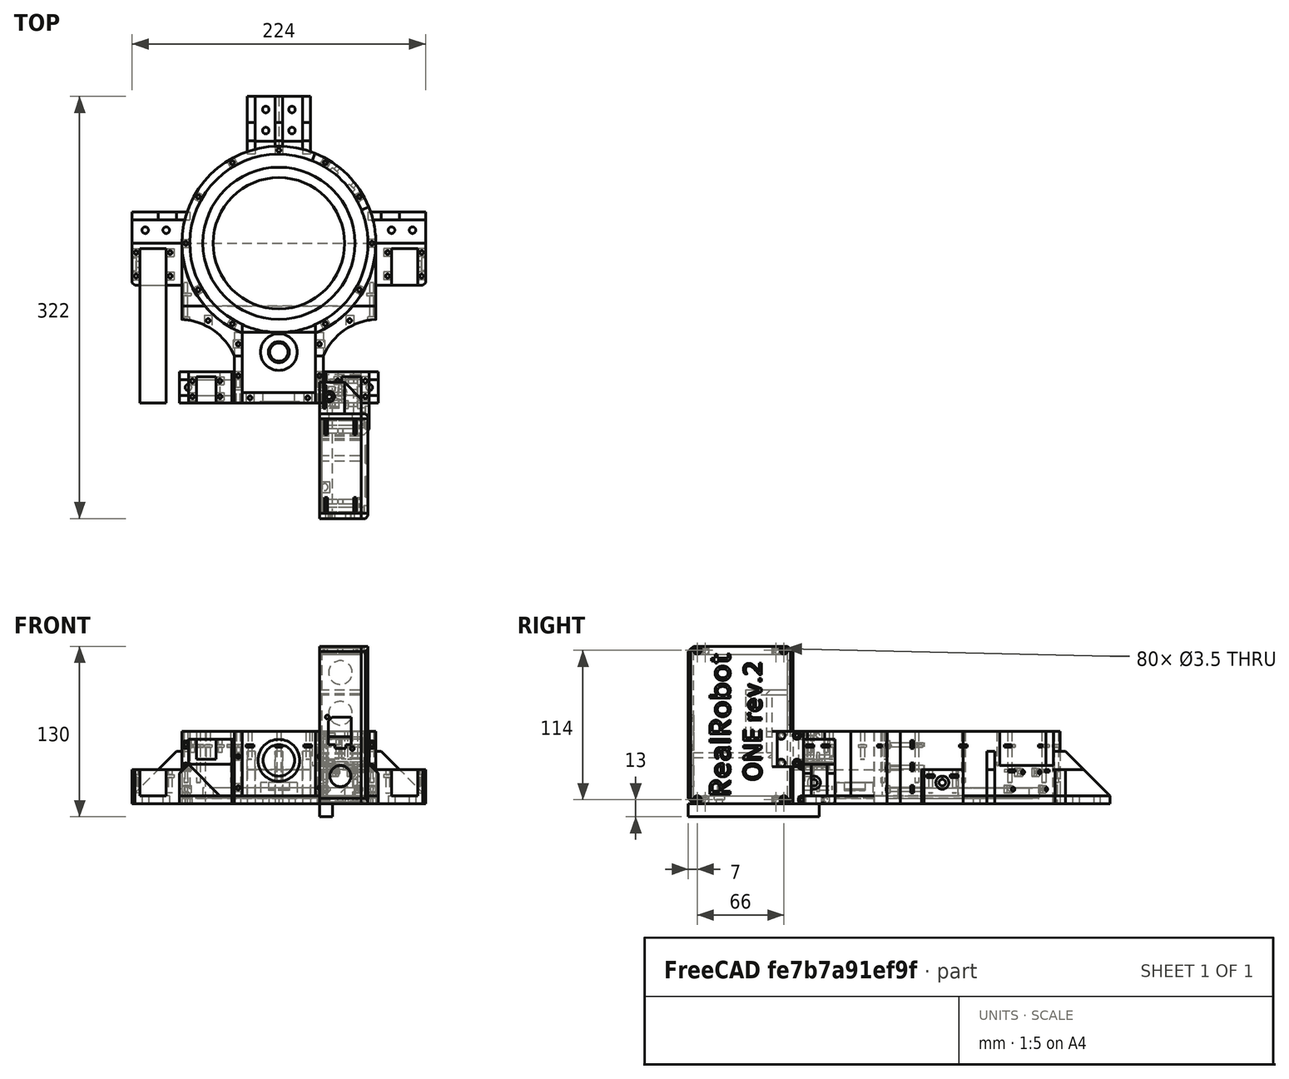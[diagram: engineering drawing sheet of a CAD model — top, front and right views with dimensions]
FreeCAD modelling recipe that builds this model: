
FCSTD DOCUMENT  (FreeCAD 0.19R24276 (Git))
Label: Ele-modules_029
License: All rights reserved
LicenseURL: http://en.wikipedia.org/wiki/All_rights_reserved
objects: Part::Cylinder×371, Part::Box×289, Part::Cut×232, Part::Compound×163, Part::Chamfer×49, Mesh::Feature×14, Part::FeaturePython×4, Part::Mirroring×3, Part::Part2DObjectPython×2, Part::Extrusion×2
note: 1115 computed .brp shape members not serialized (recipe doc carries the construction recipe); baked Part::Feature solids carry a one-line shape summary decoded from their .brp

FEATURE [Part::Cylinder] Cylinder1012  label="Válec1012"
  Angle = 360
  AttacherType = Attacher::AttachEngine3D
  Height = 10
  Placement = pos=(29,6,39) rot=(1,0,0;1.5708rad)
  Radius = 1.5
FEATURE [Part::Box] Box510  label="Krychle510"
  AttacherType = Attacher::AttachEngine3D
  Height = 6
  Length = 2
  Placement = pos=(34,64,0) rot=(0,0,1;0rad)
  Width = 6
FEATURE [Part::Cylinder] Cylinder1013  label="Válec1013"
  Angle = 360
  AttacherType = Attacher::AttachEngine3D
  Height = 60
  Placement = pos=(26,13,117) rot=(0,1,0;1.5708rad)
  Radius = 1.75
FEATURE [Part::Box] Box506  label="Krychle506"
  AttacherType = Attacher::AttachEngine3D
  Height = 6
  Length = 2
  Placement = pos=(34,64,114) rot=(0,0,1;0rad)
  Width = 6
FEATURE [Part::Box] Box509  label="Krychle509"
  AttacherType = Attacher::AttachEngine3D
  Height = 6
  Length = 2
  Placement = pos=(34,10,0) rot=(0,0,1;0rad)
  Width = 6
FEATURE [Part::Cylinder] Cylinder1011  label="Válec1011"
  Angle = 360
  AttacherType = Attacher::AttachEngine3D
  Height = 10
  Placement = pos=(16,82,66) rot=(1,0,0;1.5708rad)
  Radius = 9
FEATURE [Part::Box] Box505  label="Krychle505"
  AttacherType = Attacher::AttachEngine3D
  Height = 6
  Length = 2
  Placement = pos=(34,10,0) rot=(0,0,1;0rad)
  Width = 6
FEATURE [Part::Box] Box508  label="Krychle508"
  AttacherType = Attacher::AttachEngine3D
  Height = 6
  Length = 2
  Placement = pos=(34,10,114) rot=(0,0,1;0rad)
  Width = 6
FEATURE [Part::Cylinder] Cylinder1014  label="Válec1014"
  Angle = 360
  AttacherType = Attacher::AttachEngine3D
  Height = 10
  Placement = pos=(29,21,0) rot=(0,0,1;0rad)
  Radius = 1.5
FEATURE [Part::Cylinder] Cylinder1015  label="Válec1015"
  Angle = 360
  AttacherType = Attacher::AttachEngine3D
  Height = 60
  Placement = pos=(26,13,3) rot=(0,1,0;1.5708rad)
  Radius = 1.75
FEATURE [Part::Box] Box507  label="Krychle507"
  AttacherType = Attacher::AttachEngine3D
  Height = 108
  Length = 30
  Placement = pos=(2,4,3) rot=(0,0,1;0rad)
  Width = 72
FEATURE [Part::Box] Box515  label="Krychle515"
  AttacherType = Attacher::AttachEngine3D
  Height = 6
  Length = 2
  Placement = pos=(34,10,114) rot=(0,0,1;0rad)
  Width = 6
FEATURE [Part::Box] Box516  label="Krychle516"
  AttacherType = Attacher::AttachEngine3D
  Height = 2
  Length = 6
  Placement = pos=(0,40,3) rot=(0,0,1;0rad)
  Width = 6
FEATURE [Part::Box] Box518  label="Krychle518"
  AttacherType = Attacher::AttachEngine3D
  Height = 3
  Length = 8
  Placement = pos=(12,-2,39) rot=(0,0,1;0rad)
  Width = 10
FEATURE [Part::Cylinder] Cylinder1024  label="Válec1024"
  Angle = 360
  AttacherType = Attacher::AttachEngine3D
  Height = 3
  Placement = pos=(26,73,3) rot=(0,1,0;1.5708rad)
  Radius = 3
FEATURE [Part::Cylinder] Cylinder1022  label="Válec1022"
  Angle = 360
  AttacherType = Attacher::AttachEngine3D
  Height = 10
  Placement = pos=(16,6,18) rot=(1,0,0;1.5708rad)
  Radius = 8
FEATURE [Part::Cylinder] Cylinder1028  label="Válec1028"
  Angle = 360
  AttacherType = Attacher::AttachEngine3D
  Height = 3
  Placement = pos=(26,7,3) rot=(0,1,0;1.5708rad)
  Radius = 3
FEATURE [Part::Cylinder] Cylinder1019  label="Válec1019"
  Angle = 360
  AttacherType = Attacher::AttachEngine3D
  Height = 10
  Placement = pos=(3,43,0) rot=(0,0,1;0rad)
  Radius = 1.5
FEATURE [Part::Box] Box514  label="Krychle514"
  AttacherType = Attacher::AttachEngine3D
  Height = 21
  Length = 17.5
  Placement = pos=(10.75,-2,42) rot=(0,0,1;0rad)
  Width = 10
FEATURE [Part::Chamfer] Chamfer034
  Base = -> Box514
  Edges = 1 edges r=3: [Edge2]
  Placement = pos=(-4,0,0) rot=(0,0,1;0rad)
FEATURE [Part::Cylinder] Cylinder1018  label="Válec1018"
  Angle = 360
  AttacherType = Attacher::AttachEngine3D
  Height = 60
  Placement = pos=(26,67,3) rot=(0,1,0;1.5708rad)
  Radius = 1.75
FEATURE [Part::Cylinder] Cylinder1025  label="Válec1025"
  Angle = 360
  AttacherType = Attacher::AttachEngine3D
  Height = 60
  Placement = pos=(26,13,117) rot=(0,1,0;1.5708rad)
  Radius = 1.75
FEATURE [Part::Box] Box513  label="Krychle513"
  AttacherType = Attacher::AttachEngine3D
  Height = 6
  Length = 2
  Placement = pos=(34,64,114) rot=(0,0,1;0rad)
  Width = 6
FEATURE [Part::Compound] Compound538
  Links = -> [Box505,Box510,Box508,Box513]
  Placement = pos=(-8,0,-3) rot=(0,0,1;0rad)
FEATURE [Part::Box] Box511  label="Krychle511"
  AttacherType = Attacher::AttachEngine3D
  Height = 120
  Length = 32
  Placement = pos=(0,0,-3) rot=(0,0,1;0rad)
  Width = 80
FEATURE [Part::Cut] Cut472
  Base = -> Box511
  Tool = -> Box507
FEATURE [Part::Cylinder] Cylinder1017  label="Válec1017"
  Angle = 360
  AttacherType = Attacher::AttachEngine3D
  Height = 60
  Placement = pos=(26,67,117) rot=(0,1,0;1.5708rad)
  Radius = 1.75
FEATURE [Part::Compound] Compound544
  Links = -> [Cylinder1015,Cylinder1018,Cylinder1013,Cylinder1017]
  Placement = pos=(-8,0,-3) rot=(0,0,1;0rad)
FEATURE [Part::Box] Box512  label="Krychle512"
  AttacherType = Attacher::AttachEngine3D
  Height = 2
  Length = 6
  Placement = pos=(26,18,3) rot=(0,0,1;0rad)
  Width = 6
FEATURE [Part::Cylinder] Cylinder1016  label="Válec1016"
  Angle = 360
  AttacherType = Attacher::AttachEngine3D
  Height = 10
  Placement = pos=(10,6,63) rot=(1,0,0;1.5708rad)
  Radius = 1.5
FEATURE [Part::Compound] Compound543
  Links = -> [Cylinder1016,Cylinder1012]
  Placement = pos=(-4,0,0) rot=(0,0,1;0rad)
FEATURE [Part::Cylinder] Cylinder1020  label="Válec1020"
  Angle = 360
  AttacherType = Attacher::AttachEngine3D
  Height = 10
  Placement = pos=(3,21,0) rot=(0,0,1;0rad)
  Radius = 1.5
FEATURE [Part::Cylinder] Cylinder1021  label="Válec1021"
  Angle = 360
  AttacherType = Attacher::AttachEngine3D
  Height = 60
  Placement = pos=(26,13,3) rot=(0,1,0;1.5708rad)
  Radius = 1.75
FEATURE [Part::Box] Box517  label="Krychle517"
  AttacherType = Attacher::AttachEngine3D
  Height = 2
  Length = 6
  Placement = pos=(26,40,3) rot=(0,0,1;0rad)
  Width = 6
FEATURE [Part::Cylinder] Cylinder1023  label="Válec1023"
  Angle = 360
  AttacherType = Attacher::AttachEngine3D
  Height = 100
  Placement = pos=(26,73,117) rot=(0,1,0;1.5708rad)
  Radius = 1.75
FEATURE [Part::Cylinder] Cylinder1026  label="Válec1026"
  Angle = 360
  AttacherType = Attacher::AttachEngine3D
  Height = 3
  Placement = pos=(26,7,117) rot=(0,1,0;1.5708rad)
  Radius = 3
FEATURE [Part::Cylinder] Cylinder1027  label="Válec1027"
  Angle = 360
  AttacherType = Attacher::AttachEngine3D
  Height = 60
  Placement = pos=(26,67,3) rot=(0,1,0;1.5708rad)
  Radius = 1.75
FEATURE [Part::Cylinder] Cylinder1036  label="Válec1036"
  Angle = 360
  AttacherType = Attacher::AttachEngine3D
  Height = 3
  Placement = pos=(26,7,3) rot=(0,1,0;1.5708rad)
  Radius = 3
FEATURE [Part::Cylinder] Cylinder1030  label="Válec1030"
  Angle = 360
  AttacherType = Attacher::AttachEngine3D
  Height = 100
  Placement = pos=(26,7,117) rot=(0,1,0;1.5708rad)
  Radius = 1.75
FEATURE [Part::Cylinder] Cylinder1034  label="Válec1034"
  Angle = 360
  AttacherType = Attacher::AttachEngine3D
  Height = 10
  Placement = pos=(29,43,0) rot=(0,0,1;0rad)
  Radius = 1.5
FEATURE [Part::Cylinder] Cylinder1029  label="Válec1029"
  Angle = 360
  AttacherType = Attacher::AttachEngine3D
  Height = 100
  Placement = pos=(26,73,3) rot=(0,1,0;1.5708rad)
  Radius = 1.75
FEATURE [Part::Cylinder] Cylinder1033  label="Válec1033"
  Angle = 360
  AttacherType = Attacher::AttachEngine3D
  Height = 3
  Placement = pos=(26,73,117) rot=(0,1,0;1.5708rad)
  Radius = 3
FEATURE [Part::Cylinder] Cylinder1035  label="Válec1035"
  Angle = 360
  AttacherType = Attacher::AttachEngine3D
  Height = 3
  Placement = pos=(26,73,3) rot=(0,1,0;1.5708rad)
  Radius = 3
FEATURE [Part::Box] Box526  label="Krychle526"
  AttacherType = Attacher::AttachEngine3D
  Height = 6
  Length = 2
  Placement = pos=(26,68,46) rot=(0,0,1;0rad)
  Width = 6
FEATURE [Part::Cylinder] Cylinder1039  label="Válec1039"
  Angle = 360
  AttacherType = Attacher::AttachEngine3D
  Height = 20
  Placement = pos=(24.5,77,20) rot=(0,0,1;0rad)
  Radius = 2
FEATURE [Part::Cylinder] Cylinder1038  label="Válec1038"
  Angle = 360
  AttacherType = Attacher::AttachEngine3D
  Height = 3
  Placement = pos=(26,73,117) rot=(0,1,0;1.5708rad)
  Radius = 3
FEATURE [Part::Compound] Compound542
  Links = -> [Cylinder1036,Cylinder1035,Cylinder1026,Cylinder1038]
  Placement = pos=(3,0,-3) rot=(0,0,1;0rad)
FEATURE [Part::Cylinder] Cylinder1041  label="Válec1041"
  Angle = 360
  AttacherType = Attacher::AttachEngine3D
  Height = 20
  Placement = pos=(20,71,49) rot=(0,1,0;1.5708rad)
  Radius = 1.5
FEATURE [Part::Cylinder] Cylinder1032  label="Válec1032"
  Angle = 360
  AttacherType = Attacher::AttachEngine3D
  Height = 60
  Placement = pos=(26,67,117) rot=(0,1,0;1.5708rad)
  Radius = 1.75
FEATURE [Part::Compound] Compound537
  Links = -> [Cylinder1021,Cylinder1027,Cylinder1025,Cylinder1032]
  Placement = pos=(-72,0,-3) rot=(0,0,1;0rad)
FEATURE [Part::Box] Box523  label="Krychle523"
  AttacherType = Attacher::AttachEngine3D
  Height = 15
  Length = 15
  Placement = pos=(17,68,31) rot=(0,0,1;0rad)
  Width = 80
FEATURE [Part::Cylinder] Cylinder1042  label="Válec1042"
  Angle = 360
  AttacherType = Attacher::AttachEngine3D
  Height = 20
  Placement = pos=(20,71,28) rot=(0,1,0;1.5708rad)
  Radius = 1.5
FEATURE [Part::Box] Box520  label="Krychle520"
  AttacherType = Attacher::AttachEngine3D
  Height = 2
  Length = 6
  Placement = pos=(0,18,3) rot=(0,0,1;0rad)
  Width = 6
FEATURE [Part::Compound] Compound539
  Links = -> [Box520,Box516,Box517,Box512]
  Placement = pos=(0,0,-100) rot=(0,0,1;0rad)
FEATURE [Part::Box] Box519  label="Krychle519"
  AttacherType = Attacher::AttachEngine3D
  Height = 6
  Length = 2
  Placement = pos=(34,64,0) rot=(0,0,1;0rad)
  Width = 6
FEATURE [Part::Compound] Compound540
  Links = -> [Box509,Box519,Box515,Box506]
  Placement = pos=(-30,0,-3) rot=(0,0,1;0rad)
FEATURE [Part::Cylinder] Cylinder1031  label="Válec1031"
  Angle = 360
  AttacherType = Attacher::AttachEngine3D
  Height = 100
  Placement = pos=(26,7,3) rot=(0,1,0;1.5708rad)
  Radius = 1.75
FEATURE [Part::Compound] Compound536
  Links = -> [Cylinder1031,Cylinder1029,Cylinder1030,Cylinder1023]
  Placement = pos=(-72,0,-3) rot=(0,0,1;0rad)
FEATURE [Part::Box] Box521  label="Krychle521"
  AttacherType = Attacher::AttachEngine3D
  Height = 6
  Length = 2
  Placement = pos=(26,80,46) rot=(0,0,1;0rad)
  Width = 6
FEATURE [Part::Box] Box522  label="Krychle522"
  AttacherType = Attacher::AttachEngine3D
  Height = 6
  Length = 2
  Placement = pos=(26,80,25) rot=(0,0,1;0rad)
  Width = 6
FEATURE [Part::Box] Box525  label="Krychle525"
  AttacherType = Attacher::AttachEngine3D
  Height = 6
  Length = 2
  Placement = pos=(26,68,25) rot=(0,0,1;0rad)
  Width = 6
FEATURE [Part::Cylinder] Cylinder1037  label="Válec1037"
  Angle = 360
  AttacherType = Attacher::AttachEngine3D
  Height = 3
  Placement = pos=(26,7,117) rot=(0,1,0;1.5708rad)
  Radius = 3
FEATURE [Part::Compound] Compound541
  Links = -> [Cylinder1028,Cylinder1024,Cylinder1037,Cylinder1033]
  Placement = pos=(-26,0,-3) rot=(0,0,1;0rad)
FEATURE [Part::Box] Box524  label="Krychle524"
  AttacherType = Attacher::AttachEngine3D
  Height = 27
  Length = 19
  Placement = pos=(13,64,25) rot=(0,0,1;0rad)
  Width = 24
FEATURE [Part::Cylinder] Cylinder1040  label="Válec1040"
  Angle = 360
  AttacherType = Attacher::AttachEngine3D
  Height = 3
  Placement = pos=(24.5,77,25) rot=(0,0,1;0rad)
  Radius = 4
FEATURE [Part::Cylinder] Cylinder1045  label="Válec1045"
  Angle = 360
  AttacherType = Attacher::AttachEngine3D
  Height = 20
  Placement = pos=(24.5,77,38) rot=(0,0,1;0rad)
  Radius = 2
FEATURE [Part::Cylinder] Cylinder1044  label="Válec1044"
  Angle = 360
  AttacherType = Attacher::AttachEngine3D
  Height = 20
  Placement = pos=(20,83,49) rot=(0,1,0;1.5708rad)
  Radius = 1.5
FEATURE [Part::Cylinder] Cylinder1046  label="Válec1046"
  Angle = 360
  AttacherType = Attacher::AttachEngine3D
  Height = 3
  Placement = pos=(24.5,77,49) rot=(0,0,1;0rad)
  Radius = 4
FEATURE [Part::Box] Box527  label="Krychle527"
  AttacherType = Attacher::AttachEngine3D
  Height = 27
  Length = 13
  Placement = pos=(0,64,25) rot=(0,0,1;0rad)
  Width = 24
FEATURE [Part::Cylinder] Cylinder1043  label="Válec1043"
  Angle = 360
  AttacherType = Attacher::AttachEngine3D
  Height = 20
  Placement = pos=(20,83,28) rot=(0,1,0;1.5708rad)
  Radius = 1.5
FEATURE [Part::Compound] Compound548
  Links = -> [Cylinder1042,Cylinder1043,Cylinder1041,Cylinder1044]
FEATURE [Part::Compound] Compound547
  Links = -> [Box522,Box525,Box521,Box526]
  Placement = pos=(1,0,0) rot=(0,0,1;0rad)
FEATURE [Part::Chamfer] Chamfer035
  Base = -> Box527
  Edges = 1 edges r=12.9: [Edge3]
FEATURE [Part::Compound] Compound546
  Links = -> [Cylinder1020,Cylinder1019,Cylinder1014,Cylinder1034]
  Placement = pos=(0,0,-100) rot=(0,0,1;0rad)
FEATURE [Part::Cut] Cut486
  Base = -> Box524
  Tool = -> Box523
FEATURE [Part::Cut] Cut487
  Base = -> Cut486
  Tool = -> Compound547
FEATURE [Part::Cut] Cut488
  Base = -> Cut487
  Tool = -> Compound548
FEATURE [Part::Cut] Cut492
  Base = -> Cut488
  Tool = -> Cylinder1039
FEATURE [Part::Cut] Cut490
  Base = -> Cut492
  Tool = -> Cylinder1040
FEATURE [Part::Cut] Cut482
  Base = -> Cut472
  Tool = -> Compound538
FEATURE [Part::Cut] Cut474
  Base = -> Cut482
  Tool = -> Compound544
FEATURE [Part::Cut] Cut480
  Base = -> Cut474
  Tool = -> Cylinder1011
FEATURE [Part::Cut] Cut481
  Base = -> Cut480
  Tool = -> Chamfer034
FEATURE [Part::Cut] Cut477
  Base = -> Cut481
  Tool = -> Compound543
FEATURE [Part::Cut] Cut484
  Base = -> Cut477
  Tool = -> Box518
FEATURE [Part::Cut] Cut479
  Base = -> Cut484
  Tool = -> Cylinder1022
FEATURE [Part::Cut] Cut485
  Base = -> Cut479
  Tool = -> Compound539
FEATURE [Part::Cut] Cut476
  Base = -> Cut485
  Tool = -> Compound546
FEATURE [Part::Cut] Cut471
  Base = -> Cut476
  Tool = -> Compound540
FEATURE [Part::Cut] Cut483
  Base = -> Cut471
  Tool = -> Compound537
FEATURE [Part::Cut] Cut475
  Base = -> Cut483
  Tool = -> Compound536
FEATURE [Part::Cut] Cut478
  Base = -> Cut475
  Tool = -> Compound542
FEATURE [Part::Cut] Cut473
  Base = -> Cut478
  Tool = -> Compound541
FEATURE [Part::Cut] Cut489
  Base = -> Cut490
  Tool = -> Cylinder1046
FEATURE [Part::Cut] Cut491
  Base = -> Cut489
  Tool = -> Cylinder1045
FEATURE [Part::Compound] Compound549  label="Ele-box_small-extrusion"
  Links = -> [Chamfer035,Cut491]
  Placement = pos=(0,16,0) rot=(0,0,1;0rad)
FEATURE [Part::Box] Box711  label="Krychle711"
  AttacherType = Attacher::AttachEngine3D
  Height = 2
  Length = 6
  Placement = pos=(-27,74,39) rot=(0,0,1;1.5708rad)
  Width = 8
FEATURE [Part::Cylinder] Cylinder1781  label="Válec1781"
  Angle = 360
  AttacherType = Attacher::AttachEngine3D
  Height = 50
  Placement = pos=(-71,106,73) rot=(1,0,0;1.5708rad)
  Radius = 3
FEATURE [Part::Box] Box727  label="Krychle727"
  AttacherType = Attacher::AttachEngine3D
  Height = 55
  Length = 148
  Placement = pos=(-74,48,29) rot=(0,0,1;0rad)
  Width = 38
FEATURE [Part::Cylinder] Cylinder1778  label="Válec1778"
  Angle = 360
  AttacherType = Attacher::AttachEngine3D
  Height = 55
  Placement = pos=(76.3,104,29) rot=(0,0,1;0rad)
  Radius = 46
FEATURE [Part::Cylinder] Cylinder1779  label="Válec1779"
  Angle = 360
  AttacherType = Attacher::AttachEngine3D
  Height = 55
  Placement = pos=(0,0,29) rot=(0,0,1;0rad)
  Radius = 74
FEATURE [Part::Cylinder] Cylinder1780  label="Válec1780"
  Angle = 360
  AttacherType = Attacher::AttachEngine3D
  Height = 50
  Placement = pos=(-71,80,73) rot=(1,0,0;1.5708rad)
  Radius = 1.5
FEATURE [Part::Cylinder] Cylinder1777  label="Válec1777"
  Angle = 360
  AttacherType = Attacher::AttachEngine3D
  Height = 55
  Placement = pos=(-76.3,104,29) rot=(0,0,1;0rad)
  Radius = 46
FEATURE [Part::Box] Box728  label="Krychle728"
  AttacherType = Attacher::AttachEngine3D
  Height = 55
  Length = 56
  Placement = pos=(-28,0,29) rot=(0,0,1;0rad)
  Width = 200
FEATURE [Part::Cylinder] Cylinder1793  label="Válec1793"
  Angle = 360
  AttacherType = Attacher::AttachEngine3D
  Height = 6
  Placement = pos=(0,83,68) rot=(0,0,1;0rad)
  Radius = 8
FEATURE [Part::Cylinder] Cylinder1795  label="Válec1795"
  Angle = 360
  AttacherType = Attacher::AttachEngine3D
  Height = 50
  Placement = pos=(-31,77,0) rot=(0,0,1;0.785398rad)
  Radius = 1.5
FEATURE [Part::Cylinder] Cylinder1794  label="Válec1794"
  Angle = 360
  AttacherType = Attacher::AttachEngine3D
  Height = 50
  Placement = pos=(31,77,0) rot=(0,0,1;0.785398rad)
  Radius = 1.5
FEATURE [Part::Compound] Compound902
  Links = -> [Cylinder1794,Cylinder1795]
FEATURE [Part::Cylinder] Cylinder1784  label="Válec1784"
  Angle = 360
  AttacherType = Attacher::AttachEngine3D
  Height = 50
  Placement = pos=(-71,80,39) rot=(1,0,0;1.5708rad)
  Radius = 1.5
FEATURE [Part::Cylinder] Cylinder1786  label="Válec1786"
  Angle = 360
  AttacherType = Attacher::AttachEngine3D
  Height = 50
  Placement = pos=(71,80,39) rot=(1,0,0;1.5708rad)
  Radius = 1.5
FEATURE [Part::Cylinder] Cylinder1782  label="Válec1782"
  Angle = 360
  AttacherType = Attacher::AttachEngine3D
  Height = 50
  Placement = pos=(-71,106,39) rot=(1,0,0;1.5708rad)
  Radius = 3
FEATURE [Part::Cylinder] Cylinder1787  label="Válec1787"
  Angle = 360
  AttacherType = Attacher::AttachEngine3D
  Height = 50
  Placement = pos=(71,80,73) rot=(1,0,0;1.5708rad)
  Radius = 1.5
FEATURE [Part::Cylinder] Cylinder1788  label="Válec1788"
  Angle = 360
  AttacherType = Attacher::AttachEngine3D
  Height = 50
  Placement = pos=(-71,80,56) rot=(1,0,0;1.5708rad)
  Radius = 1.5
FEATURE [Part::Cylinder] Cylinder1789  label="Válec1789"
  Angle = 360
  AttacherType = Attacher::AttachEngine3D
  Height = 50
  Placement = pos=(71,80,57) rot=(1,0,0;1.5708rad)
  Radius = 1.5
FEATURE [Part::Compound] Compound899
  Links = -> [Cylinder1784,Cylinder1786,Cylinder1780,Cylinder1787,Cylinder1788,Cylinder1789]
FEATURE [Part::Cylinder] Cylinder1790  label="Válec1790"
  Angle = 360
  AttacherType = Attacher::AttachEngine3D
  Height = 50
  Placement = pos=(71,106,57) rot=(1,0,0;1.5708rad)
  Radius = 3
FEATURE [Part::Cylinder] Cylinder1791  label="Válec1791"
  Angle = 360
  AttacherType = Attacher::AttachEngine3D
  Height = 50
  Placement = pos=(-71,106,56) rot=(1,0,0;1.5708rad)
  Radius = 3
FEATURE [Part::Cylinder] Cylinder1783  label="Válec1783"
  Angle = 360
  AttacherType = Attacher::AttachEngine3D
  Height = 50
  Placement = pos=(71,106,73) rot=(1,0,0;1.5708rad)
  Radius = 3
FEATURE [Part::Box] Box729  label="Krychle729"
  AttacherType = Attacher::AttachEngine3D
  Height = 2
  Length = 6
  Placement = pos=(35,74,39) rot=(0,0,1;1.5708rad)
  Width = 8
FEATURE [Part::Compound] Compound901
  Links = -> [Box729,Box711]
FEATURE [Part::Cylinder] Cylinder1785  label="Válec1785"
  Angle = 360
  AttacherType = Attacher::AttachEngine3D
  Height = 50
  Placement = pos=(71,106,39) rot=(1,0,0;1.5708rad)
  Radius = 3
FEATURE [Part::Compound] Compound898
  Links = -> [Cylinder1782,Cylinder1785,Cylinder1781,Cylinder1783,Cylinder1790,Cylinder1791]
FEATURE [Part::Cylinder] Cylinder1792  label="Válec1792"
  Angle = 360
  AttacherType = Attacher::AttachEngine3D
  Height = 12
  Placement = pos=(0,83,68) rot=(0,0,1;0rad)
  Radius = 14
FEATURE [Part::Cut] Cut536
  Base = -> Box727
  Tool = -> Cylinder1777
FEATURE [Part::Cut] Cut531
  Base = -> Cut536
  Tool = -> Cylinder1778
FEATURE [Part::Cut] Cut534
  Base = -> Cut531
  Tool = -> Box728
FEATURE [Part::Cut] Cut535
  Base = -> Cut534
  Tool = -> Cylinder1779
FEATURE [Part::Cut] Cut532
  Base = -> Cut535
  Tool = -> Compound899
FEATURE [Part::Cut] Cut533
  Base = -> Cut532
  Tool = -> Compound898
FEATURE [Part::Cut] Cut538
  Base = -> Cut533
  Tool = -> Compound901
FEATURE [Part::Cut] Cut539
  Base = -> Cut538
  Tool = -> Compound902
FEATURE [Part::Cut] Cut537
  Base = -> Cylinder1792
  Tool = -> Cylinder1793
FEATURE [Part::FeaturePython] Tube039  # WARN: FeaturePython — macro-defined, semantics opaque (R4)
  AttacherType = Attacher::AttachEngine3D
  Height = 1
  InnerRadius = 7
  OuterRadius = 8
  Placement = pos=(0,83,73) rot=(0,0,1;0rad)
FEATURE [Part::Compound] Compound900
  Links = -> [Cut537,Tube039]
FEATURE [Part::Cylinder] Cylinder1798  label="Válec1798"
  Angle = 360
  AttacherType = Attacher::AttachEngine3D
  Height = 20
  Placement = pos=(-84,-12,66) rot=(0,0,1;0rad)
  Radius = 2.5
FEATURE [Part::Box] Box735  label="Krychle735"
  AttacherType = Attacher::AttachEngine3D
  Height = 15
  Length = 15
  Placement = pos=(-61,102,41) rot=(0,0,1;0rad)
  Width = 80
FEATURE [Part::Box] Box734  label="Krychle734"
  AttacherType = Attacher::AttachEngine3D
  Height = 2
  Length = 6
  Placement = pos=(-46,102,35) rot=(0,0,1;0rad)
  Width = 6
FEATURE [Part::Box] Box487  label="Krychle487"
  AttacherType = Attacher::AttachEngine3D
  Height = 2
  Length = 6
  Placement = pos=(-46,114,35) rot=(0,0,1;0rad)
  Width = 6
FEATURE [Part::Cylinder] Cylinder1801  label="Válec1801"
  Angle = 360
  AttacherType = Attacher::AttachEngine3D
  Height = 20
  Placement = pos=(-102,-16,66) rot=(0,0,1;0rad)
  Radius = 2.5
FEATURE [Part::Box] Box738  label="Krychle738"
  AttacherType = Attacher::AttachEngine3D
  Height = 24
  Length = 40
  Placement = pos=(-74,116,50) rot=(0,0,1;0rad)
  Width = 6
FEATURE [Part::Box] Box739  label="Krychle739"
  AttacherType = Attacher::AttachEngine3D
  Height = 6
  Length = 40
  Placement = pos=(-101,-24,76) rot=(0,0,1;0rad)
  Width = 24
FEATURE [Part::Cylinder] Cylinder1799  label="Válec1799"
  Angle = 360
  AttacherType = Attacher::AttachEngine3D
  Height = 16
  Placement = pos=(-43,117,25) rot=(0,0,1;0rad)
  Radius = 1.5
FEATURE [Part::Cylinder] Cylinder1800  label="Válec1800"
  Angle = 360
  AttacherType = Attacher::AttachEngine3D
  Height = 16
  Placement = pos=(-64,117,25) rot=(0,0,1;0rad)
  Radius = 1.5
FEATURE [Part::Box] Box737  label="Krychle737"
  AttacherType = Attacher::AttachEngine3D
  Height = 15
  Length = 15
  Placement = pos=(-61,102,41) rot=(0,0,1;0rad)
  Width = 80
FEATURE [Part::Box] Box740  label="Krychle740"
  AttacherType = Attacher::AttachEngine3D
  Height = 24
  Length = 40
  Placement = pos=(-74,98,50) rot=(0,0,1;0rad)
  Width = 6
FEATURE [Part::Box] Box730  label="Krychle730"
  AttacherType = Attacher::AttachEngine3D
  Height = 6
  Length = 68
  Placement = pos=(-34,68,78) rot=(0,0,1;0rad)
  Width = 54
FEATURE [Part::Box] Box733  label="Krychle733"
  AttacherType = Attacher::AttachEngine3D
  Height = 2
  Length = 6
  Placement = pos=(-67,102,35) rot=(0,0,1;0rad)
  Width = 6
FEATURE [Part::Box] Box248  label="Krychle248"
  AttacherType = Attacher::AttachEngine3D
  Height = 19
  Length = 33
  Placement = pos=(-67,98,41) rot=(0,0,1;0rad)
  Width = 24
FEATURE [Part::Cut] Cut543
  Base = -> Box248
  Placement = pos=(0,0,-10) rot=(0,0,1;0rad)
  Tool = -> Box737
FEATURE [Part::Box] Box736  label="Krychle736"
  AttacherType = Attacher::AttachEngine3D
  Height = 24
  Length = 33
  Placement = pos=(-67,98,50) rot=(0,0,1;0rad)
  Width = 24
FEATURE [Part::Box] Box741  label="Krychle741"
  AttacherType = Attacher::AttachEngine3D
  Height = 2
  Length = 6
  Placement = pos=(-67,114,35) rot=(0,0,1;0rad)
  Width = 6
FEATURE [Part::Cylinder] Cylinder1802  label="Válec1802"
  Angle = 360
  AttacherType = Attacher::AttachEngine3D
  Height = 16
  Placement = pos=(-43,105,25) rot=(0,0,1;0rad)
  Radius = 1.5
FEATURE [Part::Cylinder] Cylinder1803  label="Válec1803"
  Angle = 360
  AttacherType = Attacher::AttachEngine3D
  Height = 16
  Placement = pos=(-64,105,25) rot=(0,0,1;0rad)
  Radius = 1.5
FEATURE [Part::Box] Box742  label="Krychle742"
  AttacherType = Attacher::AttachEngine3D
  Height = 6
  Length = 40
  Placement = pos=(-101,-24,76) rot=(0,0,1;0rad)
  Width = 24
FEATURE [Part::Cylinder] Cylinder1805  label="Válec1805"
  Angle = 360
  AttacherType = Attacher::AttachEngine3D
  Height = 20
  Placement = pos=(-84,-12,66) rot=(0,0,1;0rad)
  Radius = 2.5
FEATURE [Part::Cylinder] Cylinder1804  label="Válec1804"
  Angle = 360
  AttacherType = Attacher::AttachEngine3D
  Height = 20
  Placement = pos=(-102,-16,66) rot=(0,0,1;0rad)
  Radius = 2.5
FEATURE [Part::Box] Box743  label="Krychle743"
  AttacherType = Attacher::AttachEngine3D
  Height = 2
  Length = 6
  Placement = pos=(-46,114,35) rot=(0,0,1;0rad)
  Width = 6
FEATURE [Part::Box] Box744  label="Krychle744"
  AttacherType = Attacher::AttachEngine3D
  Height = 24
  Length = 40
  Placement = pos=(-74,116,50) rot=(0,0,1;0rad)
  Width = 6
FEATURE [Part::Box] Box746  label="Krychle746"
  AttacherType = Attacher::AttachEngine3D
  Height = 24
  Length = 40
  Placement = pos=(-74,98,50) rot=(0,0,1;0rad)
  Width = 6
FEATURE [Part::Box] Box748  label="Krychle748"
  AttacherType = Attacher::AttachEngine3D
  Height = 24
  Length = 33
  Placement = pos=(-67,98,50) rot=(0,0,1;0rad)
  Width = 24
FEATURE [Part::Box] Box749  label="Krychle749"
  AttacherType = Attacher::AttachEngine3D
  Height = 2
  Length = 6
  Placement = pos=(-67,102,35) rot=(0,0,1;0rad)
  Width = 6
FEATURE [Part::Box] Box745  label="Krychle745"
  AttacherType = Attacher::AttachEngine3D
  Height = 2
  Length = 6
  Placement = pos=(-67,114,35) rot=(0,0,1;0rad)
  Width = 6
FEATURE [Part::Box] Box747  label="Krychle747"
  AttacherType = Attacher::AttachEngine3D
  Height = 19
  Length = 33
  Placement = pos=(-67,98,41) rot=(0,0,1;0rad)
  Width = 24
FEATURE [Part::Cut] Cut547
  Base = -> Box747
  Placement = pos=(0,0,-10) rot=(0,0,1;0rad)
  Tool = -> Box735
FEATURE [Part::Cylinder] Cylinder1806  label="Válec1806"
  Angle = 360
  AttacherType = Attacher::AttachEngine3D
  Height = 16
  Placement = pos=(-43,105,25) rot=(0,0,1;0rad)
  Radius = 1.5
FEATURE [Part::Chamfer] Chamfer005
  Base = -> Box746
  Edges = 1 edges r=7: [Edge4]
FEATURE [Part::Compound] Compound909
  Links = -> [Box733,Box741,Box734,Box487]
FEATURE [Part::Chamfer] Chamfer058
  Base = -> Box740
  Edges = 1 edges r=7: [Edge4]
FEATURE [Part::Chamfer] Chamfer
  Base = -> Box736
  Edges = 1 edges r=23.9: [Edge2]
FEATURE [Part::Compound] Compound906
  Links = -> [Cylinder1801,Cylinder1798]
  Placement = pos=(-10,0,0) rot=(0,0,1;0rad)
FEATURE [Part::Cut] Cut542
  Base = -> Box739
  Placement = pos=(27,122,-2) rot=(0,0,1;0rad)
  Tool = -> Compound906
FEATURE [Part::Compound] Compound524
  Links = -> [Cylinder1804,Cylinder1805]
  Placement = pos=(-10,0,0) rot=(0,0,1;0rad)
FEATURE [Part::Cut] Cut545
  Base = -> Box742
  Placement = pos=(27,122,-2) rot=(0,0,1;0rad)
  Tool = -> Compound524
FEATURE [Part::Compound] Compound908
  Links = -> [Cylinder1799,Cylinder1802,Cylinder1800,Cylinder1803]
FEATURE [Part::Cut] Cut544
  Base = -> Cut543
  Tool = -> Compound908
FEATURE [Part::Chamfer] Chamfer001
  Base = -> Box738
  Edges = 1 edges r=7: [Edge4]
FEATURE [Part::Chamfer] Chamfer059
  Base = -> Box748
  Edges = 1 edges r=23.9: [Edge2]
FEATURE [Part::Chamfer] Chamfer060
  Base = -> Box744
  Edges = 1 edges r=7: [Edge4]
FEATURE [Part::Cut] Cut549
  Base = -> Cut544
  Tool = -> Compound909
FEATURE [Part::Compound] Compound910  label="stabilo_left_back"
  Links = -> [Chamfer058,Chamfer001,Chamfer,Cut542,Cut549]
  Placement = pos=(-2,0,4) rot=(0,0,1;0rad)
FEATURE [Part::Box] Box750  label="Krychle750"
  AttacherType = Attacher::AttachEngine3D
  Height = 2
  Length = 6
  Placement = pos=(-46,102,35) rot=(0,0,1;0rad)
  Width = 6
FEATURE [Part::Compound] Compound527
  Links = -> [Box749,Box745,Box750,Box743]
FEATURE [Part::Cylinder] Cylinder1809  label="Válec1809"
  Angle = 360
  AttacherType = Attacher::AttachEngine3D
  Height = 16
  Placement = pos=(-64,117,25) rot=(0,0,1;0rad)
  Radius = 1.5
FEATURE [Part::Cylinder] Cylinder1807  label="Válec1807"
  Angle = 360
  AttacherType = Attacher::AttachEngine3D
  Height = 16
  Placement = pos=(-43,117,25) rot=(0,0,1;0rad)
  Radius = 1.5
FEATURE [Part::Cylinder] Cylinder1808  label="Válec1808"
  Angle = 360
  AttacherType = Attacher::AttachEngine3D
  Height = 16
  Placement = pos=(-64,105,25) rot=(0,0,1;0rad)
  Radius = 1.5
FEATURE [Part::Compound] Compound526
  Links = -> [Cylinder1807,Cylinder1806,Cylinder1809,Cylinder1808]
FEATURE [Part::Cut] Cut546
  Base = -> Cut547
  Tool = -> Compound526
FEATURE [Part::Cut] Cut548
  Base = -> Cut546
  Tool = -> Compound527
FEATURE [Part::Compound] Compound907  label="stabilo_left_back001"
  Links = -> [Chamfer005,Chamfer060,Chamfer059,Cut545,Cut548]
FEATURE [Part::Mirroring] mirror004  label="stabilo_right_back"
  Base = (0,0,0)
  Normal = (1,0,0)
  Placement = pos=(2,0,4) rot=(0,0,1;0rad)
  Source = -> Compound907
FEATURE [Part::Box] Box  label="Krychle"
  AttacherType = Attacher::AttachEngine3D
  Height = 49
  Length = 2
  Placement = pos=(34,98,35) rot=(0,0,1;0rad)
  Width = 24
FEATURE [Part::Box] Box751  label="Krychle751"
  AttacherType = Attacher::AttachEngine3D
  Height = 49
  Length = 2
  Placement = pos=(-36,98,35) rot=(0,0,1;0rad)
  Width = 24
FEATURE [Part::FeaturePython] Tube044  label="6003-2RS004"  # WARN: FeaturePython — macro-defined, semantics opaque (R4)
  AttacherType = Attacher::AttachEngine3D
  Height = 10
  InnerRadius = 8.5
  OuterRadius = 16
  Placement = pos=(0,131,51) rot=(1,0,0;1.5708rad)
FEATURE [Part::Cylinder] Cylinder1871  label="Válec1871"
  Angle = 360
  AttacherType = Attacher::AttachEngine3D
  Height = 50
  Placement = pos=(-31,101,0) rot=(0,0,1;0.785398rad)
  Radius = 1.5
FEATURE [Part::Box] Box778  label="Krychle778"
  AttacherType = Attacher::AttachEngine3D
  Height = 6
  Length = 49
  Placement = pos=(28,86,78) rot=(0,1,0;1.5708rad)
  Width = 36
FEATURE [Part::Box] Box779  label="Krychle779"
  AttacherType = Attacher::AttachEngine3D
  Height = 2
  Length = 6
  Placement = pos=(35,98,39) rot=(0,0,1;1.5708rad)
  Width = 8
FEATURE [Part::Compound] Compound940
  Links = -> [Box779]
FEATURE [Part::Box] Box781  label="Krychle781"
  AttacherType = Attacher::AttachEngine3D
  Height = 2
  Length = 6
  Placement = pos=(-27,98,39) rot=(0,0,1;1.5708rad)
  Width = 8
FEATURE [Part::Compound] Compound938
  Links = -> [Box781]
FEATURE [Part::Box] Box784  label="Krychle784"
  AttacherType = Attacher::AttachEngine3D
  Height = 6
  Length = 49
  Placement = pos=(-34,86,78) rot=(0,1,0;1.5708rad)
  Width = 36
FEATURE [Part::Cut] Cut586
  Base = -> Box784
  Tool = -> Compound938
FEATURE [Part::Cylinder] Cylinder1880  label="Válec1880"
  Angle = 360
  AttacherType = Attacher::AttachEngine3D
  Height = 50
  Placement = pos=(-31,150,72) rot=(1,0,0;1.5708rad)
  Radius = 1.5
FEATURE [Part::Cylinder] Cylinder1882  label="Válec1882"
  Angle = 360
  AttacherType = Attacher::AttachEngine3D
  Height = 50
  Placement = pos=(31,150,72) rot=(1,0,0;1.5708rad)
  Radius = 1.5
FEATURE [Part::Cylinder] Cylinder1879  label="Válec1879"
  Angle = 360
  AttacherType = Attacher::AttachEngine3D
  Height = 50
  Placement = pos=(-31,150,48) rot=(1,0,0;1.5708rad)
  Radius = 1.5
FEATURE [Part::Box] Box787  label="Krychle787"
  AttacherType = Attacher::AttachEngine3D
  Height = 49
  Length = 56
  Placement = pos=(-28,114,29) rot=(0,0,1;0rad)
  Width = 8
FEATURE [Part::Cylinder] Cylinder1877  label="Válec1877"
  Angle = 360
  AttacherType = Attacher::AttachEngine3D
  Height = 50
  Placement = pos=(31,101,0) rot=(0,0,1;0.785398rad)
  Radius = 1.5
FEATURE [Part::Box] Box788  label="Krychle788"
  AttacherType = Attacher::AttachEngine3D
  Height = 6
  Length = 2
  Placement = pos=(-28,110,69) rot=(0,0,1;1.5708rad)
  Width = 6
FEATURE [Part::Box] Box789  label="Krychle789"
  AttacherType = Attacher::AttachEngine3D
  Height = 6
  Length = 2
  Placement = pos=(-28,110,45) rot=(0,0,1;1.5708rad)
  Width = 6
FEATURE [Part::Box] Box790  label="Krychle790"
  AttacherType = Attacher::AttachEngine3D
  Height = 6
  Length = 2
  Placement = pos=(34,110,69) rot=(0,0,1;1.5708rad)
  Width = 6
FEATURE [Part::Cylinder] Cylinder1878  label="Válec1878"
  Angle = 360
  AttacherType = Attacher::AttachEngine3D
  Height = 20
  Placement = pos=(0,124,51) rot=(1,0,0;1.5708rad)
  Radius = 12
FEATURE [Part::Cylinder] Cylinder1881  label="Válec1881"
  Angle = 360
  AttacherType = Attacher::AttachEngine3D
  Height = 50
  Placement = pos=(31,150,48) rot=(1,0,0;1.5708rad)
  Radius = 1.5
FEATURE [Part::Cylinder] Cylinder1888  label="Válec1888"
  Angle = 360
  AttacherType = Attacher::AttachEngine3D
  Height = 50
  Placement = pos=(31,150,48) rot=(1,0,0;1.5708rad)
  Radius = 1.5
FEATURE [Part::Box] Box798  label="Krychle798"
  AttacherType = Attacher::AttachEngine3D
  Height = 2
  Length = 6
  Placement = pos=(-57,56,29) rot=(0,0,1;0rad)
  Width = 12
FEATURE [Part::Box] Box797  label="Krychle797"
  AttacherType = Attacher::AttachEngine3D
  Height = 6
  Length = 2
  Placement = pos=(34,110,45) rot=(0,0,1;1.5708rad)
  Width = 6
FEATURE [Part::Box] Box792  label="Krychle792"
  AttacherType = Attacher::AttachEngine3D
  Height = 2
  Length = 8
  Placement = pos=(-19,114,39) rot=(0,0,1;1.5708rad)
  Width = 6
FEATURE [Part::Box] Box793  label="Krychle793"
  AttacherType = Attacher::AttachEngine3D
  Height = 2
  Length = 8
  Placement = pos=(25,114,39) rot=(0,0,1;1.5708rad)
  Width = 6
FEATURE [Part::Cylinder] Cylinder1884  label="Válec1884"
  Angle = 360
  AttacherType = Attacher::AttachEngine3D
  Height = 50
  Placement = pos=(-22,118,0) rot=(0,0,1;0.785398rad)
  Radius = 1.5
FEATURE [Part::Box] Box795  label="Krychle795"
  AttacherType = Attacher::AttachEngine3D
  Height = 6
  Length = 2
  Placement = pos=(34,110,69) rot=(0,0,1;1.5708rad)
  Width = 6
FEATURE [Part::Cylinder] Cylinder1883  label="Válec1883"
  Angle = 360
  AttacherType = Attacher::AttachEngine3D
  Height = 50
  Placement = pos=(22,118,0) rot=(0,0,1;0.785398rad)
  Radius = 1.5
FEATURE [Part::Box] Box796  label="Krychle796"
  AttacherType = Attacher::AttachEngine3D
  Height = 6
  Length = 2
  Placement = pos=(-28,110,45) rot=(0,0,1;1.5708rad)
  Width = 6
FEATURE [Part::Cylinder] Cylinder1885  label="Válec1885"
  Angle = 360
  AttacherType = Attacher::AttachEngine3D
  Height = 50
  Placement = pos=(-31,150,48) rot=(1,0,0;1.5708rad)
  Radius = 1.5
FEATURE [Part::Cylinder] Cylinder1886  label="Válec1886"
  Angle = 360
  AttacherType = Attacher::AttachEngine3D
  Height = 50
  Placement = pos=(-31,150,72) rot=(1,0,0;1.5708rad)
  Radius = 1.5
FEATURE [Part::Cylinder] Cylinder1889  label="Válec1889"
  Angle = 360
  AttacherType = Attacher::AttachEngine3D
  Height = 50
  Placement = pos=(54,59,0) rot=(0,0,1;0.785398rad)
  Radius = 1.5
FEATURE [Part::Box] Box791  label="Krychle791"
  AttacherType = Attacher::AttachEngine3D
  Height = 6
  Length = 2
  Placement = pos=(34,110,45) rot=(0,0,1;1.5708rad)
  Width = 6
FEATURE [Part::Box] Box794  label="Krychle794"
  AttacherType = Attacher::AttachEngine3D
  Height = 6
  Length = 2
  Placement = pos=(-28,110,69) rot=(0,0,1;1.5708rad)
  Width = 6
FEATURE [Part::Cylinder] Cylinder1887  label="Válec1887"
  Angle = 360
  AttacherType = Attacher::AttachEngine3D
  Height = 50
  Placement = pos=(31,150,72) rot=(1,0,0;1.5708rad)
  Radius = 1.5
FEATURE [Part::Cylinder] Cylinder1890  label="Válec1890"
  Angle = 360
  AttacherType = Attacher::AttachEngine3D
  Height = 50
  Placement = pos=(-54,59,0) rot=(0,0,1;0.785398rad)
  Radius = 1.5
FEATURE [Part::Box] Box799  label="Krychle799"
  AttacherType = Attacher::AttachEngine3D
  Height = 2
  Length = 6
  Placement = pos=(51,56,29) rot=(0,0,1;0rad)
  Width = 12
FEATURE [Part::Cut] Cut591
  Base = -> Box787
  Tool = -> Cylinder1878
FEATURE [Part::Compound] Compound952
  Links = -> [Box798,Box799]
  Placement = pos=(0,-1,10) rot=(0,0,1;0rad)
FEATURE [Part::Cut] Cut599
  Base = -> Cut539
  Tool = -> Compound952
FEATURE [Part::Compound] Compound944
  Links = -> [Box789,Box788,Box791,Box790]
FEATURE [Part::Compound] Compound947
  Links = -> [Cylinder1884,Cylinder1883]
FEATURE [Part::Compound] Compound948
  Links = -> [Box796,Box794,Box797,Box795]
FEATURE [Part::Compound] Compound943
  Links = -> [Cylinder1877]
FEATURE [Part::Cut] Cut587
  Base = -> Box778
  Tool = -> Compound943
FEATURE [Part::Cut] Cut585
  Base = -> Cut587
  Tool = -> Compound940
FEATURE [Part::Cut] Cut596
  Base = -> Cut585
  Tool = -> Compound944
FEATURE [Part::Compound] Compound949
  Links = -> [Cylinder1885,Cylinder1886,Cylinder1888,Cylinder1887]
FEATURE [Part::Compound] Compound951
  Links = -> [Cylinder1889,Cylinder1890]
FEATURE [Part::Cut] Cut600
  Base = -> Cut599
  Tool = -> Compound951
FEATURE [Part::Compound] Compound945
  Links = -> [Cylinder1879,Cylinder1880,Cylinder1881,Cylinder1882]
FEATURE [Part::Cut] Cut597
  Base = -> Cut596
  Tool = -> Compound945
FEATURE [Part::Compound] Compound941
  Links = -> [Cylinder1871]
FEATURE [Part::Cut] Cut589
  Base = -> Cut586
  Tool = -> Compound941
FEATURE [Part::Cut] Cut594
  Base = -> Cut589
  Tool = -> Compound948
FEATURE [Part::Cut] Cut595
  Base = -> Cut594
  Tool = -> Compound949
FEATURE [Part::Compound] Compound946
  Links = -> [Box793,Box792]
FEATURE [Part::Cut] Cut592
  Base = -> Cut591
  Tool = -> Compound946
FEATURE [Part::Cut] Cut593
  Base = -> Cut592
  Tool = -> Compound947
FEATURE [Part::Cut] Cut598
  Base = -> Cut593
  Tool = -> Tube044
FEATURE [Part::Compound] Compound1000  label="Base_rear-gearbox"
  Links = -> [Cut600,Cut598,Cut597,Cut595,Compound910,mirror004,Box,Box751,Box730,Compound900]
  Placement = pos=(-31,210,81) rot=(1,0,0;3.14159rad)
FEATURE [Part::Box] Box800  label="Krychle800"
  AttacherType = Attacher::AttachEngine3D
  Height = 10
  Length = 10
  Placement = pos=(0,0,-13) rot=(0,0,1;0rad)
  Width = 100
FEATURE [Part::Cylinder] Cylinder1891  label="Válec1891"
  Angle = 360
  AttacherType = Attacher::AttachEngine3D
  Height = 10
  Placement = pos=(16,82,97) rot=(1,0,0;1.5708rad)
  Radius = 9
FEATURE [Part::Cut] Cut
  Base = -> Cut473
  Tool = -> Cylinder1891
FEATURE [Part::Box] Box801  label="Krychle801"
  AttacherType = Attacher::AttachEngine3D
  Height = 32
  Length = 32
  Placement = pos=(0,44,48) rot=(0,0,1;0rad)
  Width = 4
FEATURE [Part::Box] Box802  label="Krychle802"
  AttacherType = Attacher::AttachEngine3D
  Height = 4
  Length = 32
  Placement = pos=(0,4,32) rot=(0,0,1;0rad)
  Width = 60
FEATURE [Part::Box] Box803  label="Krychle803"
  AttacherType = Attacher::AttachEngine3D
  Height = 4
  Length = 32
  Placement = pos=(0,44,80) rot=(0,0,1;0rad)
  Width = 32
FEATURE [Part::Box] Box804  label="Krychle804"
  AttacherType = Attacher::AttachEngine3D
  Height = 4
  Length = 32
  Placement = pos=(0,48,48) rot=(0,0,1;0rad)
  Width = 16
FEATURE [Part::Box] Box805  label="Krychle805"
  AttacherType = Attacher::AttachEngine3D
  Height = 4
  Length = 32
  Placement = pos=(0,4,32) rot=(0,0,1;0rad)
  Width = 60
FEATURE [Part::Box] Box806  label="Krychle806"
  AttacherType = Attacher::AttachEngine3D
  Height = 12
  Length = 32
  Placement = pos=(0,60,36) rot=(0,0,1;0rad)
  Width = 4
FEATURE [Part::Box] Box807  label="Krychle807"
  AttacherType = Attacher::AttachEngine3D
  Height = 44
  Length = 32
  Placement = pos=(0,60,36) rot=(0,0,1;0rad)
  Width = 4
FEATURE [Part::Box] Box808  label="Krychle808"
  AttacherType = Attacher::AttachEngine3D
  Height = 4
  Length = 32
  Placement = pos=(0,60,80) rot=(0,0,1;0rad)
  Width = 16
FEATURE [Part::Compound] Compound  label="Ele-box_separator"
  Links = -> [Box802,Box807,Box808]
FEATURE [Part::Chamfer] Chamfer061
  Base = -> Cut
  Edges = 4 edges r=4: [Edge19,Edge22,Edge44,Edge48]
FEATURE [Part::Chamfer] Chamfer062
  Base = -> Compound
  Edges = 2 edges r=3: [Edge11,Edge34]
FEATURE [Part::Compound] Compound1001  label="Ele-box_standard"
  Links = -> [Chamfer061,Chamfer062]
FEATURE [Part::Compound] Compound1002  label="Ele-box_small-hold"
  Links = -> [Compound549,Compound1001]
FEATURE [Part::Cylinder] Cylinder1892  label="Válec1892"
  Angle = 360
  AttacherType = Attacher::AttachEngine3D
  Height = 10
  Placement = pos=(29,6,39) rot=(1,0,0;1.5708rad)
  Radius = 1.5
FEATURE [Part::Box] Box809  label="Krychle809"
  AttacherType = Attacher::AttachEngine3D
  Height = 6
  Length = 2
  Placement = pos=(34,64,0) rot=(0,0,1;0rad)
  Width = 6
FEATURE [Part::Cylinder] Cylinder1893  label="Válec1893"
  Angle = 360
  AttacherType = Attacher::AttachEngine3D
  Height = 60
  Placement = pos=(26,13,117) rot=(0,1,0;1.5708rad)
  Radius = 1.75
FEATURE [Part::Box] Box810  label="Krychle810"
  AttacherType = Attacher::AttachEngine3D
  Height = 6
  Length = 2
  Placement = pos=(34,64,114) rot=(0,0,1;0rad)
  Width = 6
FEATURE [Part::Box] Box811  label="Krychle811"
  AttacherType = Attacher::AttachEngine3D
  Height = 6
  Length = 2
  Placement = pos=(34,10,0) rot=(0,0,1;0rad)
  Width = 6
FEATURE [Part::Cylinder] Cylinder1894  label="Válec1894"
  Angle = 360
  AttacherType = Attacher::AttachEngine3D
  Height = 10
  Placement = pos=(16,82,66) rot=(1,0,0;1.5708rad)
  Radius = 9
FEATURE [Part::Box] Box812  label="Krychle812"
  AttacherType = Attacher::AttachEngine3D
  Height = 6
  Length = 2
  Placement = pos=(34,10,0) rot=(0,0,1;0rad)
  Width = 6
FEATURE [Part::Box] Box813  label="Krychle813"
  AttacherType = Attacher::AttachEngine3D
  Height = 6
  Length = 2
  Placement = pos=(34,10,114) rot=(0,0,1;0rad)
  Width = 6
FEATURE [Part::Cylinder] Cylinder1895  label="Válec1895"
  Angle = 360
  AttacherType = Attacher::AttachEngine3D
  Height = 10
  Placement = pos=(29,21,0) rot=(0,0,1;0rad)
  Radius = 1.5
FEATURE [Part::Cylinder] Cylinder1896  label="Válec1896"
  Angle = 360
  AttacherType = Attacher::AttachEngine3D
  Height = 60
  Placement = pos=(26,13,3) rot=(0,1,0;1.5708rad)
  Radius = 1.75
FEATURE [Part::Box] Box814  label="Krychle814"
  AttacherType = Attacher::AttachEngine3D
  Height = 108
  Length = 30
  Placement = pos=(2,4,3) rot=(0,0,1;0rad)
  Width = 72
FEATURE [Part::Box] Box815  label="Krychle815"
  AttacherType = Attacher::AttachEngine3D
  Height = 6
  Length = 2
  Placement = pos=(34,10,114) rot=(0,0,1;0rad)
  Width = 6
FEATURE [Part::Box] Box816  label="Krychle816"
  AttacherType = Attacher::AttachEngine3D
  Height = 2
  Length = 6
  Placement = pos=(0,40,3) rot=(0,0,1;0rad)
  Width = 6
FEATURE [Part::Box] Box817  label="Krychle817"
  AttacherType = Attacher::AttachEngine3D
  Height = 3
  Length = 8
  Placement = pos=(12,-2,39) rot=(0,0,1;0rad)
  Width = 10
FEATURE [Part::Cylinder] Cylinder1897  label="Válec1897"
  Angle = 360
  AttacherType = Attacher::AttachEngine3D
  Height = 3
  Placement = pos=(26,73,3) rot=(0,1,0;1.5708rad)
  Radius = 3
FEATURE [Part::Cylinder] Cylinder1898  label="Válec1898"
  Angle = 360
  AttacherType = Attacher::AttachEngine3D
  Height = 10
  Placement = pos=(16,6,18) rot=(1,0,0;1.5708rad)
  Radius = 8
FEATURE [Part::Cylinder] Cylinder1899  label="Válec1899"
  Angle = 360
  AttacherType = Attacher::AttachEngine3D
  Height = 3
  Placement = pos=(26,7,3) rot=(0,1,0;1.5708rad)
  Radius = 3
FEATURE [Part::Cylinder] Cylinder1900  label="Válec1900"
  Angle = 360
  AttacherType = Attacher::AttachEngine3D
  Height = 10
  Placement = pos=(3,43,0) rot=(0,0,1;0rad)
  Radius = 1.5
FEATURE [Part::Box] Box818  label="Krychle818"
  AttacherType = Attacher::AttachEngine3D
  Height = 21
  Length = 17.5
  Placement = pos=(10.75,-2,42) rot=(0,0,1;0rad)
  Width = 10
FEATURE [Part::Chamfer] Chamfer063
  Base = -> Box818
  Edges = 1 edges r=3: [Edge2]
  Placement = pos=(-4,0,0) rot=(0,0,1;0rad)
FEATURE [Part::Cylinder] Cylinder1901  label="Válec1901"
  Angle = 360
  AttacherType = Attacher::AttachEngine3D
  Height = 60
  Placement = pos=(26,67,3) rot=(0,1,0;1.5708rad)
  Radius = 1.75
FEATURE [Part::Cylinder] Cylinder1902  label="Válec1902"
  Angle = 360
  AttacherType = Attacher::AttachEngine3D
  Height = 60
  Placement = pos=(26,13,117) rot=(0,1,0;1.5708rad)
  Radius = 1.75
FEATURE [Part::Box] Box819  label="Krychle819"
  AttacherType = Attacher::AttachEngine3D
  Height = 6
  Length = 2
  Placement = pos=(34,64,114) rot=(0,0,1;0rad)
  Width = 6
FEATURE [Part::Compound] Compound1008
  Links = -> [Box812,Box809,Box813,Box819]
  Placement = pos=(-8,0,-3) rot=(0,0,1;0rad)
FEATURE [Part::Box] Box820  label="Krychle820"
  AttacherType = Attacher::AttachEngine3D
  Height = 120
  Length = 32
  Placement = pos=(0,0,-3) rot=(0,0,1;0rad)
  Width = 80
FEATURE [Part::Cut] Cut601
  Base = -> Box820
  Tool = -> Box814
FEATURE [Part::Cut] Cut618
  Base = -> Cut601
  Tool = -> Compound1008
FEATURE [Part::Cylinder] Cylinder1903  label="Válec1903"
  Angle = 360
  AttacherType = Attacher::AttachEngine3D
  Height = 60
  Placement = pos=(26,67,117) rot=(0,1,0;1.5708rad)
  Radius = 1.75
FEATURE [Part::Compound] Compound1005
  Links = -> [Cylinder1896,Cylinder1901,Cylinder1893,Cylinder1903]
  Placement = pos=(-8,0,-3) rot=(0,0,1;0rad)
FEATURE [Part::Cut] Cut604
  Base = -> Cut618
  Tool = -> Compound1005
FEATURE [Part::Cut] Cut605
  Base = -> Cut604
  Tool = -> Cylinder1894
FEATURE [Part::Box] Box821  label="Krychle821"
  AttacherType = Attacher::AttachEngine3D
  Height = 2
  Length = 6
  Placement = pos=(26,18,3) rot=(0,0,1;0rad)
  Width = 6
FEATURE [Part::Cylinder] Cylinder1904  label="Válec1904"
  Angle = 360
  AttacherType = Attacher::AttachEngine3D
  Height = 10
  Placement = pos=(10,6,63) rot=(1,0,0;1.5708rad)
  Radius = 1.5
FEATURE [Part::Compound] Compound1003
  Links = -> [Cylinder1904,Cylinder1892]
  Placement = pos=(-4,0,0) rot=(0,0,1;0rad)
FEATURE [Part::Cylinder] Cylinder1905  label="Válec1905"
  Angle = 360
  AttacherType = Attacher::AttachEngine3D
  Height = 10
  Placement = pos=(3,21,0) rot=(0,0,1;0rad)
  Radius = 1.5
FEATURE [Part::Cylinder] Cylinder1906  label="Válec1906"
  Angle = 360
  AttacherType = Attacher::AttachEngine3D
  Height = 60
  Placement = pos=(26,13,3) rot=(0,1,0;1.5708rad)
  Radius = 1.75
FEATURE [Part::Box] Box822  label="Krychle822"
  AttacherType = Attacher::AttachEngine3D
  Height = 2
  Length = 6
  Placement = pos=(26,40,3) rot=(0,0,1;0rad)
  Width = 6
FEATURE [Part::Cylinder] Cylinder1907  label="Válec1907"
  Angle = 360
  AttacherType = Attacher::AttachEngine3D
  Height = 100
  Placement = pos=(26,73,117) rot=(0,1,0;1.5708rad)
  Radius = 1.75
FEATURE [Part::Cylinder] Cylinder1908  label="Válec1908"
  Angle = 360
  AttacherType = Attacher::AttachEngine3D
  Height = 3
  Placement = pos=(26,7,117) rot=(0,1,0;1.5708rad)
  Radius = 3
FEATURE [Part::Cylinder] Cylinder1909  label="Válec1909"
  Angle = 360
  AttacherType = Attacher::AttachEngine3D
  Height = 60
  Placement = pos=(26,67,3) rot=(0,1,0;1.5708rad)
  Radius = 1.75
FEATURE [Part::Cylinder] Cylinder1910  label="Válec1910"
  Angle = 360
  AttacherType = Attacher::AttachEngine3D
  Height = 3
  Placement = pos=(26,7,3) rot=(0,1,0;1.5708rad)
  Radius = 3
FEATURE [Part::Cylinder] Cylinder1911  label="Válec1911"
  Angle = 360
  AttacherType = Attacher::AttachEngine3D
  Height = 100
  Placement = pos=(26,7,117) rot=(0,1,0;1.5708rad)
  Radius = 1.75
FEATURE [Part::Cylinder] Cylinder1912  label="Válec1912"
  Angle = 360
  AttacherType = Attacher::AttachEngine3D
  Height = 10
  Placement = pos=(29,43,0) rot=(0,0,1;0rad)
  Radius = 1.5
FEATURE [Part::Cylinder] Cylinder1913  label="Válec1913"
  Angle = 360
  AttacherType = Attacher::AttachEngine3D
  Height = 100
  Placement = pos=(26,73,3) rot=(0,1,0;1.5708rad)
  Radius = 1.75
FEATURE [Part::Cylinder] Cylinder1914  label="Válec1914"
  Angle = 360
  AttacherType = Attacher::AttachEngine3D
  Height = 3
  Placement = pos=(26,73,117) rot=(0,1,0;1.5708rad)
  Radius = 3
FEATURE [Part::Cylinder] Cylinder1915  label="Válec1915"
  Angle = 360
  AttacherType = Attacher::AttachEngine3D
  Height = 3
  Placement = pos=(26,73,3) rot=(0,1,0;1.5708rad)
  Radius = 3
FEATURE [Part::Box] Box823  label="Krychle823"
  AttacherType = Attacher::AttachEngine3D
  Height = 6
  Length = 2
  Placement = pos=(26,68,46) rot=(0,0,1;0rad)
  Width = 6
FEATURE [Part::Cylinder] Cylinder1916  label="Válec1916"
  Angle = 360
  AttacherType = Attacher::AttachEngine3D
  Height = 20
  Placement = pos=(24.5,77,20) rot=(0,0,1;0rad)
  Radius = 2
FEATURE [Part::Cylinder] Cylinder1917  label="Válec1917"
  Angle = 360
  AttacherType = Attacher::AttachEngine3D
  Height = 3
  Placement = pos=(26,73,117) rot=(0,1,0;1.5708rad)
  Radius = 3
FEATURE [Part::Compound] Compound1009
  Links = -> [Cylinder1910,Cylinder1915,Cylinder1908,Cylinder1917]
  Placement = pos=(3,0,-3) rot=(0,0,1;0rad)
FEATURE [Part::Cylinder] Cylinder1918  label="Válec1918"
  Angle = 360
  AttacherType = Attacher::AttachEngine3D
  Height = 20
  Placement = pos=(20,71,49) rot=(0,1,0;1.5708rad)
  Radius = 1.5
FEATURE [Part::Cylinder] Cylinder1919  label="Válec1919"
  Angle = 360
  AttacherType = Attacher::AttachEngine3D
  Height = 60
  Placement = pos=(26,67,117) rot=(0,1,0;1.5708rad)
  Radius = 1.75
FEATURE [Part::Compound] Compound1007
  Links = -> [Cylinder1906,Cylinder1909,Cylinder1902,Cylinder1919]
  Placement = pos=(-72,0,-3) rot=(0,0,1;0rad)
FEATURE [Part::Box] Box824  label="Krychle824"
  AttacherType = Attacher::AttachEngine3D
  Height = 15
  Length = 15
  Placement = pos=(17,68,31) rot=(0,0,1;0rad)
  Width = 80
FEATURE [Part::Cylinder] Cylinder1920  label="Válec1920"
  Angle = 360
  AttacherType = Attacher::AttachEngine3D
  Height = 20
  Placement = pos=(20,71,28) rot=(0,1,0;1.5708rad)
  Radius = 1.5
FEATURE [Part::Box] Box825  label="Krychle825"
  AttacherType = Attacher::AttachEngine3D
  Height = 2
  Length = 6
  Placement = pos=(0,18,3) rot=(0,0,1;0rad)
  Width = 6
FEATURE [Part::Compound] Compound1004
  Links = -> [Box825,Box816,Box822,Box821]
  Placement = pos=(0,0,-100) rot=(0,0,1;0rad)
FEATURE [Part::Box] Box826  label="Krychle826"
  AttacherType = Attacher::AttachEngine3D
  Height = 6
  Length = 2
  Placement = pos=(34,64,0) rot=(0,0,1;0rad)
  Width = 6
FEATURE [Part::Compound] Compound1006
  Links = -> [Box811,Box826,Box815,Box810]
  Placement = pos=(-30,0,-3) rot=(0,0,1;0rad)
FEATURE [Part::Cylinder] Cylinder1921  label="Válec1921"
  Angle = 360
  AttacherType = Attacher::AttachEngine3D
  Height = 100
  Placement = pos=(26,7,3) rot=(0,1,0;1.5708rad)
  Radius = 1.75
FEATURE [Part::Compound] Compound1010
  Links = -> [Cylinder1921,Cylinder1913,Cylinder1911,Cylinder1907]
  Placement = pos=(-72,0,-3) rot=(0,0,1;0rad)
FEATURE [Part::Box] Box827  label="Krychle827"
  AttacherType = Attacher::AttachEngine3D
  Height = 6
  Length = 2
  Placement = pos=(26,80,46) rot=(0,0,1;0rad)
  Width = 6
FEATURE [Part::Box] Box828  label="Krychle828"
  AttacherType = Attacher::AttachEngine3D
  Height = 6
  Length = 2
  Placement = pos=(26,80,25) rot=(0,0,1;0rad)
  Width = 6
FEATURE [Part::Box] Box829  label="Krychle829"
  AttacherType = Attacher::AttachEngine3D
  Height = 6
  Length = 2
  Placement = pos=(26,68,25) rot=(0,0,1;0rad)
  Width = 6
FEATURE [Part::Cylinder] Cylinder1922  label="Válec1922"
  Angle = 360
  AttacherType = Attacher::AttachEngine3D
  Height = 3
  Placement = pos=(26,7,117) rot=(0,1,0;1.5708rad)
  Radius = 3
FEATURE [Part::Compound] Compound1011
  Links = -> [Cylinder1899,Cylinder1897,Cylinder1922,Cylinder1914]
  Placement = pos=(-26,0,-3) rot=(0,0,1;0rad)
FEATURE [Part::Box] Box830  label="Krychle830"
  AttacherType = Attacher::AttachEngine3D
  Height = 27
  Length = 19
  Placement = pos=(13,64,25) rot=(0,0,1;0rad)
  Width = 24
FEATURE [Part::Cut] Cut616
  Base = -> Box830
  Tool = -> Box824
FEATURE [Part::Cylinder] Cylinder1923  label="Válec1923"
  Angle = 360
  AttacherType = Attacher::AttachEngine3D
  Height = 3
  Placement = pos=(24.5,77,25) rot=(0,0,1;0rad)
  Radius = 4
FEATURE [Part::Cylinder] Cylinder1924  label="Válec1924"
  Angle = 360
  AttacherType = Attacher::AttachEngine3D
  Height = 20
  Placement = pos=(24.5,77,38) rot=(0,0,1;0rad)
  Radius = 2
FEATURE [Part::Cylinder] Cylinder1925  label="Válec1925"
  Angle = 360
  AttacherType = Attacher::AttachEngine3D
  Height = 20
  Placement = pos=(20,83,49) rot=(0,1,0;1.5708rad)
  Radius = 1.5
FEATURE [Part::Cylinder] Cylinder1926  label="Válec1926"
  Angle = 360
  AttacherType = Attacher::AttachEngine3D
  Height = 3
  Placement = pos=(24.5,77,49) rot=(0,0,1;0rad)
  Radius = 4
FEATURE [Part::Box] Box831  label="Krychle831"
  AttacherType = Attacher::AttachEngine3D
  Height = 27
  Length = 13
  Placement = pos=(0,64,25) rot=(0,0,1;0rad)
  Width = 24
FEATURE [Part::Chamfer] Chamfer064
  Base = -> Box831
  Edges = 1 edges r=12.9: [Edge3]
FEATURE [Part::Cylinder] Cylinder1927  label="Válec1927"
  Angle = 360
  AttacherType = Attacher::AttachEngine3D
  Height = 20
  Placement = pos=(20,83,28) rot=(0,1,0;1.5708rad)
  Radius = 1.5
FEATURE [Part::Compound] Compound1013
  Links = -> [Cylinder1920,Cylinder1927,Cylinder1918,Cylinder1925]
FEATURE [Part::Compound] Compound1014
  Links = -> [Box828,Box829,Box827,Box823]
  Placement = pos=(1,0,0) rot=(0,0,1;0rad)
FEATURE [Part::Cut] Cut610
  Base = -> Cut616
  Tool = -> Compound1014
FEATURE [Part::Cut] Cut608
  Base = -> Cut610
  Tool = -> Compound1013
FEATURE [Part::Cut] Cut609
  Base = -> Cut608
  Tool = -> Cylinder1916
FEATURE [Part::Cut] Cut614
  Base = -> Cut609
  Tool = -> Cylinder1923
FEATURE [Part::Compound] Compound1015
  Links = -> [Cylinder1905,Cylinder1900,Cylinder1895,Cylinder1912]
  Placement = pos=(0,0,-100) rot=(0,0,1;0rad)
FEATURE [Part::Cut] Cut620
  Base = -> Cut605
  Tool = -> Chamfer063
FEATURE [Part::Cut] Cut617
  Base = -> Cut620
  Tool = -> Compound1003
FEATURE [Part::Cut] Cut613
  Base = -> Cut617
  Tool = -> Box817
FEATURE [Part::Cut] Cut607
  Base = -> Cut613
  Tool = -> Cylinder1898
FEATURE [Part::Cut] Cut612
  Base = -> Cut607
  Tool = -> Compound1004
FEATURE [Part::Cut] Cut611
  Base = -> Cut612
  Tool = -> Compound1015
FEATURE [Part::Cut] Cut602
  Base = -> Cut611
  Tool = -> Compound1006
FEATURE [Part::Cut] Cut619
  Base = -> Cut602
  Tool = -> Compound1007
FEATURE [Part::Cut] Cut621
  Base = -> Cut619
  Tool = -> Compound1010
FEATURE [Part::Cut] Cut606
  Base = -> Cut621
  Tool = -> Compound1009
FEATURE [Part::Cut] Cut603
  Base = -> Cut606
  Tool = -> Compound1011
FEATURE [Part::Cut] Cut622
  Base = -> Cut614
  Tool = -> Cylinder1926
FEATURE [Part::Cut] Cut615
  Base = -> Cut622
  Tool = -> Cylinder1924
FEATURE [Part::Compound] Compound1012  label="Ele-box_small-extrusion001"
  Links = -> [Chamfer064,Cut615]
  Placement = pos=(32,16,77) rot=(0,1,0;3.14159rad)
FEATURE [Part::Cylinder] Cylinder1928  label="Válec1928"
  Angle = 360
  AttacherType = Attacher::AttachEngine3D
  Height = 10
  Placement = pos=(16,82,97) rot=(1,0,0;1.5708rad)
  Radius = 9
FEATURE [Part::Box] Box832  label="Krychle832"
  AttacherType = Attacher::AttachEngine3D
  Height = 4
  Length = 32
  Placement = pos=(0,4,32) rot=(0,0,1;0rad)
  Width = 60
FEATURE [Part::Cut] Cut623
  Base = -> Cut603
  Tool = -> Cylinder1928
FEATURE [Part::Box] Box833  label="Krychle833"
  AttacherType = Attacher::AttachEngine3D
  Height = 44
  Length = 32
  Placement = pos=(0,60,36) rot=(0,0,1;0rad)
  Width = 4
FEATURE [Part::Box] Box834  label="Krychle834"
  AttacherType = Attacher::AttachEngine3D
  Height = 4
  Length = 32
  Placement = pos=(0,60,80) rot=(0,0,1;0rad)
  Width = 16
FEATURE [Part::Compound] Compound1016  label="Ele-box_separator001"
  Links = -> [Box832,Box833,Box834]
FEATURE [Part::Chamfer] Chamfer065
  Base = -> Cut623
  Edges = 4 edges r=4: [Edge19,Edge22,Edge44,Edge48]
FEATURE [Part::Chamfer] Chamfer066
  Base = -> Compound1016
  Edges = 2 edges r=3: [Edge11,Edge34]
FEATURE [Part::Compound] Compound1017  label="Ele-box_standard001"
  Links = -> [Chamfer065,Chamfer066]
FEATURE [Part::Compound] Compound1018  label="Ele-box_small-hold-opposite"
  Links = -> [Compound1012,Compound1017]
FEATURE [Part::Cylinder] Cylinder975  label="Válec975"
  Angle = 360
  AttacherType = Attacher::AttachEngine3D
  Height = 20
  Placement = pos=(20,71,28) rot=(0,1,0;1.5708rad)
  Radius = 1.5
FEATURE [Part::Cylinder] Cylinder976  label="Válec976"
  Angle = 360
  AttacherType = Attacher::AttachEngine3D
  Height = 20
  Placement = pos=(20,83,28) rot=(0,1,0;1.5708rad)
  Radius = 1.5
FEATURE [Part::Cylinder] Cylinder977  label="Válec977"
  Angle = 360
  AttacherType = Attacher::AttachEngine3D
  Height = 20
  Placement = pos=(20,71,49) rot=(0,1,0;1.5708rad)
  Radius = 1.5
FEATURE [Part::Cylinder] Cylinder978  label="Válec978"
  Angle = 360
  AttacherType = Attacher::AttachEngine3D
  Height = 20
  Placement = pos=(20,83,49) rot=(0,1,0;1.5708rad)
  Radius = 1.5
FEATURE [Part::Compound] Compound1019
  Links = -> [Cylinder975,Cylinder976,Cylinder977,Cylinder978]
FEATURE [Part::Box] Box494  label="Krychle494"
  AttacherType = Attacher::AttachEngine3D
  Height = 27
  Length = 6
  Placement = pos=(32,64,25) rot=(0,0,1;0rad)
  Width = 24
FEATURE [Part::Cylinder] Cylinder987  label="Válec987"
  Angle = 360
  AttacherType = Attacher::AttachEngine3D
  Height = 3
  Placement = pos=(20,71,28) rot=(0,1,0;1.5708rad)
  Radius = 3
FEATURE [Part::Cylinder] Cylinder988  label="Válec988"
  Angle = 360
  AttacherType = Attacher::AttachEngine3D
  Height = 3
  Placement = pos=(20,83,28) rot=(0,1,0;1.5708rad)
  Radius = 3
FEATURE [Part::Cylinder] Cylinder989  label="Válec989"
  Angle = 360
  AttacherType = Attacher::AttachEngine3D
  Height = 3
  Placement = pos=(20,71,49) rot=(0,1,0;1.5708rad)
  Radius = 3
FEATURE [Part::Cylinder] Cylinder990  label="Válec990"
  Angle = 360
  AttacherType = Attacher::AttachEngine3D
  Height = 3
  Placement = pos=(20,83,49) rot=(0,1,0;1.5708rad)
  Radius = 3
FEATURE [Part::Compound] Compound528
  Links = -> [Cylinder987,Cylinder988,Cylinder989,Cylinder990]
  Placement = pos=(15,0,0) rot=(0,0,1;0rad)
FEATURE [Part::Cut] Cut457
  Base = -> Box494
  Tool = -> Compound1019
FEATURE [Part::Cut] Cut458  label="malo_kryt_elehold1"
  Base = -> Cut457
  Tool = -> Compound528
FEATURE [Part::Chamfer] Chamfer031  label="Ele-box_small-cover"
  Base = -> Cut458
  Edges = 1 edges r=4: [Edge10]
FEATURE [Part::Box] Box408  label="Krychle408"
  AttacherType = Attacher::AttachEngine3D
  Height = 32
  Length = 26
  Placement = pos=(0,64,-3) rot=(0,0,1;0rad)
  Width = 32
FEATURE [Part::Box] Box409  label="Krychle409"
  AttacherType = Attacher::AttachEngine3D
  Height = 20
  Length = 20
  Placement = pos=(6,64,3) rot=(0,0,1;0rad)
  Width = 64
FEATURE [Part::Cut] Cut381
  Base = -> Box408
  Tool = -> Box409
FEATURE [Part::Cylinder] Cylinder857  label="Válec857"
  Angle = 360
  AttacherType = Attacher::AttachEngine3D
  Height = 20
  Placement = pos=(16,80,14) rot=(0,0,1;0rad)
  Radius = 2.5
FEATURE [Part::Cut] Cut382
  Base = -> Cut381
  Tool = -> Cylinder857
FEATURE [Part::Cylinder] Cylinder858  label="Válec858"
  Angle = 360
  AttacherType = Attacher::AttachEngine3D
  Height = 20
  Placement = pos=(-6,80,13) rot=(0,1,0;1.5708rad)
  Radius = 2.5
FEATURE [Part::Cut] Cut383
  Base = -> Cut382
  Tool = -> Cylinder858
FEATURE [Part::Box] Box410  label="Krychle410"
  AttacherType = Attacher::AttachEngine3D
  Height = 6
  Length = 2
  Placement = pos=(20,68,-3) rot=(0,0,1;0rad)
  Width = 6
FEATURE [Part::Box] Box411  label="Krychle411"
  AttacherType = Attacher::AttachEngine3D
  Height = 6
  Length = 2
  Placement = pos=(20,86,-3) rot=(0,0,1;0rad)
  Width = 6
FEATURE [Part::Box] Box412  label="Krychle412"
  AttacherType = Attacher::AttachEngine3D
  Height = 6
  Length = 2
  Placement = pos=(20,68,23) rot=(0,0,1;0rad)
  Width = 6
FEATURE [Part::Box] Box413  label="Krychle413"
  AttacherType = Attacher::AttachEngine3D
  Height = 6
  Length = 2
  Placement = pos=(20,86,23) rot=(0,0,1;0rad)
  Width = 6
FEATURE [Part::Compound] Compound487
  Links = -> [Box410,Box411,Box412,Box413]
FEATURE [Part::Cylinder] Cylinder859  label="Válec859"
  Angle = 360
  AttacherType = Attacher::AttachEngine3D
  Height = 20
  Placement = pos=(8,71,0) rot=(0,1,0;1.5708rad)
  Radius = 1.5
FEATURE [Part::Cylinder] Cylinder860  label="Válec860"
  Angle = 360
  AttacherType = Attacher::AttachEngine3D
  Height = 20
  Placement = pos=(8,89,0) rot=(0,1,0;1.5708rad)
  Radius = 1.5
FEATURE [Part::Cylinder] Cylinder861  label="Válec861"
  Angle = 360
  AttacherType = Attacher::AttachEngine3D
  Height = 20
  Placement = pos=(8,71,26) rot=(0,1,0;1.5708rad)
  Radius = 1.5
FEATURE [Part::Cylinder] Cylinder862  label="Válec862"
  Angle = 360
  AttacherType = Attacher::AttachEngine3D
  Height = 20
  Placement = pos=(8,89,26) rot=(0,1,0;1.5708rad)
  Radius = 1.5
FEATURE [Part::Compound] Compound486
  Links = -> [Cylinder859,Cylinder860,Cylinder861,Cylinder862]
FEATURE [Part::Cut] Cut384
  Base = -> Cut383
  Tool = -> Compound486
FEATURE [Part::Cut] Cut385
  Base = -> Cut384
  Tool = -> Compound487
FEATURE [Part::Cylinder] Cylinder873  label="Válec873"
  Angle = 360
  AttacherType = Attacher::AttachEngine3D
  Height = 3
  Placement = pos=(0,80,13) rot=(0,1,0;1.5708rad)
  Radius = 5
FEATURE [Part::Cut] Cut390
  Base = -> Cut385
  Tool = -> Cylinder873
FEATURE [Part::Cylinder] Cylinder874  label="Válec874"
  Angle = 360
  AttacherType = Attacher::AttachEngine3D
  Height = 3
  Placement = pos=(16,80,26) rot=(0,0,1;0rad)
  Radius = 5
FEATURE [Part::Cut] Cut391
  Base = -> Cut390
  Tool = -> Cylinder874
FEATURE [Part::Chamfer] Chamfer023  label="Ele-box_big_extrusion"
  Base = -> Cut391
  Edges = 2 edges r=2: [Edge13,Edge24]
  Placement = pos=(0,16,0) rot=(0,0,1;0rad)
FEATURE [Part::Cylinder] Cylinder1929  label="Válec1929"
  Angle = 360
  AttacherType = Attacher::AttachEngine3D
  Height = 10
  Placement = pos=(29,6,39) rot=(1,0,0;1.5708rad)
  Radius = 1.5
FEATURE [Part::Box] Box835  label="Krychle835"
  AttacherType = Attacher::AttachEngine3D
  Height = 6
  Length = 2
  Placement = pos=(34,70,0) rot=(0,0,1;0rad)
  Width = 6
FEATURE [Part::Cylinder] Cylinder1930  label="Válec1930"
  Angle = 360
  AttacherType = Attacher::AttachEngine3D
  Height = 60
  Placement = pos=(26,13,117) rot=(0,1,0;1.5708rad)
  Radius = 1.75
FEATURE [Part::Box] Box836  label="Krychle836"
  AttacherType = Attacher::AttachEngine3D
  Height = 6
  Length = 2
  Placement = pos=(34,70,114) rot=(0,0,1;0rad)
  Width = 6
FEATURE [Part::Box] Box837  label="Krychle837"
  AttacherType = Attacher::AttachEngine3D
  Height = 6
  Length = 2
  Placement = pos=(34,4,0) rot=(0,0,1;0rad)
  Width = 6
FEATURE [Part::Cylinder] Cylinder1931  label="Válec1931"
  Angle = 360
  AttacherType = Attacher::AttachEngine3D
  Height = 10
  Placement = pos=(16,82,66) rot=(1,0,0;1.5708rad)
  Radius = 9
FEATURE [Part::Box] Box838  label="Krychle838"
  AttacherType = Attacher::AttachEngine3D
  Height = 6
  Length = 2
  Placement = pos=(34,4,0) rot=(0,0,1;0rad)
  Width = 6
FEATURE [Part::Box] Box839  label="Krychle839"
  AttacherType = Attacher::AttachEngine3D
  Height = 6
  Length = 2
  Placement = pos=(34,4,114) rot=(0,0,1;0rad)
  Width = 6
FEATURE [Part::Cylinder] Cylinder1932  label="Válec1932"
  Angle = 360
  AttacherType = Attacher::AttachEngine3D
  Height = 10
  Placement = pos=(29,21,0) rot=(0,0,1;0rad)
  Radius = 1.5
FEATURE [Part::Cylinder] Cylinder1933  label="Válec1933"
  Angle = 360
  AttacherType = Attacher::AttachEngine3D
  Height = 60
  Placement = pos=(26,13,3) rot=(0,1,0;1.5708rad)
  Radius = 1.75
FEATURE [Part::Box] Box840  label="Krychle840"
  AttacherType = Attacher::AttachEngine3D
  Height = 108
  Length = 30
  Placement = pos=(2,4,3) rot=(0,0,1;0rad)
  Width = 72
FEATURE [Part::Box] Box841  label="Krychle841"
  AttacherType = Attacher::AttachEngine3D
  Height = 6
  Length = 2
  Placement = pos=(34,4,114) rot=(0,0,1;0rad)
  Width = 6
FEATURE [Part::Box] Box842  label="Krychle842"
  AttacherType = Attacher::AttachEngine3D
  Height = 2
  Length = 6
  Placement = pos=(0,40,3) rot=(0,0,1;0rad)
  Width = 6
FEATURE [Part::Box] Box843  label="Krychle843"
  AttacherType = Attacher::AttachEngine3D
  Height = 3
  Length = 8
  Placement = pos=(12,-2,39) rot=(0,0,1;0rad)
  Width = 10
FEATURE [Part::Cylinder] Cylinder1934  label="Válec1934"
  Angle = 360
  AttacherType = Attacher::AttachEngine3D
  Height = 3
  Placement = pos=(26,67,3) rot=(0,1,0;1.5708rad)
  Radius = 3
FEATURE [Part::Cylinder] Cylinder1935  label="Válec1935"
  Angle = 360
  AttacherType = Attacher::AttachEngine3D
  Height = 10
  Placement = pos=(16,6,18) rot=(1,0,0;1.5708rad)
  Radius = 8
FEATURE [Part::Cylinder] Cylinder1936  label="Válec1936"
  Angle = 360
  AttacherType = Attacher::AttachEngine3D
  Height = 3
  Placement = pos=(26,13,3) rot=(0,1,0;1.5708rad)
  Radius = 3
FEATURE [Part::Cylinder] Cylinder1937  label="Válec1937"
  Angle = 360
  AttacherType = Attacher::AttachEngine3D
  Height = 10
  Placement = pos=(3,43,0) rot=(0,0,1;0rad)
  Radius = 1.5
FEATURE [Part::Box] Box844  label="Krychle844"
  AttacherType = Attacher::AttachEngine3D
  Height = 21
  Length = 17.5
  Placement = pos=(10.75,-2,42) rot=(0,0,1;0rad)
  Width = 10
FEATURE [Part::Chamfer] Chamfer067
  Base = -> Box844
  Edges = 1 edges r=3: [Edge2]
  Placement = pos=(-4,0,0) rot=(0,0,1;0rad)
FEATURE [Part::Cylinder] Cylinder1938  label="Válec1938"
  Angle = 360
  AttacherType = Attacher::AttachEngine3D
  Height = 60
  Placement = pos=(26,67,3) rot=(0,1,0;1.5708rad)
  Radius = 1.75
FEATURE [Part::Cylinder] Cylinder1939  label="Válec1939"
  Angle = 360
  AttacherType = Attacher::AttachEngine3D
  Height = 60
  Placement = pos=(26,7,117) rot=(0,1,0;1.5708rad)
  Radius = 1.75
FEATURE [Part::Box] Box845  label="Krychle845"
  AttacherType = Attacher::AttachEngine3D
  Height = 6
  Length = 2
  Placement = pos=(34,70,114) rot=(0,0,1;0rad)
  Width = 6
FEATURE [Part::Compound] Compound1025
  Links = -> [Box838,Box835,Box839,Box845]
  Placement = pos=(-8,0,-3) rot=(0,0,1;0rad)
FEATURE [Part::Box] Box846  label="Krychle846"
  AttacherType = Attacher::AttachEngine3D
  Height = 120
  Length = 32
  Placement = pos=(0,0,-3) rot=(0,0,1;0rad)
  Width = 80
FEATURE [Part::Cut] Cut624
  Base = -> Box846
  Tool = -> Box840
FEATURE [Part::Cut] Cut630
  Base = -> Cut624
  Tool = -> Compound1025
FEATURE [Part::Cylinder] Cylinder1940  label="Válec1940"
  Angle = 360
  AttacherType = Attacher::AttachEngine3D
  Height = 60
  Placement = pos=(26,67,117) rot=(0,1,0;1.5708rad)
  Radius = 1.75
FEATURE [Part::Compound] Compound1022
  Links = -> [Cylinder1933,Cylinder1938,Cylinder1930,Cylinder1940]
  Placement = pos=(-8,0,-3) rot=(0,0,1;0rad)
FEATURE [Part::Cut] Cut632
  Base = -> Cut630
  Tool = -> Compound1022
FEATURE [Part::Cut] Cut633
  Base = -> Cut632
  Tool = -> Cylinder1931
FEATURE [Part::Box] Box847  label="Krychle847"
  AttacherType = Attacher::AttachEngine3D
  Height = 2
  Length = 6
  Placement = pos=(26,18,3) rot=(0,0,1;0rad)
  Width = 6
FEATURE [Part::Cylinder] Cylinder1941  label="Válec1941"
  Angle = 360
  AttacherType = Attacher::AttachEngine3D
  Height = 10
  Placement = pos=(10,6,63) rot=(1,0,0;1.5708rad)
  Radius = 1.5
FEATURE [Part::Compound] Compound1020
  Links = -> [Cylinder1941,Cylinder1929]
  Placement = pos=(-4,0,0) rot=(0,0,1;0rad)
FEATURE [Part::Cylinder] Cylinder1942  label="Válec1942"
  Angle = 360
  AttacherType = Attacher::AttachEngine3D
  Height = 10
  Placement = pos=(3,21,0) rot=(0,0,1;0rad)
  Radius = 1.5
FEATURE [Part::Cylinder] Cylinder1943  label="Válec1943"
  Angle = 360
  AttacherType = Attacher::AttachEngine3D
  Height = 60
  Placement = pos=(26,7,3) rot=(0,1,0;1.5708rad)
  Radius = 1.75
FEATURE [Part::Box] Box848  label="Krychle848"
  AttacherType = Attacher::AttachEngine3D
  Height = 2
  Length = 6
  Placement = pos=(26,40,3) rot=(0,0,1;0rad)
  Width = 6
FEATURE [Part::Cylinder] Cylinder1944  label="Válec1944"
  Angle = 360
  AttacherType = Attacher::AttachEngine3D
  Height = 100
  Placement = pos=(26,67,117) rot=(0,1,0;1.5708rad)
  Radius = 1.75
FEATURE [Part::Cylinder] Cylinder1945  label="Válec1945"
  Angle = 360
  AttacherType = Attacher::AttachEngine3D
  Height = 3
  Placement = pos=(26,13,117) rot=(0,1,0;1.5708rad)
  Radius = 3
FEATURE [Part::Cylinder] Cylinder1946  label="Válec1946"
  Angle = 360
  AttacherType = Attacher::AttachEngine3D
  Height = 60
  Placement = pos=(26,73,3) rot=(0,1,0;1.5708rad)
  Radius = 1.75
FEATURE [Part::Cylinder] Cylinder1947  label="Válec1947"
  Angle = 360
  AttacherType = Attacher::AttachEngine3D
  Height = 3
  Placement = pos=(26,13,3) rot=(0,1,0;1.5708rad)
  Radius = 3
FEATURE [Part::Cylinder] Cylinder1948  label="Válec1948"
  Angle = 360
  AttacherType = Attacher::AttachEngine3D
  Height = 100
  Placement = pos=(26,13,117) rot=(0,1,0;1.5708rad)
  Radius = 1.75
FEATURE [Part::Cylinder] Cylinder1949  label="Válec1949"
  Angle = 360
  AttacherType = Attacher::AttachEngine3D
  Height = 10
  Placement = pos=(29,43,0) rot=(0,0,1;0rad)
  Radius = 1.5
FEATURE [Part::Compound] Compound1029
  Links = -> [Cylinder1942,Cylinder1937,Cylinder1932,Cylinder1949]
  Placement = pos=(0,0,-100) rot=(0,0,1;0rad)
FEATURE [Part::Cylinder] Cylinder1950  label="Válec1950"
  Angle = 360
  AttacherType = Attacher::AttachEngine3D
  Height = 100
  Placement = pos=(26,67,3) rot=(0,1,0;1.5708rad)
  Radius = 1.75
FEATURE [Part::Cylinder] Cylinder1951  label="Válec1951"
  Angle = 360
  AttacherType = Attacher::AttachEngine3D
  Height = 3
  Placement = pos=(26,67,117) rot=(0,1,0;1.5708rad)
  Radius = 3
FEATURE [Part::Cylinder] Cylinder1952  label="Válec1952"
  Angle = 360
  AttacherType = Attacher::AttachEngine3D
  Height = 3
  Placement = pos=(26,67,3) rot=(0,1,0;1.5708rad)
  Radius = 3
FEATURE [Part::Cylinder] Cylinder1953  label="Válec1953"
  Angle = 360
  AttacherType = Attacher::AttachEngine3D
  Height = 3
  Placement = pos=(26,67,117) rot=(0,1,0;1.5708rad)
  Radius = 3
FEATURE [Part::Compound] Compound1026
  Links = -> [Cylinder1947,Cylinder1952,Cylinder1945,Cylinder1953]
  Placement = pos=(3,0,-3) rot=(0,0,1;0rad)
FEATURE [Part::Cylinder] Cylinder1954  label="Válec1954"
  Angle = 360
  AttacherType = Attacher::AttachEngine3D
  Height = 60
  Placement = pos=(26,73,117) rot=(0,1,0;1.5708rad)
  Radius = 1.75
FEATURE [Part::Compound] Compound1024
  Links = -> [Cylinder1943,Cylinder1946,Cylinder1939,Cylinder1954]
  Placement = pos=(-44,0,-3) rot=(0,0,1;0rad)
FEATURE [Part::Box] Box849  label="Krychle849"
  AttacherType = Attacher::AttachEngine3D
  Height = 2
  Length = 6
  Placement = pos=(0,18,3) rot=(0,0,1;0rad)
  Width = 6
FEATURE [Part::Compound] Compound1021
  Links = -> [Box849,Box842,Box848,Box847]
  Placement = pos=(0,0,-100) rot=(0,0,1;0rad)
FEATURE [Part::Box] Box850  label="Krychle850"
  AttacherType = Attacher::AttachEngine3D
  Height = 6
  Length = 2
  Placement = pos=(34,70,0) rot=(0,0,1;0rad)
  Width = 6
FEATURE [Part::Compound] Compound1023
  Links = -> [Box837,Box850,Box841,Box836]
  Placement = pos=(-30,0,-3) rot=(0,0,1;0rad)
FEATURE [Part::Cut] Cut637
  Base = -> Cut633
  Tool = -> Chamfer067
FEATURE [Part::Cut] Cut629
  Base = -> Cut637
  Tool = -> Compound1020
FEATURE [Part::Cut] Cut628
  Base = -> Cut629
  Tool = -> Box843
FEATURE [Part::Cut] Cut635
  Base = -> Cut628
  Tool = -> Cylinder1935
FEATURE [Part::Cut] Cut627
  Base = -> Cut635
  Tool = -> Compound1021
FEATURE [Part::Cut] Cut626
  Base = -> Cut627
  Tool = -> Compound1029
FEATURE [Part::Cut] Cut625
  Base = -> Cut626
  Tool = -> Compound1023
FEATURE [Part::Cut] Cut636
  Base = -> Cut625
  Tool = -> Compound1024
FEATURE [Part::Cylinder] Cylinder1955  label="Válec1955"
  Angle = 360
  AttacherType = Attacher::AttachEngine3D
  Height = 100
  Placement = pos=(26,13,3) rot=(0,1,0;1.5708rad)
  Radius = 1.75
FEATURE [Part::Compound] Compound1027
  Links = -> [Cylinder1955,Cylinder1950,Cylinder1948,Cylinder1944]
  Placement = pos=(-72,0,-3) rot=(0,0,1;0rad)
FEATURE [Part::Cut] Cut638
  Base = -> Cut636
  Tool = -> Compound1027
FEATURE [Part::Cut] Cut634
  Base = -> Cut638
  Tool = -> Compound1026
FEATURE [Part::Cylinder] Cylinder1956  label="Válec1956"
  Angle = 360
  AttacherType = Attacher::AttachEngine3D
  Height = 3
  Placement = pos=(26,13,117) rot=(0,1,0;1.5708rad)
  Radius = 3
FEATURE [Part::Compound] Compound1028
  Links = -> [Cylinder1936,Cylinder1934,Cylinder1956,Cylinder1951]
  Placement = pos=(-26,0,-3) rot=(0,0,1;0rad)
FEATURE [Part::Cut] Cut631
  Base = -> Cut634
  Tool = -> Compound1028
FEATURE [Part::Cylinder] Cylinder1957  label="Válec1957"
  Angle = 360
  AttacherType = Attacher::AttachEngine3D
  Height = 10
  Placement = pos=(16,82,97) rot=(1,0,0;1.5708rad)
  Radius = 9
FEATURE [Part::Cut] Cut639
  Base = -> Cut631
  Tool = -> Cylinder1957
FEATURE [Part::Box] Box851  label="Krychle851"
  AttacherType = Attacher::AttachEngine3D
  Height = 4
  Length = 32
  Placement = pos=(0,4,32) rot=(0,0,1;0rad)
  Width = 60
FEATURE [Part::Box] Box852  label="Krychle852"
  AttacherType = Attacher::AttachEngine3D
  Height = 44
  Length = 32
  Placement = pos=(0,60,36) rot=(0,0,1;0rad)
  Width = 4
FEATURE [Part::Box] Box853  label="Krychle853"
  AttacherType = Attacher::AttachEngine3D
  Height = 4
  Length = 32
  Placement = pos=(0,60,80) rot=(0,0,1;0rad)
  Width = 16
FEATURE [Part::Compound] Compound1030  label="Ele-box_separator002"
  Links = -> [Box851,Box852,Box853]
FEATURE [Part::Chamfer] Chamfer068
  Base = -> Compound1030
  Edges = 2 edges r=3: [Edge11,Edge34]
FEATURE [Part::Chamfer] Chamfer069  label="Ele-box_anti-standard"
  Base = -> Cut639
  Edges = 3 edges r=3.99: [Edge19,Edge22,Edge48]
FEATURE [Part::Compound] Compound1031  label="Ele-box_big-hold"
  Links = -> [Chamfer068,Chamfer023,Chamfer069]
FEATURE [Part::Cylinder] Cylinder863  label="Válec863"
  Angle = 360
  AttacherType = Attacher::AttachEngine3D
  Height = 20
  Placement = pos=(8,89,0) rot=(0,1,0;1.5708rad)
  Radius = 1.5
FEATURE [Part::Cylinder] Cylinder864  label="Válec864"
  Angle = 360
  AttacherType = Attacher::AttachEngine3D
  Height = 20
  Placement = pos=(8,89,26) rot=(0,1,0;1.5708rad)
  Radius = 1.5
FEATURE [Part::Cylinder] Cylinder865  label="Válec865"
  Angle = 360
  AttacherType = Attacher::AttachEngine3D
  Height = 20
  Placement = pos=(8,71,0) rot=(0,1,0;1.5708rad)
  Radius = 1.5
FEATURE [Part::Cylinder] Cylinder866  label="Válec866"
  Angle = 360
  AttacherType = Attacher::AttachEngine3D
  Height = 20
  Placement = pos=(8,71,26) rot=(0,1,0;1.5708rad)
  Radius = 1.5
FEATURE [Part::Box] Box414  label="Krychle414"
  AttacherType = Attacher::AttachEngine3D
  Height = 32
  Length = 6
  Placement = pos=(26,64,-3) rot=(0,0,1;0rad)
  Width = 32
FEATURE [Part::Cylinder] Cylinder867  label="Válec867"
  Angle = 360
  AttacherType = Attacher::AttachEngine3D
  Height = 3
  Placement = pos=(8,89,0) rot=(0,1,0;1.5708rad)
  Radius = 3
FEATURE [Part::Cylinder] Cylinder868  label="Válec868"
  Angle = 360
  AttacherType = Attacher::AttachEngine3D
  Height = 3
  Placement = pos=(8,71,26) rot=(0,1,0;1.5708rad)
  Radius = 3
FEATURE [Part::Cylinder] Cylinder869  label="Válec869"
  Angle = 360
  AttacherType = Attacher::AttachEngine3D
  Height = 3
  Placement = pos=(8,89,26) rot=(0,1,0;1.5708rad)
  Radius = 3
FEATURE [Part::Cylinder] Cylinder870  label="Válec870"
  Angle = 360
  AttacherType = Attacher::AttachEngine3D
  Height = 3
  Placement = pos=(8,71,0) rot=(0,1,0;1.5708rad)
  Radius = 3
FEATURE [Part::Cylinder] Cylinder871  label="Válec871"
  Angle = 360
  AttacherType = Attacher::AttachEngine3D
  Height = 20
  Placement = pos=(19,80,13) rot=(0,1,0;1.5708rad)
  Radius = 2.5
FEATURE [Part::Cylinder] Cylinder872  label="Válec872"
  Angle = 360
  AttacherType = Attacher::AttachEngine3D
  Height = 3
  Placement = pos=(29,80,13) rot=(0,1,0;1.5708rad)
  Radius = 5
FEATURE [Part::Compound] Compound488
  Links = -> [Cylinder865,Cylinder863,Cylinder866,Cylinder864]
  Placement = pos=(10,0,0) rot=(0,0,1;0rad)
FEATURE [Part::Cut] Cut386
  Base = -> Box414
  Tool = -> Compound488
FEATURE [Part::Compound] Compound489
  Links = -> [Cylinder870,Cylinder867,Cylinder868,Cylinder869]
  Placement = pos=(21,0,0) rot=(0,0,1;0rad)
FEATURE [Part::Cut] Cut387  label="ele_reinfor_cover1"
  Base = -> Cut386
  Tool = -> Compound489
FEATURE [Part::Cut] Cut388
  Base = -> Cut387
  Tool = -> Cylinder871
FEATURE [Part::Cut] Cut389
  Base = -> Cut388
  Tool = -> Cylinder872
FEATURE [Part::Chamfer] Chamfer024  label="Ele-box_big-cover"
  Base = -> Cut389
  Edges = 2 edges r=2: [Edge13,Edge19]
  Placement = pos=(0,16,0) rot=(0,0,1;0rad)
FEATURE [Part::Box] Box854  label="Krychle854"
  AttacherType = Attacher::AttachEngine3D
  Height = 6
  Length = 2
  Placement = pos=(34,4,0) rot=(0,0,1;0rad)
  Width = 6
FEATURE [Part::Box] Box855  label="Krychle855"
  AttacherType = Attacher::AttachEngine3D
  Height = 6
  Length = 2
  Placement = pos=(34,70,114) rot=(0,0,1;0rad)
  Width = 6
FEATURE [Part::Cylinder] Cylinder1958  label="Válec1958"
  Angle = 360
  AttacherType = Attacher::AttachEngine3D
  Height = 60
  Placement = pos=(26,13,117) rot=(0,1,0;1.5708rad)
  Radius = 1.75
FEATURE [Part::Box] Box856  label="Krychle856"
  AttacherType = Attacher::AttachEngine3D
  Height = 6
  Length = 2
  Placement = pos=(34,70,0) rot=(0,0,1;0rad)
  Width = 6
FEATURE [Part::Cylinder] Cylinder1959  label="Válec1959"
  Angle = 360
  AttacherType = Attacher::AttachEngine3D
  Height = 10
  Placement = pos=(29,6,39) rot=(1,0,0;1.5708rad)
  Radius = 1.5
FEATURE [Part::Cylinder] Cylinder1960  label="Válec1960"
  Angle = 360
  AttacherType = Attacher::AttachEngine3D
  Height = 10
  Placement = pos=(16,82,66) rot=(1,0,0;1.5708rad)
  Radius = 9
FEATURE [Part::Box] Box857  label="Krychle857"
  AttacherType = Attacher::AttachEngine3D
  Height = 6
  Length = 2
  Placement = pos=(34,4,0) rot=(0,0,1;0rad)
  Width = 6
FEATURE [Part::Box] Box858  label="Krychle858"
  AttacherType = Attacher::AttachEngine3D
  Height = 6
  Length = 2
  Placement = pos=(34,4,114) rot=(0,0,1;0rad)
  Width = 6
FEATURE [Part::Cylinder] Cylinder1961  label="Válec1961"
  Angle = 360
  AttacherType = Attacher::AttachEngine3D
  Height = 10
  Placement = pos=(29,21,0) rot=(0,0,1;0rad)
  Radius = 1.5
FEATURE [Part::Cylinder] Cylinder1962  label="Válec1962"
  Angle = 360
  AttacherType = Attacher::AttachEngine3D
  Height = 60
  Placement = pos=(26,13,3) rot=(0,1,0;1.5708rad)
  Radius = 1.75
FEATURE [Part::Box] Box859  label="Krychle859"
  AttacherType = Attacher::AttachEngine3D
  Height = 108
  Length = 30
  Placement = pos=(2,4,3) rot=(0,0,1;0rad)
  Width = 72
FEATURE [Part::Box] Box860  label="Krychle860"
  AttacherType = Attacher::AttachEngine3D
  Height = 6
  Length = 2
  Placement = pos=(34,4,114) rot=(0,0,1;0rad)
  Width = 6
FEATURE [Part::Box] Box861  label="Krychle861"
  AttacherType = Attacher::AttachEngine3D
  Height = 2
  Length = 6
  Placement = pos=(0,40,3) rot=(0,0,1;0rad)
  Width = 6
FEATURE [Part::Box] Box862  label="Krychle862"
  AttacherType = Attacher::AttachEngine3D
  Height = 3
  Length = 8
  Placement = pos=(12,-2,39) rot=(0,0,1;0rad)
  Width = 10
FEATURE [Part::Cylinder] Cylinder1963  label="Válec1963"
  Angle = 360
  AttacherType = Attacher::AttachEngine3D
  Height = 3
  Placement = pos=(26,67,3) rot=(0,1,0;1.5708rad)
  Radius = 3
FEATURE [Part::Cylinder] Cylinder1964  label="Válec1964"
  Angle = 360
  AttacherType = Attacher::AttachEngine3D
  Height = 10
  Placement = pos=(16,6,18) rot=(1,0,0;1.5708rad)
  Radius = 8
FEATURE [Part::Cylinder] Cylinder1965  label="Válec1965"
  Angle = 360
  AttacherType = Attacher::AttachEngine3D
  Height = 3
  Placement = pos=(26,13,3) rot=(0,1,0;1.5708rad)
  Radius = 3
FEATURE [Part::Cylinder] Cylinder1966  label="Válec1966"
  Angle = 360
  AttacherType = Attacher::AttachEngine3D
  Height = 10
  Placement = pos=(3,43,0) rot=(0,0,1;0rad)
  Radius = 1.5
FEATURE [Part::Box] Box863  label="Krychle863"
  AttacherType = Attacher::AttachEngine3D
  Height = 21
  Length = 17.5
  Placement = pos=(10.75,-2,42) rot=(0,0,1;0rad)
  Width = 10
FEATURE [Part::Cylinder] Cylinder1967  label="Válec1967"
  Angle = 360
  AttacherType = Attacher::AttachEngine3D
  Height = 60
  Placement = pos=(26,67,3) rot=(0,1,0;1.5708rad)
  Radius = 1.75
FEATURE [Part::Cylinder] Cylinder1968  label="Válec1968"
  Angle = 360
  AttacherType = Attacher::AttachEngine3D
  Height = 60
  Placement = pos=(26,7,117) rot=(0,1,0;1.5708rad)
  Radius = 1.75
FEATURE [Part::Box] Box864  label="Krychle864"
  AttacherType = Attacher::AttachEngine3D
  Height = 6
  Length = 2
  Placement = pos=(34,70,114) rot=(0,0,1;0rad)
  Width = 6
FEATURE [Part::Box] Box865  label="Krychle865"
  AttacherType = Attacher::AttachEngine3D
  Height = 120
  Length = 32
  Placement = pos=(0,0,-3) rot=(0,0,1;0rad)
  Width = 80
FEATURE [Part::Cylinder] Cylinder1969  label="Válec1969"
  Angle = 360
  AttacherType = Attacher::AttachEngine3D
  Height = 60
  Placement = pos=(26,67,117) rot=(0,1,0;1.5708rad)
  Radius = 1.75
FEATURE [Part::Box] Box866  label="Krychle866"
  AttacherType = Attacher::AttachEngine3D
  Height = 2
  Length = 6
  Placement = pos=(26,18,3) rot=(0,0,1;0rad)
  Width = 6
FEATURE [Part::Cylinder] Cylinder1970  label="Válec1970"
  Angle = 360
  AttacherType = Attacher::AttachEngine3D
  Height = 10
  Placement = pos=(10,6,63) rot=(1,0,0;1.5708rad)
  Radius = 1.5
FEATURE [Part::Cylinder] Cylinder1971  label="Válec1971"
  Angle = 360
  AttacherType = Attacher::AttachEngine3D
  Height = 10
  Placement = pos=(3,21,0) rot=(0,0,1;0rad)
  Radius = 1.5
FEATURE [Part::Cylinder] Cylinder1972  label="Válec1972"
  Angle = 360
  AttacherType = Attacher::AttachEngine3D
  Height = 60
  Placement = pos=(26,7,3) rot=(0,1,0;1.5708rad)
  Radius = 1.75
FEATURE [Part::Box] Box867  label="Krychle867"
  AttacherType = Attacher::AttachEngine3D
  Height = 2
  Length = 6
  Placement = pos=(26,40,3) rot=(0,0,1;0rad)
  Width = 6
FEATURE [Part::Cylinder] Cylinder1973  label="Válec1973"
  Angle = 360
  AttacherType = Attacher::AttachEngine3D
  Height = 100
  Placement = pos=(26,67,117) rot=(0,1,0;1.5708rad)
  Radius = 1.75
FEATURE [Part::Cylinder] Cylinder1974  label="Válec1974"
  Angle = 360
  AttacherType = Attacher::AttachEngine3D
  Height = 3
  Placement = pos=(26,13,117) rot=(0,1,0;1.5708rad)
  Radius = 3
FEATURE [Part::Cylinder] Cylinder1975  label="Válec1975"
  Angle = 360
  AttacherType = Attacher::AttachEngine3D
  Height = 60
  Placement = pos=(26,73,3) rot=(0,1,0;1.5708rad)
  Radius = 1.75
FEATURE [Part::Cylinder] Cylinder1976  label="Válec1976"
  Angle = 360
  AttacherType = Attacher::AttachEngine3D
  Height = 3
  Placement = pos=(26,13,3) rot=(0,1,0;1.5708rad)
  Radius = 3
FEATURE [Part::Cylinder] Cylinder1977  label="Válec1977"
  Angle = 360
  AttacherType = Attacher::AttachEngine3D
  Height = 100
  Placement = pos=(26,13,117) rot=(0,1,0;1.5708rad)
  Radius = 1.75
FEATURE [Part::Cylinder] Cylinder1978  label="Válec1978"
  Angle = 360
  AttacherType = Attacher::AttachEngine3D
  Height = 10
  Placement = pos=(29,43,0) rot=(0,0,1;0rad)
  Radius = 1.5
FEATURE [Part::Cylinder] Cylinder1979  label="Válec1979"
  Angle = 360
  AttacherType = Attacher::AttachEngine3D
  Height = 100
  Placement = pos=(26,67,3) rot=(0,1,0;1.5708rad)
  Radius = 1.75
FEATURE [Part::Cylinder] Cylinder1980  label="Válec1980"
  Angle = 360
  AttacherType = Attacher::AttachEngine3D
  Height = 3
  Placement = pos=(26,67,117) rot=(0,1,0;1.5708rad)
  Radius = 3
FEATURE [Part::Cylinder] Cylinder1981  label="Válec1981"
  Angle = 360
  AttacherType = Attacher::AttachEngine3D
  Height = 3
  Placement = pos=(26,67,3) rot=(0,1,0;1.5708rad)
  Radius = 3
FEATURE [Part::Cylinder] Cylinder1982  label="Válec1982"
  Angle = 360
  AttacherType = Attacher::AttachEngine3D
  Height = 3
  Placement = pos=(26,67,117) rot=(0,1,0;1.5708rad)
  Radius = 3
FEATURE [Part::Cylinder] Cylinder1983  label="Válec1983"
  Angle = 360
  AttacherType = Attacher::AttachEngine3D
  Height = 60
  Placement = pos=(26,73,117) rot=(0,1,0;1.5708rad)
  Radius = 1.75
FEATURE [Part::Box] Box868  label="Krychle868"
  AttacherType = Attacher::AttachEngine3D
  Height = 2
  Length = 6
  Placement = pos=(0,18,3) rot=(0,0,1;0rad)
  Width = 6
FEATURE [Part::Box] Box869  label="Krychle869"
  AttacherType = Attacher::AttachEngine3D
  Height = 6
  Length = 2
  Placement = pos=(34,70,0) rot=(0,0,1;0rad)
  Width = 6
FEATURE [Part::Cylinder] Cylinder1984  label="Válec1984"
  Angle = 360
  AttacherType = Attacher::AttachEngine3D
  Height = 100
  Placement = pos=(26,13,3) rot=(0,1,0;1.5708rad)
  Radius = 1.75
FEATURE [Part::Cylinder] Cylinder1985  label="Válec1985"
  Angle = 360
  AttacherType = Attacher::AttachEngine3D
  Height = 3
  Placement = pos=(26,13,117) rot=(0,1,0;1.5708rad)
  Radius = 3
FEATURE [Part::Cylinder] Cylinder1986  label="Válec1986"
  Angle = 360
  AttacherType = Attacher::AttachEngine3D
  Height = 10
  Placement = pos=(16,82,97) rot=(1,0,0;1.5708rad)
  Radius = 9
FEATURE [Part::Compound] Compound1032
  Links = -> [Cylinder1970,Cylinder1959]
  Placement = pos=(-4,0,0) rot=(0,0,1;0rad)
FEATURE [Part::Compound] Compound1033
  Links = -> [Box868,Box861,Box867,Box866]
  Placement = pos=(0,0,-100) rot=(0,0,1;0rad)
FEATURE [Part::Compound] Compound1034
  Links = -> [Cylinder1962,Cylinder1967,Cylinder1958,Cylinder1969]
  Placement = pos=(-8,0,-3) rot=(0,0,1;0rad)
FEATURE [Part::Compound] Compound1035
  Links = -> [Box854,Box869,Box860,Box855]
  Placement = pos=(-30,0,-3) rot=(0,0,1;0rad)
FEATURE [Part::Compound] Compound1036
  Links = -> [Cylinder1972,Cylinder1975,Cylinder1968,Cylinder1983]
  Placement = pos=(-44,0,-3) rot=(0,0,1;0rad)
FEATURE [Part::Compound] Compound1037
  Links = -> [Box857,Box856,Box858,Box864]
  Placement = pos=(-8,0,-3) rot=(0,0,1;0rad)
FEATURE [Part::Compound] Compound1038
  Links = -> [Cylinder1976,Cylinder1981,Cylinder1974,Cylinder1982]
  Placement = pos=(3,0,-3) rot=(0,0,1;0rad)
FEATURE [Part::Compound] Compound1039
  Links = -> [Cylinder1984,Cylinder1979,Cylinder1977,Cylinder1973]
  Placement = pos=(-72,0,-3) rot=(0,0,1;0rad)
FEATURE [Part::Compound] Compound1040
  Links = -> [Cylinder1965,Cylinder1963,Cylinder1985,Cylinder1980]
  Placement = pos=(-26,0,-3) rot=(0,0,1;0rad)
FEATURE [Part::Chamfer] Chamfer070
  Base = -> Box863
  Edges = 1 edges r=3: [Edge2]
  Placement = pos=(-4,0,0) rot=(0,0,1;0rad)
FEATURE [Part::Compound] Compound1041
  Links = -> [Cylinder1971,Cylinder1966,Cylinder1961,Cylinder1978]
  Placement = pos=(0,0,-100) rot=(0,0,1;0rad)
FEATURE [Part::Cut] Cut649
  Base = -> Box865
  Tool = -> Box859
FEATURE [Part::Cut] Cut652
  Base = -> Cut649
  Tool = -> Compound1037
FEATURE [Part::Cut] Cut646
  Base = -> Cut652
  Tool = -> Compound1034
FEATURE [Part::Cut] Cut647
  Base = -> Cut646
  Tool = -> Cylinder1960
FEATURE [Part::Cut] Cut642
  Base = -> Cut647
  Tool = -> Chamfer070
FEATURE [Part::Cut] Cut651
  Base = -> Cut642
  Tool = -> Compound1032
FEATURE [Part::Cut] Cut655
  Base = -> Cut651
  Tool = -> Box862
FEATURE [Part::Cut] Cut640
  Base = -> Cut655
  Tool = -> Cylinder1964
FEATURE [Part::Cut] Cut654
  Base = -> Cut640
  Tool = -> Compound1033
FEATURE [Part::Cut] Cut653
  Base = -> Cut654
  Tool = -> Compound1041
FEATURE [Part::Cut] Cut650
  Base = -> Cut653
  Tool = -> Compound1035
FEATURE [Part::Cut] Cut641
  Base = -> Cut650
  Tool = -> Compound1036
FEATURE [Part::Cut] Cut643
  Base = -> Cut641
  Tool = -> Compound1039
FEATURE [Part::Cut] Cut648
  Base = -> Cut643
  Tool = -> Compound1038
FEATURE [Part::Cut] Cut645
  Base = -> Cut648
  Tool = -> Compound1040
FEATURE [Part::Cut] Cut644
  Base = -> Cut645
  Tool = -> Cylinder1986
FEATURE [Part::Chamfer] Chamfer071  label="Ele-box_anti-standard001"
  Base = -> Cut644
  Edges = 3 edges r=3.99: [Edge19,Edge22,Edge48]
FEATURE [Part::Chamfer] Chamfer072  label="Ele-box_standalone-anti-standard"
  Base = -> Chamfer071
  Edges = 1 edges r=3.99: [Edge72]
FEATURE [Part::Cylinder] Cylinder1987  label="Válec1987"
  Angle = 360
  AttacherType = Attacher::AttachEngine3D
  Height = 10
  Placement = pos=(29,6,39) rot=(1,0,0;1.5708rad)
  Radius = 1.5
FEATURE [Part::Box] Box870  label="Krychle870"
  AttacherType = Attacher::AttachEngine3D
  Height = 6
  Length = 2
  Placement = pos=(34,64,0) rot=(0,0,1;0rad)
  Width = 6
FEATURE [Part::Cylinder] Cylinder1988  label="Válec1988"
  Angle = 360
  AttacherType = Attacher::AttachEngine3D
  Height = 60
  Placement = pos=(26,13,117) rot=(0,1,0;1.5708rad)
  Radius = 1.75
FEATURE [Part::Box] Box871  label="Krychle871"
  AttacherType = Attacher::AttachEngine3D
  Height = 6
  Length = 2
  Placement = pos=(34,64,114) rot=(0,0,1;0rad)
  Width = 6
FEATURE [Part::Box] Box872  label="Krychle872"
  AttacherType = Attacher::AttachEngine3D
  Height = 6
  Length = 2
  Placement = pos=(34,10,0) rot=(0,0,1;0rad)
  Width = 6
FEATURE [Part::Cylinder] Cylinder1989  label="Válec1989"
  Angle = 360
  AttacherType = Attacher::AttachEngine3D
  Height = 10
  Placement = pos=(16,82,66) rot=(1,0,0;1.5708rad)
  Radius = 9
FEATURE [Part::Box] Box873  label="Krychle873"
  AttacherType = Attacher::AttachEngine3D
  Height = 6
  Length = 2
  Placement = pos=(34,10,0) rot=(0,0,1;0rad)
  Width = 6
FEATURE [Part::Box] Box874  label="Krychle874"
  AttacherType = Attacher::AttachEngine3D
  Height = 6
  Length = 2
  Placement = pos=(34,10,114) rot=(0,0,1;0rad)
  Width = 6
FEATURE [Part::Cylinder] Cylinder1990  label="Válec1990"
  Angle = 360
  AttacherType = Attacher::AttachEngine3D
  Height = 10
  Placement = pos=(29,21,0) rot=(0,0,1;0rad)
  Radius = 1.5
FEATURE [Part::Cylinder] Cylinder1991  label="Válec1991"
  Angle = 360
  AttacherType = Attacher::AttachEngine3D
  Height = 60
  Placement = pos=(26,13,3) rot=(0,1,0;1.5708rad)
  Radius = 1.75
FEATURE [Part::Box] Box875  label="Krychle875"
  AttacherType = Attacher::AttachEngine3D
  Height = 108
  Length = 30
  Placement = pos=(2,4,3) rot=(0,0,1;0rad)
  Width = 72
FEATURE [Part::Box] Box876  label="Krychle876"
  AttacherType = Attacher::AttachEngine3D
  Height = 6
  Length = 2
  Placement = pos=(34,10,114) rot=(0,0,1;0rad)
  Width = 6
FEATURE [Part::Box] Box877  label="Krychle877"
  AttacherType = Attacher::AttachEngine3D
  Height = 2
  Length = 6
  Placement = pos=(0,40,3) rot=(0,0,1;0rad)
  Width = 6
FEATURE [Part::Box] Box878  label="Krychle878"
  AttacherType = Attacher::AttachEngine3D
  Height = 3
  Length = 8
  Placement = pos=(12,-2,39) rot=(0,0,1;0rad)
  Width = 10
FEATURE [Part::Cylinder] Cylinder1992  label="Válec1992"
  Angle = 360
  AttacherType = Attacher::AttachEngine3D
  Height = 3
  Placement = pos=(26,73,3) rot=(0,1,0;1.5708rad)
  Radius = 3
FEATURE [Part::Cylinder] Cylinder1993  label="Válec1993"
  Angle = 360
  AttacherType = Attacher::AttachEngine3D
  Height = 10
  Placement = pos=(16,6,18) rot=(1,0,0;1.5708rad)
  Radius = 8
FEATURE [Part::Cylinder] Cylinder1994  label="Válec1994"
  Angle = 360
  AttacherType = Attacher::AttachEngine3D
  Height = 3
  Placement = pos=(26,7,3) rot=(0,1,0;1.5708rad)
  Radius = 3
FEATURE [Part::Cylinder] Cylinder1995  label="Válec1995"
  Angle = 360
  AttacherType = Attacher::AttachEngine3D
  Height = 10
  Placement = pos=(3,43,0) rot=(0,0,1;0rad)
  Radius = 1.5
FEATURE [Part::Box] Box879  label="Krychle879"
  AttacherType = Attacher::AttachEngine3D
  Height = 21
  Length = 17.5
  Placement = pos=(10.75,-2,42) rot=(0,0,1;0rad)
  Width = 10
FEATURE [Part::Chamfer] Chamfer073
  Base = -> Box879
  Edges = 1 edges r=3: [Edge2]
  Placement = pos=(-4,0,0) rot=(0,0,1;0rad)
FEATURE [Part::Cylinder] Cylinder1996  label="Válec1996"
  Angle = 360
  AttacherType = Attacher::AttachEngine3D
  Height = 60
  Placement = pos=(26,67,3) rot=(0,1,0;1.5708rad)
  Radius = 1.75
FEATURE [Part::Cylinder] Cylinder1997  label="Válec1997"
  Angle = 360
  AttacherType = Attacher::AttachEngine3D
  Height = 60
  Placement = pos=(26,13,117) rot=(0,1,0;1.5708rad)
  Radius = 1.75
FEATURE [Part::Box] Box880  label="Krychle880"
  AttacherType = Attacher::AttachEngine3D
  Height = 6
  Length = 2
  Placement = pos=(34,64,114) rot=(0,0,1;0rad)
  Width = 6
FEATURE [Part::Compound] Compound1047
  Links = -> [Box873,Box870,Box874,Box880]
  Placement = pos=(-8,0,-3) rot=(0,0,1;0rad)
FEATURE [Part::Box] Box881  label="Krychle881"
  AttacherType = Attacher::AttachEngine3D
  Height = 120
  Length = 32
  Placement = pos=(0,0,-3) rot=(0,0,1;0rad)
  Width = 80
FEATURE [Part::Cut] Cut656
  Base = -> Box881
  Tool = -> Box875
FEATURE [Part::Cut] Cut667
  Base = -> Cut656
  Tool = -> Compound1047
FEATURE [Part::Cylinder] Cylinder1998  label="Válec1998"
  Angle = 360
  AttacherType = Attacher::AttachEngine3D
  Height = 60
  Placement = pos=(26,67,117) rot=(0,1,0;1.5708rad)
  Radius = 1.75
FEATURE [Part::Compound] Compound1044
  Links = -> [Cylinder1991,Cylinder1996,Cylinder1988,Cylinder1998]
  Placement = pos=(-8,0,-3) rot=(0,0,1;0rad)
FEATURE [Part::Cut] Cut659
  Base = -> Cut667
  Tool = -> Compound1044
FEATURE [Part::Cut] Cut660
  Base = -> Cut659
  Tool = -> Cylinder1989
FEATURE [Part::Box] Box882  label="Krychle882"
  AttacherType = Attacher::AttachEngine3D
  Height = 2
  Length = 6
  Placement = pos=(26,18,3) rot=(0,0,1;0rad)
  Width = 6
FEATURE [Part::Cylinder] Cylinder1999  label="Válec1999"
  Angle = 360
  AttacherType = Attacher::AttachEngine3D
  Height = 10
  Placement = pos=(10,6,63) rot=(1,0,0;1.5708rad)
  Radius = 1.5
FEATURE [Part::Compound] Compound1042
  Links = -> [Cylinder1999,Cylinder1987]
  Placement = pos=(-4,0,0) rot=(0,0,1;0rad)
FEATURE [Part::Cylinder] Cylinder2000  label="Válec2000"
  Angle = 360
  AttacherType = Attacher::AttachEngine3D
  Height = 10
  Placement = pos=(3,21,0) rot=(0,0,1;0rad)
  Radius = 1.5
FEATURE [Part::Cylinder] Cylinder2001  label="Válec2001"
  Angle = 360
  AttacherType = Attacher::AttachEngine3D
  Height = 60
  Placement = pos=(26,13,3) rot=(0,1,0;1.5708rad)
  Radius = 1.75
FEATURE [Part::Box] Box883  label="Krychle883"
  AttacherType = Attacher::AttachEngine3D
  Height = 2
  Length = 6
  Placement = pos=(26,40,3) rot=(0,0,1;0rad)
  Width = 6
FEATURE [Part::Cylinder] Cylinder2002  label="Válec2002"
  Angle = 360
  AttacherType = Attacher::AttachEngine3D
  Height = 100
  Placement = pos=(26,73,117) rot=(0,1,0;1.5708rad)
  Radius = 1.75
FEATURE [Part::Cylinder] Cylinder2003  label="Válec2003"
  Angle = 360
  AttacherType = Attacher::AttachEngine3D
  Height = 3
  Placement = pos=(26,7,117) rot=(0,1,0;1.5708rad)
  Radius = 3
FEATURE [Part::Cylinder] Cylinder2004  label="Válec2004"
  Angle = 360
  AttacherType = Attacher::AttachEngine3D
  Height = 60
  Placement = pos=(26,67,3) rot=(0,1,0;1.5708rad)
  Radius = 1.75
FEATURE [Part::Cylinder] Cylinder2005  label="Válec2005"
  Angle = 360
  AttacherType = Attacher::AttachEngine3D
  Height = 3
  Placement = pos=(26,7,3) rot=(0,1,0;1.5708rad)
  Radius = 3
FEATURE [Part::Cylinder] Cylinder2006  label="Válec2006"
  Angle = 360
  AttacherType = Attacher::AttachEngine3D
  Height = 100
  Placement = pos=(26,7,117) rot=(0,1,0;1.5708rad)
  Radius = 1.75
FEATURE [Part::Cylinder] Cylinder2007  label="Válec2007"
  Angle = 360
  AttacherType = Attacher::AttachEngine3D
  Height = 10
  Placement = pos=(29,43,0) rot=(0,0,1;0rad)
  Radius = 1.5
FEATURE [Part::Cylinder] Cylinder2008  label="Válec2008"
  Angle = 360
  AttacherType = Attacher::AttachEngine3D
  Height = 100
  Placement = pos=(26,73,3) rot=(0,1,0;1.5708rad)
  Radius = 1.75
FEATURE [Part::Cylinder] Cylinder2009  label="Válec2009"
  Angle = 360
  AttacherType = Attacher::AttachEngine3D
  Height = 3
  Placement = pos=(26,73,117) rot=(0,1,0;1.5708rad)
  Radius = 3
FEATURE [Part::Cylinder] Cylinder2010  label="Válec2010"
  Angle = 360
  AttacherType = Attacher::AttachEngine3D
  Height = 3
  Placement = pos=(26,73,3) rot=(0,1,0;1.5708rad)
  Radius = 3
FEATURE [Part::Cylinder] Cylinder2011  label="Válec2011"
  Angle = 360
  AttacherType = Attacher::AttachEngine3D
  Height = 3
  Placement = pos=(26,73,117) rot=(0,1,0;1.5708rad)
  Radius = 3
FEATURE [Part::Compound] Compound1048
  Links = -> [Cylinder2005,Cylinder2010,Cylinder2003,Cylinder2011]
  Placement = pos=(3,0,-3) rot=(0,0,1;0rad)
FEATURE [Part::Cylinder] Cylinder2012  label="Válec2012"
  Angle = 360
  AttacherType = Attacher::AttachEngine3D
  Height = 60
  Placement = pos=(26,67,117) rot=(0,1,0;1.5708rad)
  Radius = 1.75
FEATURE [Part::Compound] Compound1046
  Links = -> [Cylinder2001,Cylinder2004,Cylinder1997,Cylinder2012]
  Placement = pos=(-72,0,-3) rot=(0,0,1;0rad)
FEATURE [Part::Box] Box884  label="Krychle884"
  AttacherType = Attacher::AttachEngine3D
  Height = 2
  Length = 6
  Placement = pos=(0,18,3) rot=(0,0,1;0rad)
  Width = 6
FEATURE [Part::Compound] Compound1043
  Links = -> [Box884,Box877,Box883,Box882]
  Placement = pos=(0,0,-100) rot=(0,0,1;0rad)
FEATURE [Part::Box] Box885  label="Krychle885"
  AttacherType = Attacher::AttachEngine3D
  Height = 6
  Length = 2
  Placement = pos=(34,64,0) rot=(0,0,1;0rad)
  Width = 6
FEATURE [Part::Compound] Compound1045
  Links = -> [Box872,Box885,Box876,Box871]
  Placement = pos=(-30,0,-3) rot=(0,0,1;0rad)
FEATURE [Part::Cylinder] Cylinder2013  label="Válec2013"
  Angle = 360
  AttacherType = Attacher::AttachEngine3D
  Height = 100
  Placement = pos=(26,7,3) rot=(0,1,0;1.5708rad)
  Radius = 1.75
FEATURE [Part::Compound] Compound1049
  Links = -> [Cylinder2013,Cylinder2008,Cylinder2006,Cylinder2002]
  Placement = pos=(-72,0,-3) rot=(0,0,1;0rad)
FEATURE [Part::Cylinder] Cylinder2014  label="Válec2014"
  Angle = 360
  AttacherType = Attacher::AttachEngine3D
  Height = 3
  Placement = pos=(26,7,117) rot=(0,1,0;1.5708rad)
  Radius = 3
FEATURE [Part::Compound] Compound1050
  Links = -> [Cylinder1994,Cylinder1992,Cylinder2014,Cylinder2009]
  Placement = pos=(-26,0,-3) rot=(0,0,1;0rad)
FEATURE [Part::Compound] Compound1051
  Links = -> [Cylinder2000,Cylinder1995,Cylinder1990,Cylinder2007]
  Placement = pos=(0,0,-100) rot=(0,0,1;0rad)
FEATURE [Part::Cut] Cut669
  Base = -> Cut660
  Tool = -> Chamfer073
FEATURE [Part::Cut] Cut666
  Base = -> Cut669
  Tool = -> Compound1042
FEATURE [Part::Cut] Cut665
  Base = -> Cut666
  Tool = -> Box878
FEATURE [Part::Cut] Cut662
  Base = -> Cut665
  Tool = -> Cylinder1993
FEATURE [Part::Cut] Cut664
  Base = -> Cut662
  Tool = -> Compound1043
FEATURE [Part::Cut] Cut663
  Base = -> Cut664
  Tool = -> Compound1051
FEATURE [Part::Cut] Cut657
  Base = -> Cut663
  Tool = -> Compound1045
FEATURE [Part::Cut] Cut668
  Base = -> Cut657
  Tool = -> Compound1046
FEATURE [Part::Cut] Cut670
  Base = -> Cut668
  Tool = -> Compound1049
FEATURE [Part::Cut] Cut661
  Base = -> Cut670
  Tool = -> Compound1048
FEATURE [Part::Cut] Cut658
  Base = -> Cut661
  Tool = -> Compound1050
FEATURE [Part::Cylinder] Cylinder2015  label="Válec2015"
  Angle = 360
  AttacherType = Attacher::AttachEngine3D
  Height = 10
  Placement = pos=(16,82,97) rot=(1,0,0;1.5708rad)
  Radius = 9
FEATURE [Part::Box] Box886  label="Krychle886"
  AttacherType = Attacher::AttachEngine3D
  Height = 4
  Length = 32
  Placement = pos=(0,4,32) rot=(0,0,1;0rad)
  Width = 60
FEATURE [Part::Cut] Cut671
  Base = -> Cut658
  Tool = -> Cylinder2015
FEATURE [Part::Box] Box887  label="Krychle887"
  AttacherType = Attacher::AttachEngine3D
  Height = 44
  Length = 32
  Placement = pos=(0,60,36) rot=(0,0,1;0rad)
  Width = 4
FEATURE [Part::Box] Box888  label="Krychle888"
  AttacherType = Attacher::AttachEngine3D
  Height = 4
  Length = 32
  Placement = pos=(0,60,80) rot=(0,0,1;0rad)
  Width = 16
FEATURE [Part::Compound] Compound1052  label="Ele-box_separator003"
  Links = -> [Box886,Box887,Box888]
FEATURE [Part::Chamfer] Chamfer074
  Base = -> Cut671
  Edges = 4 edges r=4: [Edge19,Edge22,Edge44,Edge48]
FEATURE [Part::Chamfer] Chamfer075
  Base = -> Compound1052
  Edges = 2 edges r=3: [Edge11,Edge34]
FEATURE [Part::Compound] Compound1053  label="Ele-box_standalone-standard"
  Links = -> [Chamfer074,Chamfer075]
FEATURE [Part::Box] Box485  label="Krychle485"
  AttacherType = Attacher::AttachEngine3D
  Height = 49
  Length = 56
  Placement = pos=(-28,35,29) rot=(0,0,1;0rad)
  Width = 200
FEATURE [Part::Box] Box486  label="Krychle486"
  AttacherType = Attacher::AttachEngine3D
  Height = 55
  Length = 148
  Placement = pos=(-74,68,29) rot=(0,0,1;0rad)
  Width = 26
FEATURE [Part::Cylinder] Cylinder971  label="Válec971"
  Angle = 360
  AttacherType = Attacher::AttachEngine3D
  Height = 6
  Placement = pos=(0,0,65) rot=(0,0,1;0rad)
  Radius = 74
FEATURE [Part::Box] Box483  label="Krychle483"
  AttacherType = Attacher::AttachEngine3D
  Height = 34
  Length = 148
  Placement = pos=(-74,68,38) rot=(0,0,1;0rad)
  Width = 20
FEATURE [Part::Cut] Cut453
  Base = -> Cylinder971
  Placement = pos=(0,0,13) rot=(0,0,1;0rad)
  Tool = -> Box483
FEATURE [Part::Box] Box648  label="Krychle648"
  AttacherType = Attacher::AttachEngine3D
  Height = 60
  Length = 200
  Placement = pos=(0,0,-5) rot=(0,0,-1;0.383972rad)
  Width = 200
FEATURE [Part::Box] Box647  label="Krychle647"
  AttacherType = Attacher::AttachEngine3D
  Height = 60
  Length = 200
  Placement = pos=(70.7107,70.7107,-5) rot=(0,0,1;3.92699rad)
  Width = 120
FEATURE [Part::Cut] Cut464
  Base = -> Box647
  Tool = -> Box648
FEATURE [Part::Box] Box649  label="Krychle649"
  AttacherType = Attacher::AttachEngine3D
  Height = 60
  Length = 200
  Placement = pos=(0,0,-5) rot=(0,0,1;3.52556rad)
  Width = 200
FEATURE [Part::Cut] Cut465
  Base = -> Cut464
  Tool = -> Box649
FEATURE [Part::FeaturePython] Tube035  # WARN: FeaturePython — macro-defined, semantics opaque (R4)
  AttacherType = Attacher::AttachEngine3D
  Height = 55
  InnerRadius = 68
  OuterRadius = 74
  Placement = pos=(0,0,29) rot=(0,0,1;0rad)
FEATURE [Part::Cut] Cut455
  Base = -> Tube035
  Tool = -> Box485
FEATURE [Part::Cut] Cut454
  Base = -> Cut455
  Tool = -> Box486
FEATURE [Part::Cut] Cut672
  Base = -> Cut454
  Tool = -> Cut465
FEATURE [Part::FeaturePython] Tube036  # WARN: FeaturePython — macro-defined, semantics opaque (R4)
  AttacherType = Attacher::AttachEngine3D
  Height = 8
  InnerRadius = 50.1
  OuterRadius = 58
  Placement = pos=(0,0,72) rot=(0,0,1;0rad)
FEATURE [Part::Box] Box488  label="Krychle488"
  AttacherType = Attacher::AttachEngine3D
  Height = 2
  Length = 6
  Placement = pos=(-3,-75,39) rot=(0,0,1;0rad)
  Width = 8
FEATURE [Part::Box] Box489  label="Krychle489"
  AttacherType = Attacher::AttachEngine3D
  Height = 2
  Length = 6
  Placement = pos=(34.9,-66.45,58) rot=(0,0,1;0.523599rad)
  Width = 8
FEATURE [Part::Box] Box497  label="Krychle497"
  AttacherType = Attacher::AttachEngine3D
  Height = 2
  Length = 6
  Placement = pos=(-75,3,39) rot=(0,0,-1;1.5708rad)
  Width = 8
FEATURE [Part::Box] Box493  label="Krychle493"
  AttacherType = Attacher::AttachEngine3D
  Height = 2
  Length = 6
  Placement = pos=(40.0981,63.4519,39) rot=(0,0,1;2.61799rad)
  Width = 8
FEATURE [Part::Box] Box491  label="Krychle491"
  AttacherType = Attacher::AttachEngine3D
  Height = 2
  Length = 6
  Placement = pos=(75,-3,39) rot=(0,0,1;1.5708rad)
  Width = 8
FEATURE [Part::Box] Box495  label="Krychle495"
  AttacherType = Attacher::AttachEngine3D
  Height = 2
  Length = 6
  Placement = pos=(-34.9019,66.4519,39) rot=(0,0,1;3.66519rad)
  Width = 8
FEATURE [Part::Box] Box490  label="Krychle490"
  AttacherType = Attacher::AttachEngine3D
  Height = 2
  Length = 6
  Placement = pos=(63.45,-40.1,58) rot=(0,0,1;1.0472rad)
  Width = 8
FEATURE [Part::Box] Box889  label="Krychle889"
  AttacherType = Attacher::AttachEngine3D
  Height = 2
  Length = 6
  Placement = pos=(3,75,39) rot=(0,0,1;3.14159rad)
  Width = 8
FEATURE [Part::Box] Box498  label="Krychle498"
  AttacherType = Attacher::AttachEngine3D
  Height = 2
  Length = 6
  Placement = pos=(-66.4519,-34.9019,39) rot=(0,0,-1;1.0472rad)
  Width = 8
FEATURE [Part::Box] Box492  label="Krychle492"
  AttacherType = Attacher::AttachEngine3D
  Height = 2
  Length = 6
  Placement = pos=(66.4519,34.9019,39) rot=(0,0,1;2.0944rad)
  Width = 8
FEATURE [Part::Box] Box499  label="Krychle499"
  AttacherType = Attacher::AttachEngine3D
  Height = 2
  Length = 6
  Placement = pos=(-40.0981,-63.4519,39) rot=(0,0,-1;0.523599rad)
  Width = 8
FEATURE [Part::Box] Box496  label="Krychle496"
  AttacherType = Attacher::AttachEngine3D
  Height = 2
  Length = 6
  Placement = pos=(-63.4519,40.0981,39) rot=(0,0,1;4.18879rad)
  Width = 8
FEATURE [Part::Compound] Compound1054
  Links = -> [Box488,Box489,Box490,Box491,Box492,Box493,Box889,Box495,Box496,Box497,Box498,Box499]
FEATURE [Part::Cut] Cut467
  Base = -> Cut672
  Tool = -> Compound1054
FEATURE [Part::Cylinder] Cylinder1629  label="Válec1629"
  Angle = 360
  AttacherType = Attacher::AttachEngine3D
  Height = 72
  Placement = pos=(71,-1.8e-14,0) rot=(0,0,1;1.5708rad)
  Radius = 1.5
FEATURE [Part::Cylinder] Cylinder1630  label="Válec1630"
  Angle = 360
  AttacherType = Attacher::AttachEngine3D
  Height = 72
  Placement = pos=(35.5,61.4878,0) rot=(0,0,1;2.61799rad)
  Radius = 1.5
FEATURE [Part::Cylinder] Cylinder1631  label="Válec1631"
  Angle = 360
  AttacherType = Attacher::AttachEngine3D
  Height = 72
  Placement = pos=(61.4878,-35.5,0) rot=(0,0,1;1.0472rad)
  Radius = 1.5
FEATURE [Part::Cylinder] Cylinder1632  label="Válec1632"
  Angle = 360
  AttacherType = Attacher::AttachEngine3D
  Height = 72
  Placement = pos=(35.5,-61.4878,0) rot=(0,0,1;0.523599rad)
  Radius = 1.5
FEATURE [Part::Cylinder] Cylinder1633  label="Válec1633"
  Angle = 360
  AttacherType = Attacher::AttachEngine3D
  Height = 72
  Placement = pos=(-35.5,-61.4878,0) rot=(0,0,-1;0.523599rad)
  Radius = 1.5
FEATURE [Part::Cylinder] Cylinder1634  label="Válec1634"
  Angle = 360
  AttacherType = Attacher::AttachEngine3D
  Height = 72
  Placement = pos=(-71,2.7e-14,0) rot=(0,0,-1;1.5708rad)
  Radius = 1.5
FEATURE [Part::Cylinder] Cylinder1635  label="Válec1635"
  Angle = 360
  AttacherType = Attacher::AttachEngine3D
  Height = 72
  Placement = pos=(-61.4878,-35.5,0) rot=(0,0,-1;1.0472rad)
  Radius = 1.5
FEATURE [Part::Cylinder] Cylinder1636  label="Válec1636"
  Angle = 360
  AttacherType = Attacher::AttachEngine3D
  Height = 72
  Placement = pos=(61.4878,35.5,0) rot=(0,0,1;2.0944rad)
  Radius = 1.5
FEATURE [Part::Cylinder] Cylinder1637  label="Válec1637"
  Angle = 360
  AttacherType = Attacher::AttachEngine3D
  Height = 72
  Placement = pos=(0,-71,0) rot=(0,0,1;0rad)
  Radius = 1.5
FEATURE [Part::Cylinder] Cylinder1638  label="Válec1638"
  Angle = 360
  AttacherType = Attacher::AttachEngine3D
  Height = 72
  Placement = pos=(-35.5,61.4878,0) rot=(0,0,1;3.66519rad)
  Radius = 1.5
FEATURE [Part::Cylinder] Cylinder1639  label="Válec1639"
  Angle = 360
  AttacherType = Attacher::AttachEngine3D
  Height = 72
  Placement = pos=(-61.4878,35.5,0) rot=(0,0,1;4.18879rad)
  Radius = 1.5
FEATURE [Part::Cylinder] Cylinder1640  label="Válec1640"
  Angle = 360
  AttacherType = Attacher::AttachEngine3D
  Height = 72
  Placement = pos=(3.1e-14,71,0) rot=(0,0,1;3.14159rad)
  Radius = 1.5
FEATURE [Part::Compound] Compound529
  Links = -> [Cylinder1637,Cylinder1632,Cylinder1631,Cylinder1629,Cylinder1636,Cylinder1630,Cylinder1640,Cylinder1638,Cylinder1639,Cylinder1634,Cylinder1635,Cylinder1633]
  Placement = pos=(0,0,-4) rot=(0,0,1;0rad)
FEATURE [Part::Cut] Cut468
  Base = -> Cut467
  Tool = -> Compound529
FEATURE [Part::Cylinder] Cylinder1722  label="Válec1722"
  Angle = 360
  AttacherType = Attacher::AttachEngine3D
  Height = 50
  Placement = pos=(-18,100,72) rot=(1,0,0;1.5708rad)
  Radius = 1.5
FEATURE [Part::Cylinder] Cylinder1723  label="Válec1723"
  Angle = 360
  AttacherType = Attacher::AttachEngine3D
  Height = 50
  Placement = pos=(18,100,72) rot=(1,0,0;1.5708rad)
  Radius = 1.5
FEATURE [Part::Box] Box686  label="Krychle686"
  AttacherType = Attacher::AttachEngine3D
  Height = 6
  Length = 6
  Placement = pos=(15,64,-50) rot=(0,0,1;0rad)
  Width = 4
FEATURE [Part::Box] Box687  label="Krychle687"
  AttacherType = Attacher::AttachEngine3D
  Height = 6
  Length = 6
  Placement = pos=(-21,64,-50) rot=(0,0,1;0rad)
  Width = 4
FEATURE [Part::Compound] Compound863
  Links = -> [Cylinder1722]
  Placement = pos=(0,0,0) rot=(0,0,1;3.92699rad)
FEATURE [Part::Compound] Compound864
  Links = -> [Cylinder1723]
  Placement = pos=(0,0,0) rot=(0,0,1;3.92699rad)
FEATURE [Part::Compound] Compound865
  Links = -> [Compound863,Compound864]
  Placement = pos=(0,0,1) rot=(0,0,1;0rad)
FEATURE [Part::Compound] Compound866
  Links = -> [Box687,Box686]
  Placement = pos=(0,0,120) rot=(0,0,1;3.92699rad)
FEATURE [Part::Cut] Cut500
  Base = -> Cut468
  Tool = -> Compound865
FEATURE [Part::Cut] Cut501
  Base = -> Cut500
  Tool = -> Compound866
FEATURE [Part::Cylinder] Cylinder1737  label="Válec1737"
  Angle = 360
  AttacherType = Attacher::AttachEngine3D
  Height = 50
  Placement = pos=(-9,100,59) rot=(1,0,0;1.5708rad)
  Radius = 1.5
FEATURE [Part::Cylinder] Cylinder1738  label="Válec1738"
  Angle = 360
  AttacherType = Attacher::AttachEngine3D
  Height = 50
  Placement = pos=(9,100,59) rot=(1,0,0;1.5708rad)
  Radius = 1.5
FEATURE [Part::Box] Box691  label="Krychle691"
  AttacherType = Attacher::AttachEngine3D
  Height = 6
  Length = 6
  Placement = pos=(6,66,-63) rot=(0,0,1;0rad)
  Width = 4
FEATURE [Part::Box] Box692  label="Krychle692"
  AttacherType = Attacher::AttachEngine3D
  Height = 6
  Length = 6
  Placement = pos=(-12,66,-63) rot=(0,0,1;0rad)
  Width = 4
FEATURE [Part::Compound] Compound878
  Links = -> [Cylinder1738]
  Placement = pos=(0,0,0) rot=(0,0,1;3.92699rad)
FEATURE [Part::Compound] Compound879
  Links = -> [Cylinder1737]
  Placement = pos=(0,0,0) rot=(0,0,1;3.92699rad)
FEATURE [Part::Compound] Compound877
  Links = -> [Compound879,Compound878]
  Placement = pos=(0,0,1) rot=(0,0,1;0rad)
FEATURE [Part::Compound] Compound880
  Links = -> [Box692,Box691]
  Placement = pos=(0,0,120) rot=(0,0,1;3.92699rad)
FEATURE [Part::Cut] Cut508
  Base = -> Cut501
  Tool = -> Compound877
FEATURE [Part::Cut] Cut509
  Base = -> Cut508
  Tool = -> Compound880
FEATURE [Part::Box] Box482  label="Krychle482"
  AttacherType = Attacher::AttachEngine3D
  Height = 55
  Length = 148
  Placement = pos=(-74,0,29) rot=(0,0,1;0rad)
  Width = 74
FEATURE [Part::Cylinder] Cylinder972  label="Válec972"
  Angle = 360
  AttacherType = Attacher::AttachEngine3D
  Height = 51
  Placement = pos=(0,0,29) rot=(0,0,1;0rad)
  Radius = 74
FEATURE [Part::Cut] Cut451
  Base = -> Box482
  Tool = -> Cylinder972
FEATURE [Part::Box] Box484  label="Krychle484"
  AttacherType = Attacher::AttachEngine3D
  Height = 55
  Length = 148
  Placement = pos=(-74,48,29) rot=(0,0,1;0rad)
  Width = 26
FEATURE [Part::Cut] Cut452
  Base = -> Cut451
  Tool = -> Box484
FEATURE [Part::Cylinder] Cylinder1753  label="Válec1753"
  Angle = 360
  AttacherType = Attacher::AttachEngine3D
  Height = 50
  Placement = pos=(-71,80,73) rot=(1,0,0;1.5708rad)
  Radius = 1.5
FEATURE [Part::Cylinder] Cylinder1754  label="Válec1754"
  Angle = 360
  AttacherType = Attacher::AttachEngine3D
  Height = 50
  Placement = pos=(71,80,39) rot=(1,0,0;1.5708rad)
  Radius = 1.5
FEATURE [Part::Cylinder] Cylinder1755  label="Válec1755"
  Angle = 360
  AttacherType = Attacher::AttachEngine3D
  Height = 50
  Placement = pos=(-71,80,39) rot=(1,0,0;1.5708rad)
  Radius = 1.5
FEATURE [Part::Cylinder] Cylinder1756  label="Válec1756"
  Angle = 360
  AttacherType = Attacher::AttachEngine3D
  Height = 50
  Placement = pos=(71,80,73) rot=(1,0,0;1.5708rad)
  Radius = 1.5
FEATURE [Part::Cylinder] Cylinder1757  label="Válec1757"
  Angle = 360
  AttacherType = Attacher::AttachEngine3D
  Height = 50
  Placement = pos=(-71,80,56) rot=(1,0,0;1.5708rad)
  Radius = 1.5
FEATURE [Part::Cylinder] Cylinder1758  label="Válec1758"
  Angle = 360
  AttacherType = Attacher::AttachEngine3D
  Height = 50
  Placement = pos=(71,80,56) rot=(1,0,0;1.5708rad)
  Radius = 1.5
FEATURE [Part::Compound] Compound887
  Links = -> [Cylinder1753,Cylinder1754,Cylinder1755,Cylinder1756,Cylinder1757,Cylinder1758]
FEATURE [Part::Cut] Cut518
  Base = -> Cut452
  Tool = -> Compound887
FEATURE [Part::Box] Box890  label="Krychle890"
  AttacherType = Attacher::AttachEngine3D
  Height = 6
  Length = 8
  Placement = pos=(-75,38,36) rot=(0,0,1;0rad)
  Width = 2
FEATURE [Part::Box] Box891  label="Krychle891"
  AttacherType = Attacher::AttachEngine3D
  Height = 6
  Length = 8
  Placement = pos=(67,38,36) rot=(0,0,1;0rad)
  Width = 2
FEATURE [Part::Box] Box892  label="Krychle892"
  AttacherType = Attacher::AttachEngine3D
  Height = 6
  Length = 8
  Placement = pos=(67,38,70) rot=(0,0,1;0rad)
  Width = 2
FEATURE [Part::Box] Box893  label="Krychle893"
  AttacherType = Attacher::AttachEngine3D
  Height = 6
  Length = 8
  Placement = pos=(-75,38,70) rot=(0,0,1;0rad)
  Width = 2
FEATURE [Part::Box] Box894  label="Krychle894"
  AttacherType = Attacher::AttachEngine3D
  Height = 6
  Length = 8
  Placement = pos=(-75,38,53) rot=(0,0,1;0rad)
  Width = 2
FEATURE [Part::Box] Box895  label="Krychle895"
  AttacherType = Attacher::AttachEngine3D
  Height = 6
  Length = 8
  Placement = pos=(67,38,53) rot=(0,0,1;0rad)
  Width = 2
FEATURE [Part::Compound] Compound530
  Links = -> [Box890,Box891,Box892,Box893,Box894,Box895]
FEATURE [Part::Box] Box699  label="Krychle699"
  AttacherType = Attacher::AttachEngine3D
  Height = 2
  Length = 6
  Placement = pos=(-3,-75,39) rot=(0,0,1;0rad)
  Width = 8
FEATURE [Part::Box] Box700  label="Krychle700"
  AttacherType = Attacher::AttachEngine3D
  Height = 2
  Length = 6
  Placement = pos=(34.9019,-66.4519,39) rot=(0,0,1;0.523599rad)
  Width = 8
FEATURE [Part::Box] Box701  label="Krychle701"
  AttacherType = Attacher::AttachEngine3D
  Height = 2
  Length = 6
  Placement = pos=(63.4519,-40.0981,39) rot=(0,0,1;1.0472rad)
  Width = 8
FEATURE [Part::Cut] Cut519
  Base = -> Cut518
  Tool = -> Compound530
FEATURE [Part::Box] Box702  label="Krychle702"
  AttacherType = Attacher::AttachEngine3D
  Height = 2
  Length = 6
  Placement = pos=(75,-3,39) rot=(0,0,1;1.5708rad)
  Width = 8
FEATURE [Part::Box] Box703  label="Krychle703"
  AttacherType = Attacher::AttachEngine3D
  Height = 2
  Length = 6
  Placement = pos=(66.4519,34.9019,39) rot=(0,0,1;2.0944rad)
  Width = 8
FEATURE [Part::Box] Box704  label="Krychle704"
  AttacherType = Attacher::AttachEngine3D
  Height = 2
  Length = 6
  Placement = pos=(40.0981,63.4519,39) rot=(0,0,1;2.61799rad)
  Width = 8
FEATURE [Part::Box] Box705  label="Krychle705"
  AttacherType = Attacher::AttachEngine3D
  Height = 2
  Length = 6
  Placement = pos=(3,75,39) rot=(0,0,1;3.14159rad)
  Width = 8
FEATURE [Part::Box] Box706  label="Krychle706"
  AttacherType = Attacher::AttachEngine3D
  Height = 2
  Length = 6
  Placement = pos=(-34.9019,66.4519,39) rot=(0,0,1;3.66519rad)
  Width = 8
FEATURE [Part::Box] Box707  label="Krychle707"
  AttacherType = Attacher::AttachEngine3D
  Height = 2
  Length = 6
  Placement = pos=(-63.4519,40.0981,39) rot=(0,0,1;4.18879rad)
  Width = 8
FEATURE [Part::Box] Box708  label="Krychle708"
  AttacherType = Attacher::AttachEngine3D
  Height = 2
  Length = 6
  Placement = pos=(-75,3,39) rot=(0,0,-1;1.5708rad)
  Width = 8
FEATURE [Part::Box] Box709  label="Krychle709"
  AttacherType = Attacher::AttachEngine3D
  Height = 2
  Length = 6
  Placement = pos=(-66.4519,-34.9019,39) rot=(0,0,-1;1.0472rad)
  Width = 8
FEATURE [Part::Box] Box710  label="Krychle710"
  AttacherType = Attacher::AttachEngine3D
  Height = 2
  Length = 6
  Placement = pos=(-40.0981,-63.4519,39) rot=(0,0,-1;0.523599rad)
  Width = 8
FEATURE [Part::Box] Box425  label="Krychle425"
  AttacherType = Attacher::AttachEngine3D
  Height = 2
  Length = 6
  Placement = pos=(-112,4,60) rot=(0,0,1;0rad)
  Width = 6
FEATURE [Part::Box] Box426  label="Krychle426"
  AttacherType = Attacher::AttachEngine3D
  Height = 20
  Length = 20
  Placement = pos=(-106,4,56) rot=(0,0,1;0rad)
  Width = 80
FEATURE [Part::Box] Box427  label="Krychle427"
  AttacherType = Attacher::AttachEngine3D
  Height = 2
  Length = 6
  Placement = pos=(-112,22,60) rot=(0,0,1;0rad)
  Width = 6
FEATURE [Part::Box] Box428  label="Krychle428"
  AttacherType = Attacher::AttachEngine3D
  Height = 2
  Length = 6
  Placement = pos=(-86,22,60) rot=(0,0,1;0rad)
  Width = 6
FEATURE [Part::Cylinder] Cylinder899  label="Válec899"
  Angle = 360
  AttacherType = Attacher::AttachEngine3D
  Height = 20
  Placement = pos=(-83,25,54) rot=(0,0,1;0rad)
  Radius = 1.5
FEATURE [Part::Box] Box429  label="Krychle429"
  AttacherType = Attacher::AttachEngine3D
  Height = 2
  Length = 6
  Placement = pos=(-86,4,60) rot=(0,0,1;0rad)
  Width = 6
FEATURE [Part::Cylinder] Cylinder900  label="Válec900"
  Angle = 360
  AttacherType = Attacher::AttachEngine3D
  Height = 20
  Placement = pos=(-83,7,54) rot=(0,0,1;0rad)
  Radius = 1.5
FEATURE [Part::Compound] Compound888
  Links = -> [Box699,Box700,Box701,Box702,Box703,Box704,Box705,Box706,Box707,Box708,Box709,Box710]
FEATURE [Part::Cut] Cut520
  Base = -> Cut519
  Tool = -> Compound888
FEATURE [Part::Compound] Compound495
  Links = -> [Box425,Box427,Box429,Box428]
FEATURE [Part::Cylinder] Cylinder901  label="Válec901"
  Angle = 360
  AttacherType = Attacher::AttachEngine3D
  Height = 20
  Placement = pos=(-109,7,54) rot=(0,0,1;0rad)
  Radius = 1.5
FEATURE [Part::Cylinder] Cylinder902  label="Válec902"
  Angle = 360
  AttacherType = Attacher::AttachEngine3D
  Height = 20
  Placement = pos=(-109,25,54) rot=(0,0,1;0rad)
  Radius = 1.5
FEATURE [Part::Compound] Compound496
  Links = -> [Cylinder900,Cylinder899,Cylinder901,Cylinder902]
FEATURE [Part::Box] Box430  label="Krychle430"
  AttacherType = Attacher::AttachEngine3D
  Height = 26
  Length = 38
  Placement = pos=(-112,0,56) rot=(0,0,1;0rad)
  Width = 32
FEATURE [Part::Cylinder] Cylinder903  label="Válec903"
  Angle = 360
  AttacherType = Attacher::AttachEngine3D
  Height = 3
  Placement = pos=(-112,16,66) rot=(0,1,0;1.5708rad)
  Radius = 5
FEATURE [Part::Cylinder] Cylinder904  label="Válec904"
  Angle = 360
  AttacherType = Attacher::AttachEngine3D
  Height = 20
  Placement = pos=(-117,16,66) rot=(0,1,0;1.5708rad)
  Radius = 2.5
FEATURE [Part::Box] Box431  label="Krychle431"
  AttacherType = Attacher::AttachEngine3D
  Height = 6
  Length = 51
  Placement = pos=(-112,-24,76) rot=(0,0,1;0rad)
  Width = 24
FEATURE [Part::Cylinder] Cylinder905  label="Válec905"
  Angle = 360
  AttacherType = Attacher::AttachEngine3D
  Height = 10
  Placement = pos=(0,0,72) rot=(0,0,1;0rad)
  Radius = 74
FEATURE [Part::Cylinder] Cylinder906  label="Válec906"
  Angle = 360
  AttacherType = Attacher::AttachEngine3D
  Height = 32
  Placement = pos=(0,0,50) rot=(0,0,1;0rad)
  Radius = 74
FEATURE [Part::Box] Box432  label="Krychle432"
  AttacherType = Attacher::AttachEngine3D
  Height = 26
  Length = 50
  Placement = pos=(-112,-24,56) rot=(0,0,1;0rad)
  Width = 6
FEATURE [Part::Cylinder] Cylinder907  label="Válec907"
  Angle = 360
  AttacherType = Attacher::AttachEngine3D
  Height = 20
  Placement = pos=(-86,-10,66) rot=(0,0,1;0rad)
  Radius = 2.5
FEATURE [Part::Cylinder] Cylinder908  label="Válec908"
  Angle = 360
  AttacherType = Attacher::AttachEngine3D
  Height = 20
  Placement = pos=(-102,-10,66) rot=(0,0,1;0rad)
  Radius = 2.5
FEATURE [Part::Compound] Compound498
  Links = -> [Cylinder908,Cylinder907]
FEATURE [Part::Box] Box896  label="Krychle896"
  AttacherType = Attacher::AttachEngine3D
  Height = 14
  Length = 24
  Placement = pos=(-92,-24,44) rot=(0,0,1;0rad)
  Width = 6
FEATURE [Part::Chamfer] Chamfer016
  Base = -> Box896
  Edges = 1 edges r=13.99: [Edge4]
FEATURE [Part::Box] Box416  label="Krychle416"
  AttacherType = Attacher::AttachEngine3D
  Height = 26
  Length = 38
  Placement = pos=(-112,0,56) rot=(0,0,1;0rad)
  Width = 32
FEATURE [Part::Box] Box417  label="Krychle417"
  AttacherType = Attacher::AttachEngine3D
  Height = 20
  Length = 20
  Placement = pos=(-106,4,56) rot=(0,0,1;0rad)
  Width = 80
FEATURE [Part::Box] Box418  label="Krychle418"
  AttacherType = Attacher::AttachEngine3D
  Height = 2
  Length = 6
  Placement = pos=(-112,4,60) rot=(0,0,1;0rad)
  Width = 6
FEATURE [Part::Box] Box419  label="Krychle419"
  AttacherType = Attacher::AttachEngine3D
  Height = 2
  Length = 6
  Placement = pos=(-112,22,60) rot=(0,0,1;0rad)
  Width = 6
FEATURE [Part::Box] Box420  label="Krychle420"
  AttacherType = Attacher::AttachEngine3D
  Height = 2
  Length = 6
  Placement = pos=(-86,4,60) rot=(0,0,1;0rad)
  Width = 6
FEATURE [Part::Box] Box421  label="Krychle421"
  AttacherType = Attacher::AttachEngine3D
  Height = 2
  Length = 6
  Placement = pos=(-86,22,60) rot=(0,0,1;0rad)
  Width = 6
FEATURE [Part::Compound] Compound1055
  Links = -> [Box418,Box419,Box420,Box421]
FEATURE [Part::Cylinder] Cylinder1759  label="Válec1759"
  Angle = 360
  AttacherType = Attacher::AttachEngine3D
  Height = 20
  Placement = pos=(-83,7,54) rot=(0,0,1;0rad)
  Radius = 1.5
FEATURE [Part::Cylinder] Cylinder875  label="Válec875"
  Angle = 360
  AttacherType = Attacher::AttachEngine3D
  Height = 20
  Placement = pos=(-83,25,54) rot=(0,0,1;0rad)
  Radius = 1.5
FEATURE [Part::Cylinder] Cylinder876  label="Válec876"
  Angle = 360
  AttacherType = Attacher::AttachEngine3D
  Height = 20
  Placement = pos=(-109,7,54) rot=(0,0,1;0rad)
  Radius = 1.5
FEATURE [Part::Cylinder] Cylinder877  label="Válec877"
  Angle = 360
  AttacherType = Attacher::AttachEngine3D
  Height = 20
  Placement = pos=(-109,25,54) rot=(0,0,1;0rad)
  Radius = 1.5
FEATURE [Part::Cylinder] Cylinder892  label="Válec892"
  Angle = 360
  AttacherType = Attacher::AttachEngine3D
  Height = 20
  Placement = pos=(-117,16,66) rot=(0,1,0;1.5708rad)
  Radius = 2.5
FEATURE [Part::Cylinder] Cylinder893  label="Válec893"
  Angle = 360
  AttacherType = Attacher::AttachEngine3D
  Height = 3
  Placement = pos=(-112,16,66) rot=(0,1,0;1.5708rad)
  Radius = 5
FEATURE [Part::Box] Box423  label="Krychle423"
  AttacherType = Attacher::AttachEngine3D
  Height = 6
  Length = 51
  Placement = pos=(-112,-24,76) rot=(0,0,1;0rad)
  Width = 24
FEATURE [Part::Cylinder] Cylinder894  label="Válec894"
  Angle = 360
  AttacherType = Attacher::AttachEngine3D
  Height = 10
  Placement = pos=(0,0,72) rot=(0,0,1;0rad)
  Radius = 74
FEATURE [Part::Box] Box424  label="Krychle424"
  AttacherType = Attacher::AttachEngine3D
  Height = 26
  Length = 50
  Placement = pos=(-112,-24,56) rot=(0,0,1;0rad)
  Width = 6
FEATURE [Part::Cylinder] Cylinder895  label="Válec895"
  Angle = 360
  AttacherType = Attacher::AttachEngine3D
  Height = 20
  Placement = pos=(-102,-10,66) rot=(0,0,1;0rad)
  Radius = 2.5
FEATURE [Part::Cylinder] Cylinder897  label="Válec897"
  Angle = 360
  AttacherType = Attacher::AttachEngine3D
  Height = 32
  Placement = pos=(0,0,50) rot=(0,0,1;0rad)
  Radius = 74
FEATURE [Part::Cylinder] Cylinder898  label="Válec898"
  Angle = 360
  AttacherType = Attacher::AttachEngine3D
  Height = 20
  Placement = pos=(-86,-10,66) rot=(0,0,1;0rad)
  Radius = 2.5
FEATURE [Part::Box] Box897  label="Krychle897"
  AttacherType = Attacher::AttachEngine3D
  Height = 14
  Length = 24
  Placement = pos=(68,-24,44) rot=(0,0,1;0rad)
  Width = 6
FEATURE [Part::Cylinder] Cylinder961  label="Válec961"
  Angle = 360
  AttacherType = Attacher::AttachEngine3D
  Height = 20
  Placement = pos=(-102,-10,66) rot=(0,0,1;0rad)
  Radius = 2.5
FEATURE [Part::Cylinder] Cylinder962  label="Válec962"
  Angle = 360
  AttacherType = Attacher::AttachEngine3D
  Height = 10
  Placement = pos=(0,0,72) rot=(0,0,1;0rad)
  Radius = 74
FEATURE [Part::Cut] Cut406
  Base = -> Box432
  Tool = -> Cylinder906
FEATURE [Part::Chamfer] Chamfer003
  Base = -> Cut406
  Edges = 1 edges r=20: [Edge4]
FEATURE [Part::Cut] Cut408
  Base = -> Box431
  Tool = -> Cylinder905
FEATURE [Part::Cut] Cut407
  Base = -> Cut408
  Tool = -> Compound498
FEATURE [Part::Cut] Cut409
  Base = -> Box430
  Tool = -> Box426
FEATURE [Part::Cut] Cut410
  Base = -> Cut409
  Tool = -> Compound495
FEATURE [Part::Cut] Cut403
  Base = -> Cut410
  Tool = -> Compound496
FEATURE [Part::Cut] Cut404
  Base = -> Cut403
  Tool = -> Cylinder904
FEATURE [Part::Cut] Cut405
  Base = -> Cut404
  Tool = -> Cylinder903
FEATURE [Part::Chamfer] Chamfer004
  Base = -> Cut405
  Edges = 1 edges r=2: [Edge4]
FEATURE [Part::Compound] Compound497  label="stabilo_holdo_left"
  Links = -> [Chamfer003,Cut407,Chamfer004]
  Placement = pos=(0,0,2) rot=(0,0,1;0rad)
FEATURE [Part::Compound] Compound531  label="stabilo_holdo_left_silo"
  Links = -> [Compound497,Chamfer016]
FEATURE [Part::Compound] Compound1056
  Links = -> [Cylinder1759,Cylinder875,Cylinder876,Cylinder877]
FEATURE [Part::Compound] Compound493
  Links = -> [Cylinder895,Cylinder898]
FEATURE [Part::Cut] Cut521
  Base = -> Box416
  Tool = -> Box417
FEATURE [Part::Cut] Cut392
  Base = -> Cut521
  Tool = -> Compound1055
FEATURE [Part::Cut] Cut393
  Base = -> Cut392
  Tool = -> Compound1056
FEATURE [Part::Cut] Cut398
  Base = -> Cut393
  Tool = -> Cylinder892
FEATURE [Part::Cut] Cut399
  Base = -> Cut398
  Tool = -> Cylinder893
FEATURE [Part::Chamfer] Chamfer002
  Base = -> Cut399
  Edges = 1 edges r=2: [Edge4]
FEATURE [Part::Cut] Cut400
  Base = -> Box423
  Tool = -> Cylinder894
FEATURE [Part::Cut] Cut401
  Base = -> Box424
  Tool = -> Cylinder897
FEATURE [Part::Cut] Cut402
  Base = -> Cut400
  Tool = -> Compound493
FEATURE [Part::Chamfer] Chamfer057
  Base = -> Cut401
  Edges = 1 edges r=20: [Edge4]
FEATURE [Part::Compound] Compound494  label="stabilo_holdo_left1"
  Links = -> [Chamfer057,Cut402,Chamfer002]
FEATURE [Part::Mirroring] mirror  label="stabilo_holdo_right"
  Base = (0,0,0)
  Normal = (1,0,0)
  Placement = pos=(0,0,2) rot=(0,0,1;0rad)
  Source = -> Compound494
FEATURE [Part::Chamfer] Chamfer017
  Base = -> Box897
  Edges = 1 edges r=13.99: [Edge8]
FEATURE [Part::Compound] Compound532  label="stabilo_holdo_right_silo"
  Links = -> [Chamfer017,mirror]
FEATURE [Part::Box] Box476  label="Krychle476"
  AttacherType = Attacher::AttachEngine3D
  Height = 26
  Length = 50
  Placement = pos=(-112,-24,56) rot=(0,0,1;0rad)
  Width = 6
FEATURE [Part::Cylinder] Cylinder963  label="Válec963"
  Angle = 360
  AttacherType = Attacher::AttachEngine3D
  Height = 20
  Placement = pos=(-86,-10,66) rot=(0,0,1;0rad)
  Radius = 2.5
FEATURE [Part::Compound] Compound519
  Links = -> [Cylinder961,Cylinder963]
FEATURE [Part::Cylinder] Cylinder964  label="Válec964"
  Angle = 360
  AttacherType = Attacher::AttachEngine3D
  Height = 32
  Placement = pos=(0,0,50) rot=(0,0,1;0rad)
  Radius = 74
FEATURE [Part::Cut] Cut443
  Base = -> Box476
  Placement = pos=(0,0,0) rot=(0,0,1;1.5708rad)
  Tool = -> Cylinder964
FEATURE [Part::Box] Box477  label="Krychle477"
  AttacherType = Attacher::AttachEngine3D
  Height = 6
  Length = 51
  Placement = pos=(-112,-24,76) rot=(0,0,1;0rad)
  Width = 24
FEATURE [Part::Cylinder] Cylinder965  label="Válec965"
  Angle = 360
  AttacherType = Attacher::AttachEngine3D
  Height = 20
  Placement = pos=(-102,-10,66) rot=(0,0,1;0rad)
  Radius = 2.5
FEATURE [Part::Box] Box478  label="Krychle478"
  AttacherType = Attacher::AttachEngine3D
  Height = 26
  Length = 50
  Placement = pos=(-112,-24,56) rot=(0,0,1;0rad)
  Width = 6
FEATURE [Part::Cylinder] Cylinder966  label="Válec966"
  Angle = 360
  AttacherType = Attacher::AttachEngine3D
  Height = 32
  Placement = pos=(0,0,50) rot=(0,0,1;0rad)
  Radius = 74
FEATURE [Part::Cylinder] Cylinder967  label="Válec967"
  Angle = 360
  AttacherType = Attacher::AttachEngine3D
  Height = 10
  Placement = pos=(0,0,72) rot=(0,0,1;0rad)
  Radius = 74
FEATURE [Part::Box] Box479  label="Krychle479"
  AttacherType = Attacher::AttachEngine3D
  Height = 6
  Length = 51
  Placement = pos=(-112,-24,76) rot=(0,0,1;0rad)
  Width = 24
FEATURE [Part::Cylinder] Cylinder968  label="Válec968"
  Angle = 360
  AttacherType = Attacher::AttachEngine3D
  Height = 20
  Placement = pos=(-86,-10,66) rot=(0,0,1;0rad)
  Radius = 2.5
FEATURE [Part::Compound] Compound522
  Links = -> [Cylinder965,Cylinder968]
FEATURE [Part::Box] Box480  label="Krychle480"
  AttacherType = Attacher::AttachEngine3D
  Height = 26
  Length = 50
  Placement = pos=(3,-112,56) rot=(0,0,1;1.5708rad)
  Width = 6
FEATURE [Part::Cylinder] Cylinder969  label="Válec969"
  Angle = 360
  AttacherType = Attacher::AttachEngine3D
  Height = 40
  Placement = pos=(0,0,42) rot=(0,0,1;0rad)
  Radius = 74
FEATURE [Part::Box] Box481  label="Krychle481"
  AttacherType = Attacher::AttachEngine3D
  Height = 26
  Length = 8
  Placement = pos=(24,-78,56) rot=(0,0,1;1.5708rad)
  Width = 48
FEATURE [Part::Cylinder] Cylinder970  label="Válec970"
  Angle = 360
  AttacherType = Attacher::AttachEngine3D
  Height = 40
  Placement = pos=(0,0,42) rot=(0,0,1;0rad)
  Radius = 74
FEATURE [Part::Box] Box898  label="Krychle898"
  AttacherType = Attacher::AttachEngine3D
  Height = 14
  Length = 18
  Placement = pos=(3,-92,44) rot=(0,0,1;1.5708rad)
  Width = 6
FEATURE [Part::Box] Box899  label="Krychle899"
  AttacherType = Attacher::AttachEngine3D
  Height = 14
  Length = 24
  Placement = pos=(3,-92,44) rot=(0,0,1;1.5708rad)
  Width = 6
FEATURE [Part::Box] Box900  label="Krychle900"
  AttacherType = Attacher::AttachEngine3D
  Height = 14
  Length = 24
  Placement = pos=(3,-92,44) rot=(0,0,1;1.5708rad)
  Width = 6
FEATURE [Part::Cut] Cut445
  Base = -> Box477
  Tool = -> Cylinder962
FEATURE [Part::Cut] Cut444
  Base = -> Cut445
  Placement = pos=(0,0,0) rot=(0,0,1;1.5708rad)
  Tool = -> Compound519
FEATURE [Part::Compound] Compound520
  Links = -> [Cut443,Cut444]
FEATURE [Part::Cut] Cut446
  Base = -> Box478
  Placement = pos=(0,0,0) rot=(0,0,1;1.5708rad)
  Tool = -> Cylinder966
FEATURE [Part::Cut] Cut447
  Base = -> Box479
  Tool = -> Cylinder967
FEATURE [Part::Cut] Cut448
  Base = -> Cut447
  Placement = pos=(0,0,0) rot=(0,0,1;1.5708rad)
  Tool = -> Compound522
FEATURE [Part::Compound] Compound521
  Links = -> [Cut446,Cut448]
FEATURE [Part::Mirroring] mirror003  label="Compound521 (mirrored)"
  Base = (0,0,0)
  Normal = (1,0,0)
  Source = -> Compound521
FEATURE [Part::Chamfer] Chamfer010
  Base = -> mirror003
  Edges = 1 edges r=20: [Edge4]
FEATURE [Part::Cut] Cut449
  Base = -> Box480
  Tool = -> Cylinder969
FEATURE [Part::Chamfer] Chamfer011
  Base = -> Cut449
  Edges = 1 edges r=20: [Edge4]
FEATURE [Part::Chamfer] Chamfer012
  Base = -> Compound520
  Edges = 1 edges r=20: [Edge4]
FEATURE [Part::Chamfer] Chamfer013
  Base = -> Box898
  Edges = 1 edges r=13.99: [Edge4]
FEATURE [Part::Chamfer] Chamfer014
  Base = -> Box899
  Edges = 1 edges r=13.99: [Edge4]
  Placement = pos=(-21,0,0) rot=(0,0,1;0rad)
FEATURE [Part::Chamfer] Chamfer015
  Base = -> Box900
  Edges = 1 edges r=13.99: [Edge4]
  Placement = pos=(21,0,0) rot=(0,0,1;0rad)
FEATURE [Part::Cut] Cut450
  Base = -> Box481
  Tool = -> Cylinder970
FEATURE [Part::Compound] Compound523  label="stabilo_front"
  Links = -> [Chamfer012,Chamfer011,Chamfer010,Cut450]
  Placement = pos=(0,0,2) rot=(0,0,1;0rad)
FEATURE [Part::Compound] Compound533  label="stabilo_front_silo"
  Links = -> [Compound523,Chamfer013,Chamfer014,Chamfer015]
FEATURE [Part::Compound] Compound889  label="Base_turret-hole"
  Links = -> [Cut453,Tube036,Cut509,Cut520,Compound531,Compound532,Compound533]
  Placement = pos=(-31,210,81) rot=(1,0,0;3.14159rad)
FEATURE [Mesh::Feature] Mesh  label="Ele-box_standalone-standard (Meshed)"
FEATURE [Mesh::Feature] Mesh001  label="Ele-box_standalone-anti-standard (Meshed)"
FEATURE [Mesh::Feature] Mesh002  label="Ele-box_big-hold (Meshed)"
FEATURE [Mesh::Feature] Mesh003  label="Ele-box_small-hold-opposite (Meshed)"
FEATURE [Part::Box] Box901  label="Krychle901"
  AttacherType = Attacher::AttachEngine3D
  Height = 20
  Length = 20
  Placement = pos=(-137,88,3) rot=(0,0,1;0rad)
  Width = 118
FEATURE [Part::Part2DObjectPython] ShapeString002  # Draft 2D object (typed FeaturePython)
  FontFile = <path>
  Placement = pos=(250,0,0) rot=(0,0,-1;1.5708rad)
  Size = 18
  String = RealRobot
  Tracking = 0
FEATURE [Part::Part2DObjectPython] ShapeString003  # Draft 2D object (typed FeaturePython)
  FontFile = <path>
  Placement = pos=(250,0,0) rot=(0,0,-1;1.5708rad)
  Size = 16
  String = ONE rev.2
  Tracking = 0
FEATURE [Part::Extrusion] Extrude001  label="turno_RR1"
  Base = -> ShapeString002
  Dir = (0,0,1)
  DirMode = 2
  FaceMakerClass = Part::FaceMakerBullseye
  LengthFwd = 5
  LengthRev = 0
  Placement = pos=(35,282,2) rot=(0.57735,-0.57735,0.57735;4.18879rad)
  Solid = false
  Symmetric = false
FEATURE [Part::Extrusion] Extrude002  label="turno_RR002"
  Base = -> ShapeString003
  Dir = (0,0,1)
  DirMode = 2
  FaceMakerClass = Part::FaceMakerBullseye
  LengthFwd = 5
  LengthRev = 0
  Placement = pos=(35,306,14) rot=(0.57735,-0.57735,0.57735;4.18879rad)
  Solid = false
  Symmetric = false
FEATURE [Part::Box] Box504  label="Krychle504"
  AttacherType = Attacher::AttachEngine3D
  Height = 120
  Length = 5
  Placement = pos=(32,0,-3) rot=(0,0,1;0rad)
  Width = 80
FEATURE [Part::Cylinder] Cylinder1003  label="Válec1003"
  Angle = 360
  AttacherType = Attacher::AttachEngine3D
  Height = 3
  Placement = pos=(26,7,114) rot=(0,1,0;1.5708rad)
  Radius = 3
FEATURE [Part::Cylinder] Cylinder1004  label="Válec1004"
  Angle = 360
  AttacherType = Attacher::AttachEngine3D
  Height = 3
  Placement = pos=(26,73,0) rot=(0,1,0;1.5708rad)
  Radius = 3
FEATURE [Part::Cylinder] Cylinder1005  label="Válec1005"
  Angle = 360
  AttacherType = Attacher::AttachEngine3D
  Height = 3
  Placement = pos=(26,7,0) rot=(0,1,0;1.5708rad)
  Radius = 3
FEATURE [Part::Cylinder] Cylinder1006  label="Válec1006"
  Angle = 360
  AttacherType = Attacher::AttachEngine3D
  Height = 3
  Placement = pos=(26,73,114) rot=(0,1,0;1.5708rad)
  Radius = 3
FEATURE [Part::Compound] Compound534
  Links = -> [Cylinder1005,Cylinder1004,Cylinder1003,Cylinder1006]
  Placement = pos=(8,0,0) rot=(0,0,1;0rad)
FEATURE [Part::Cylinder] Cylinder1007  label="Válec1007"
  Angle = 360
  AttacherType = Attacher::AttachEngine3D
  Height = 100
  Placement = pos=(26,7,0) rot=(0,1,0;1.5708rad)
  Radius = 1.75
FEATURE [Part::Cylinder] Cylinder1008  label="Válec1008"
  Angle = 360
  AttacherType = Attacher::AttachEngine3D
  Height = 100
  Placement = pos=(26,73,0) rot=(0,1,0;1.5708rad)
  Radius = 1.75
FEATURE [Part::Cylinder] Cylinder1009  label="Válec1009"
  Angle = 360
  AttacherType = Attacher::AttachEngine3D
  Height = 100
  Placement = pos=(26,7,114) rot=(0,1,0;1.5708rad)
  Radius = 1.75
FEATURE [Part::Cylinder] Cylinder1010  label="Válec1010"
  Angle = 360
  AttacherType = Attacher::AttachEngine3D
  Height = 100
  Placement = pos=(26,73,114) rot=(0,1,0;1.5708rad)
  Radius = 1.75
FEATURE [Part::Compound] Compound535
  Links = -> [Cylinder1007,Cylinder1008,Cylinder1009,Cylinder1010]
  Placement = pos=(-72,0,0) rot=(0,0,1;0rad)
FEATURE [Part::Cut] Cut673
  Base = -> Box504
  Tool = -> Compound535
FEATURE [Part::Cut] Cut674
  Base = -> Cut673
  Tool = -> Compound534
FEATURE [Part::Chamfer] Chamfer076
  Base = -> Cut674
  Edges = 2 edges r=4: [Edge11,Edge12]
FEATURE [Part::Chamfer] Chamfer077
  Base = -> Chamfer076
  Edges = 2 edges r=4: [Edge12,Edge19]
FEATURE [Part::Chamfer] Chamfer078
  Base = -> Chamfer077
  Edges = 2 edges r=2: [Edge13,Edge36]
FEATURE [Part::Compound] Compound1057
  Links = -> [Extrude001,Extrude002]
FEATURE [Part::Cut] Cut675  label="Ele-box_RealRobotONE-cover"
  Base = -> Chamfer078
  Tool = -> Compound1057
FEATURE [Mesh::Feature] Mesh004  label="Ele-box_RealRobotONE-cover (Meshed)"
FEATURE [Mesh::Feature] Mesh005  label="Ele-box_small-hold (Meshed)"
FEATURE [Mesh::Feature] Mesh006  label="Ele-box_small-hold-opposite (Meshed)001"
FEATURE [Mesh::Feature] Mesh007  label="Ele-box_small-cover (Meshed)"
FEATURE [Mesh::Feature] Mesh008  label="Ele-box_big-hold (Meshed)001"
FEATURE [Mesh::Feature] Mesh009  label="Ele-box_big-cover (Meshed)"
FEATURE [Mesh::Feature] Mesh010  label="Ele-box_standalone-anti-standard (Meshed)001"
FEATURE [Mesh::Feature] Mesh011  label="Ele-box_standalone-standard (Meshed)001"
FEATURE [Part::Cylinder] Cylinder2016  label="Válec2016"
  Angle = 360
  AttacherType = Attacher::AttachEngine3D
  Height = 60
  Placement = pos=(26,13,117) rot=(0,1,0;1.5708rad)
  Radius = 1.75
FEATURE [Part::Cylinder] Cylinder2017  label="Válec2017"
  Angle = 360
  AttacherType = Attacher::AttachEngine3D
  Height = 10
  Placement = pos=(29,6,39) rot=(1,0,0;1.5708rad)
  Radius = 1.5
FEATURE [Part::Box] Box902  label="Krychle902"
  AttacherType = Attacher::AttachEngine3D
  Height = 6
  Length = 2
  Placement = pos=(34,64,0) rot=(0,0,1;0rad)
  Width = 6
FEATURE [Part::Box] Box903  label="Krychle903"
  AttacherType = Attacher::AttachEngine3D
  Height = 6
  Length = 2
  Placement = pos=(34,10,0) rot=(0,0,1;0rad)
  Width = 6
FEATURE [Part::Cylinder] Cylinder2018  label="Válec2018"
  Angle = 360
  AttacherType = Attacher::AttachEngine3D
  Height = 10
  Placement = pos=(29,21,0) rot=(0,0,1;0rad)
  Radius = 1.5
FEATURE [Part::Cylinder] Cylinder2019  label="Válec2019"
  Angle = 360
  AttacherType = Attacher::AttachEngine3D
  Height = 10
  Placement = pos=(29,43,0) rot=(0,0,1;0rad)
  Radius = 1.5
FEATURE [Part::Cylinder] Cylinder2020  label="Válec2020"
  Angle = 360
  AttacherType = Attacher::AttachEngine3D
  Height = 10
  Placement = pos=(16,82,66) rot=(1,0,0;1.5708rad)
  Radius = 9
FEATURE [Part::Box] Box904  label="Krychle904"
  AttacherType = Attacher::AttachEngine3D
  Height = 6
  Length = 2
  Placement = pos=(34,10,114) rot=(0,0,1;0rad)
  Width = 6
FEATURE [Part::Box] Box905  label="Krychle905"
  AttacherType = Attacher::AttachEngine3D
  Height = 2
  Length = 6
  Placement = pos=(0,40,3) rot=(0,0,1;0rad)
  Width = 6
FEATURE [Part::Box] Box906  label="Krychle906"
  AttacherType = Attacher::AttachEngine3D
  Height = 3
  Length = 8
  Placement = pos=(12,-2,39) rot=(0,0,1;0rad)
  Width = 10
FEATURE [Part::Box] Box907  label="Krychle907"
  AttacherType = Attacher::AttachEngine3D
  Height = 6
  Length = 2
  Placement = pos=(34,10,114) rot=(0,0,1;0rad)
  Width = 6
FEATURE [Part::Cylinder] Cylinder2021  label="Válec2021"
  Angle = 360
  AttacherType = Attacher::AttachEngine3D
  Height = 10
  Placement = pos=(16,6,18) rot=(1,0,0;1.5708rad)
  Radius = 8
FEATURE [Part::Box] Box908  label="Krychle908"
  AttacherType = Attacher::AttachEngine3D
  Height = 21
  Length = 17.5
  Placement = pos=(10.75,-2,42) rot=(0,0,1;0rad)
  Width = 10
FEATURE [Part::Chamfer] Chamfer079
  Base = -> Box908
  Edges = 1 edges r=3: [Edge2]
  Placement = pos=(-4,0,0) rot=(0,0,1;0rad)
FEATURE [Part::Box] Box909  label="Krychle909"
  AttacherType = Attacher::AttachEngine3D
  Height = 6
  Length = 2
  Placement = pos=(34,10,0) rot=(0,0,1;0rad)
  Width = 6
FEATURE [Part::Box] Box910  label="Krychle910"
  AttacherType = Attacher::AttachEngine3D
  Height = 108
  Length = 30
  Placement = pos=(2,4,3) rot=(0,0,1;0rad)
  Width = 72
FEATURE [Part::Box] Box911  label="Krychle911"
  AttacherType = Attacher::AttachEngine3D
  Height = 6
  Length = 2
  Placement = pos=(34,64,114) rot=(0,0,1;0rad)
  Width = 6
FEATURE [Part::Cylinder] Cylinder2022  label="Válec2022"
  Angle = 360
  AttacherType = Attacher::AttachEngine3D
  Height = 60
  Placement = pos=(26,13,3) rot=(0,1,0;1.5708rad)
  Radius = 1.75
FEATURE [Part::Cylinder] Cylinder2023  label="Válec2023"
  Angle = 360
  AttacherType = Attacher::AttachEngine3D
  Height = 3
  Placement = pos=(26,7,3) rot=(0,1,0;1.5708rad)
  Radius = 3
FEATURE [Part::Cylinder] Cylinder2024  label="Válec2024"
  Angle = 360
  AttacherType = Attacher::AttachEngine3D
  Height = 10
  Placement = pos=(3,43,0) rot=(0,0,1;0rad)
  Radius = 1.5
FEATURE [Part::Cylinder] Cylinder2025  label="Válec2025"
  Angle = 360
  AttacherType = Attacher::AttachEngine3D
  Height = 3
  Placement = pos=(26,73,3) rot=(0,1,0;1.5708rad)
  Radius = 3
FEATURE [Part::Cylinder] Cylinder2026  label="Válec2026"
  Angle = 360
  AttacherType = Attacher::AttachEngine3D
  Height = 60
  Placement = pos=(26,13,3) rot=(0,1,0;1.5708rad)
  Radius = 1.75
FEATURE [Part::Box] Box912  label="Krychle912"
  AttacherType = Attacher::AttachEngine3D
  Height = 2
  Length = 6
  Placement = pos=(26,18,3) rot=(0,0,1;0rad)
  Width = 6
FEATURE [Part::Cylinder] Cylinder2027  label="Válec2027"
  Angle = 360
  AttacherType = Attacher::AttachEngine3D
  Height = 10
  Placement = pos=(3,21,0) rot=(0,0,1;0rad)
  Radius = 1.5
FEATURE [Part::Compound] Compound1072
  Links = -> [Cylinder2027,Cylinder2024,Cylinder2018,Cylinder2019]
  Placement = pos=(0,0,-100) rot=(0,0,1;0rad)
FEATURE [Part::Cylinder] Cylinder2028  label="Válec2028"
  Angle = 360
  AttacherType = Attacher::AttachEngine3D
  Height = 60
  Placement = pos=(26,67,117) rot=(0,1,0;1.5708rad)
  Radius = 1.75
FEATURE [Part::Cylinder] Cylinder2029  label="Válec2029"
  Angle = 360
  AttacherType = Attacher::AttachEngine3D
  Height = 100
  Placement = pos=(26,73,117) rot=(0,1,0;1.5708rad)
  Radius = 1.75
FEATURE [Part::Cylinder] Cylinder2030  label="Válec2030"
  Angle = 360
  AttacherType = Attacher::AttachEngine3D
  Height = 60
  Placement = pos=(26,13,117) rot=(0,1,0;1.5708rad)
  Radius = 1.75
FEATURE [Part::Cylinder] Cylinder2031  label="Válec2031"
  Angle = 360
  AttacherType = Attacher::AttachEngine3D
  Height = 60
  Placement = pos=(26,67,3) rot=(0,1,0;1.5708rad)
  Radius = 1.75
FEATURE [Part::Compound] Compound1064
  Links = -> [Cylinder2022,Cylinder2031,Cylinder2016,Cylinder2028]
  Placement = pos=(-8,0,-3) rot=(0,0,1;0rad)
FEATURE [Part::Cylinder] Cylinder2032  label="Válec2032"
  Angle = 360
  AttacherType = Attacher::AttachEngine3D
  Height = 60
  Placement = pos=(26,67,3) rot=(0,1,0;1.5708rad)
  Radius = 1.75
FEATURE [Part::Box] Box913  label="Krychle913"
  AttacherType = Attacher::AttachEngine3D
  Height = 6
  Length = 2
  Placement = pos=(26,80,25) rot=(0,0,1;0rad)
  Width = 6
FEATURE [Part::Cylinder] Cylinder2033  label="Válec2033"
  Angle = 360
  AttacherType = Attacher::AttachEngine3D
  Height = 60
  Placement = pos=(26,67,117) rot=(0,1,0;1.5708rad)
  Radius = 1.75
FEATURE [Part::Compound] Compound1067
  Links = -> [Cylinder2026,Cylinder2032,Cylinder2030,Cylinder2033]
  Placement = pos=(-72,0,-3) rot=(0,0,1;0rad)
FEATURE [Part::Box] Box914  label="Krychle914"
  AttacherType = Attacher::AttachEngine3D
  Height = 6
  Length = 2
  Placement = pos=(26,80,46) rot=(0,0,1;0rad)
  Width = 6
FEATURE [Part::Cylinder] Cylinder2034  label="Válec2034"
  Angle = 360
  AttacherType = Attacher::AttachEngine3D
  Height = 20
  Placement = pos=(24.5,77,20) rot=(0,0,1;0rad)
  Radius = 2
FEATURE [Part::Cylinder] Cylinder2035  label="Válec2035"
  Angle = 360
  AttacherType = Attacher::AttachEngine3D
  Height = 3
  Placement = pos=(26,73,3) rot=(0,1,0;1.5708rad)
  Radius = 3
FEATURE [Part::Box] Box915  label="Krychle915"
  AttacherType = Attacher::AttachEngine3D
  Height = 6
  Length = 2
  Placement = pos=(34,64,114) rot=(0,0,1;0rad)
  Width = 6
FEATURE [Part::Compound] Compound1069
  Links = -> [Box909,Box902,Box907,Box915]
  Placement = pos=(-8,0,-3) rot=(0,0,1;0rad)
FEATURE [Part::Cylinder] Cylinder2036  label="Válec2036"
  Angle = 360
  AttacherType = Attacher::AttachEngine3D
  Height = 10
  Placement = pos=(10,6,63) rot=(1,0,0;1.5708rad)
  Radius = 1.5
FEATURE [Part::Compound] Compound1060
  Links = -> [Cylinder2036,Cylinder2017]
  Placement = pos=(-4,0,0) rot=(0,0,1;0rad)
FEATURE [Part::Box] Box916  label="Krychle916"
  AttacherType = Attacher::AttachEngine3D
  Height = 2
  Length = 6
  Placement = pos=(0,18,3) rot=(0,0,1;0rad)
  Width = 6
FEATURE [Part::Cylinder] Cylinder2037  label="Válec2037"
  Angle = 360
  AttacherType = Attacher::AttachEngine3D
  Height = 100
  Placement = pos=(26,7,3) rot=(0,1,0;1.5708rad)
  Radius = 1.75
FEATURE [Part::Box] Box917  label="Krychle917"
  AttacherType = Attacher::AttachEngine3D
  Height = 120
  Length = 32
  Placement = pos=(0,0,-3) rot=(0,0,1;0rad)
  Width = 80
FEATURE [Part::Cut] Cut676
  Base = -> Box917
  Tool = -> Box910
FEATURE [Part::Cut] Cut690
  Base = -> Cut676
  Tool = -> Compound1069
FEATURE [Part::Cut] Cut694
  Base = -> Cut690
  Tool = -> Compound1064
FEATURE [Part::Cut] Cut689
  Base = -> Cut694
  Tool = -> Cylinder2020
FEATURE [Part::Cut] Cut683
  Base = -> Cut689
  Tool = -> Chamfer079
FEATURE [Part::Cut] Cut693
  Base = -> Cut683
  Tool = -> Compound1060
FEATURE [Part::Cut] Cut697
  Base = -> Cut693
  Tool = -> Box906
FEATURE [Part::Cut] Cut679
  Base = -> Cut697
  Tool = -> Cylinder2021
FEATURE [Part::Box] Box918  label="Krychle918"
  AttacherType = Attacher::AttachEngine3D
  Height = 6
  Length = 2
  Placement = pos=(26,68,46) rot=(0,0,1;0rad)
  Width = 6
FEATURE [Part::Cylinder] Cylinder2038  label="Válec2038"
  Angle = 360
  AttacherType = Attacher::AttachEngine3D
  Height = 100
  Placement = pos=(26,7,117) rot=(0,1,0;1.5708rad)
  Radius = 1.75
FEATURE [Part::Cylinder] Cylinder2039  label="Válec2039"
  Angle = 360
  AttacherType = Attacher::AttachEngine3D
  Height = 20
  Placement = pos=(20,71,28) rot=(0,1,0;1.5708rad)
  Radius = 1.5
FEATURE [Part::Box] Box919  label="Krychle919"
  AttacherType = Attacher::AttachEngine3D
  Height = 2
  Length = 6
  Placement = pos=(26,40,3) rot=(0,0,1;0rad)
  Width = 6
FEATURE [Part::Compound] Compound1058
  Links = -> [Box916,Box905,Box919,Box912]
  Placement = pos=(0,0,-100) rot=(0,0,1;0rad)
FEATURE [Part::Cut] Cut678
  Base = -> Cut679
  Tool = -> Compound1058
FEATURE [Part::Cut] Cut696
  Base = -> Cut678
  Tool = -> Compound1072
FEATURE [Part::Cylinder] Cylinder2040  label="Válec2040"
  Angle = 360
  AttacherType = Attacher::AttachEngine3D
  Height = 3
  Placement = pos=(26,7,117) rot=(0,1,0;1.5708rad)
  Radius = 3
FEATURE [Part::Cylinder] Cylinder2041  label="Válec2041"
  Angle = 360
  AttacherType = Attacher::AttachEngine3D
  Height = 3
  Placement = pos=(26,7,3) rot=(0,1,0;1.5708rad)
  Radius = 3
FEATURE [Part::Cylinder] Cylinder2042  label="Válec2042"
  Angle = 360
  AttacherType = Attacher::AttachEngine3D
  Height = 3
  Placement = pos=(26,73,117) rot=(0,1,0;1.5708rad)
  Radius = 3
FEATURE [Part::Box] Box920  label="Krychle920"
  AttacherType = Attacher::AttachEngine3D
  Height = 6
  Length = 2
  Placement = pos=(26,68,25) rot=(0,0,1;0rad)
  Width = 6
FEATURE [Part::Compound] Compound1059
  Links = -> [Box913,Box920,Box914,Box918]
  Placement = pos=(1,0,0) rot=(0,0,1;0rad)
FEATURE [Part::Cylinder] Cylinder2043  label="Válec2043"
  Angle = 360
  AttacherType = Attacher::AttachEngine3D
  Height = 100
  Placement = pos=(26,73,3) rot=(0,1,0;1.5708rad)
  Radius = 1.75
FEATURE [Part::Compound] Compound1068
  Links = -> [Cylinder2037,Cylinder2043,Cylinder2038,Cylinder2029]
  Placement = pos=(-72,0,-3) rot=(0,0,1;0rad)
FEATURE [Part::Cylinder] Cylinder2044  label="Válec2044"
  Angle = 360
  AttacherType = Attacher::AttachEngine3D
  Height = 20
  Placement = pos=(20,71,49) rot=(0,1,0;1.5708rad)
  Radius = 1.5
FEATURE [Part::Box] Box921  label="Krychle921"
  AttacherType = Attacher::AttachEngine3D
  Height = 27
  Length = 19
  Placement = pos=(13,64,25) rot=(0,0,1;0rad)
  Width = 24
FEATURE [Part::Cylinder] Cylinder2045  label="Válec2045"
  Angle = 360
  AttacherType = Attacher::AttachEngine3D
  Height = 3
  Placement = pos=(26,73,117) rot=(0,1,0;1.5708rad)
  Radius = 3
FEATURE [Part::Compound] Compound1061
  Links = -> [Cylinder2041,Cylinder2035,Cylinder2040,Cylinder2045]
  Placement = pos=(3,0,-3) rot=(0,0,1;0rad)
FEATURE [Part::Box] Box922  label="Krychle922"
  AttacherType = Attacher::AttachEngine3D
  Height = 6
  Length = 2
  Placement = pos=(34,64,0) rot=(0,0,1;0rad)
  Width = 6
FEATURE [Part::Compound] Compound1071
  Links = -> [Box903,Box922,Box904,Box911]
  Placement = pos=(-30,0,-3) rot=(0,0,1;0rad)
FEATURE [Part::Cut] Cut677
  Base = -> Cut696
  Tool = -> Compound1071
FEATURE [Part::Cut] Cut691
  Base = -> Cut677
  Tool = -> Compound1067
FEATURE [Part::Cut] Cut695
  Base = -> Cut691
  Tool = -> Compound1068
FEATURE [Part::Cut] Cut680
  Base = -> Cut695
  Tool = -> Compound1061
FEATURE [Part::Cylinder] Cylinder2046  label="Válec2046"
  Angle = 360
  AttacherType = Attacher::AttachEngine3D
  Height = 20
  Placement = pos=(20,83,49) rot=(0,1,0;1.5708rad)
  Radius = 1.5
FEATURE [Part::Cylinder] Cylinder2047  label="Válec2047"
  Angle = 360
  AttacherType = Attacher::AttachEngine3D
  Height = 3
  Placement = pos=(26,7,117) rot=(0,1,0;1.5708rad)
  Radius = 3
FEATURE [Part::Compound] Compound1066
  Links = -> [Cylinder2023,Cylinder2025,Cylinder2047,Cylinder2042]
  Placement = pos=(-26,0,-3) rot=(0,0,1;0rad)
FEATURE [Part::Cut] Cut681
  Base = -> Cut680
  Tool = -> Compound1066
FEATURE [Part::Box] Box923  label="Krychle923"
  AttacherType = Attacher::AttachEngine3D
  Height = 4
  Length = 32
  Placement = pos=(0,4,32) rot=(0,0,1;0rad)
  Width = 60
FEATURE [Part::Box] Box924  label="Krychle924"
  AttacherType = Attacher::AttachEngine3D
  Height = 27
  Length = 13
  Placement = pos=(0,64,25) rot=(0,0,1;0rad)
  Width = 24
FEATURE [Part::Chamfer] Chamfer080
  Base = -> Box924
  Edges = 1 edges r=12.9: [Edge3]
FEATURE [Part::Cylinder] Cylinder2048  label="Válec2048"
  Angle = 360
  AttacherType = Attacher::AttachEngine3D
  Height = 20
  Placement = pos=(24.5,77,38) rot=(0,0,1;0rad)
  Radius = 2
FEATURE [Part::Cylinder] Cylinder  label="Válec"
  Angle = 360
  AttacherType = Attacher::AttachEngine3D
  Height = 20
  Placement = pos=(4,24,-8) rot=(0,0,1;0rad)
  Radius = 2.5
FEATURE [Part::Box] Box925  label="Krychle925"
  AttacherType = Attacher::AttachEngine3D
  Height = 44
  Length = 32
  Placement = pos=(0,60,36) rot=(0,0,1;0rad)
  Width = 4
FEATURE [Part::Cylinder] Cylinder2049  label="Válec2049"
  Angle = 360
  AttacherType = Attacher::AttachEngine3D
  Height = 20
  Placement = pos=(20,83,28) rot=(0,1,0;1.5708rad)
  Radius = 1.5
FEATURE [Part::Compound] Compound1065
  Links = -> [Cylinder2039,Cylinder2049,Cylinder2044,Cylinder2046]
FEATURE [Part::Box] Box926  label="Krychle926"
  AttacherType = Attacher::AttachEngine3D
  Height = 15
  Length = 15
  Placement = pos=(17,68,31) rot=(0,0,1;0rad)
  Width = 80
FEATURE [Part::Cut] Cut687
  Base = -> Box921
  Tool = -> Box926
FEATURE [Part::Cut] Cut684
  Base = -> Cut687
  Tool = -> Compound1059
FEATURE [Part::Cut] Cut686
  Base = -> Cut684
  Tool = -> Compound1065
FEATURE [Part::Cut] Cut688
  Base = -> Cut686
  Tool = -> Cylinder2034
FEATURE [Part::Cylinder] Cylinder2050  label="Válec2050"
  Angle = 360
  AttacherType = Attacher::AttachEngine3D
  Height = 3
  Placement = pos=(24.5,77,49) rot=(0,0,1;0rad)
  Radius = 4
FEATURE [Part::Box] Box927  label="Krychle927"
  AttacherType = Attacher::AttachEngine3D
  Height = 4
  Length = 32
  Placement = pos=(0,60,80) rot=(0,0,1;0rad)
  Width = 16
FEATURE [Part::Compound] Compound1063  label="Ele-box_separator004"
  Links = -> [Box923,Box925,Box927]
FEATURE [Part::Chamfer] Chamfer081
  Base = -> Compound1063
  Edges = 2 edges r=3: [Edge11,Edge34]
FEATURE [Part::Cylinder] Cylinder2051  label="Válec2051"
  Angle = 360
  AttacherType = Attacher::AttachEngine3D
  Height = 3
  Placement = pos=(24.5,77,25) rot=(0,0,1;0rad)
  Radius = 4
FEATURE [Part::Cut] Cut698
  Base = -> Cut688
  Tool = -> Cylinder2051
FEATURE [Part::Cut] Cut682
  Base = -> Cut698
  Tool = -> Cylinder2050
FEATURE [Part::Cut] Cut692
  Base = -> Cut682
  Tool = -> Cylinder2048
FEATURE [Part::Compound] Compound1062  label="Ele-box_small-extrusion002"
  Links = -> [Chamfer080,Cut692]
  Placement = pos=(0,16,0) rot=(0,0,1;0rad)
FEATURE [Part::Cylinder] Cylinder2052  label="Válec2052"
  Angle = 360
  AttacherType = Attacher::AttachEngine3D
  Height = 10
  Placement = pos=(16,82,97) rot=(1,0,0;1.5708rad)
  Radius = 9
FEATURE [Part::Cut] Cut685
  Base = -> Cut681
  Tool = -> Cylinder2052
FEATURE [Part::Chamfer] Chamfer082
  Base = -> Cut685
  Edges = 4 edges r=4: [Edge19,Edge22,Edge44,Edge48]
FEATURE [Part::Compound] Compound1070  label="Ele-box_standard1"
  Links = -> [Chamfer082,Chamfer081]
FEATURE [Part::Box] Box928  label="Krychle928"
  AttacherType = Attacher::AttachEngine3D
  Height = 3
  Length = 8
  Placement = pos=(0,20,0) rot=(0,0,1;0rad)
  Width = 8
FEATURE [Part::Cut] Cut493
  Base = -> Compound1070
  Tool = -> Box928
FEATURE [Part::Cut] Cut494  label="Ele-box_standard002"
  Base = -> Cut493
  Tool = -> Cylinder
FEATURE [Part::Compound] Compound1073  label="Ele-box_small-hold-hole"
  Links = -> [Compound1062,Cut494]
FEATURE [Part::Cylinder] Cylinder2053  label="Válec2053"
  Angle = 360
  AttacherType = Attacher::AttachEngine3D
  Height = 100
  Placement = pos=(26,7,117) rot=(0,1,0;1.5708rad)
  Radius = 1.75
FEATURE [Part::Cylinder] Cylinder2054  label="Válec2054"
  Angle = 360
  AttacherType = Attacher::AttachEngine3D
  Height = 100
  Placement = pos=(26,7,3) rot=(0,1,0;1.5708rad)
  Radius = 1.75
FEATURE [Part::Cylinder] Cylinder2055  label="Válec2055"
  Angle = 360
  AttacherType = Attacher::AttachEngine3D
  Height = 20
  Placement = pos=(20,83,49) rot=(0,1,0;1.5708rad)
  Radius = 1.5
FEATURE [Part::Cylinder] Cylinder2056  label="Válec2056"
  Angle = 360
  AttacherType = Attacher::AttachEngine3D
  Height = 100
  Placement = pos=(26,73,3) rot=(0,1,0;1.5708rad)
  Radius = 1.75
FEATURE [Part::Cylinder] Cylinder2057  label="Válec2057"
  Angle = 360
  AttacherType = Attacher::AttachEngine3D
  Height = 10
  Placement = pos=(10,6,63) rot=(1,0,0;1.5708rad)
  Radius = 1.5
FEATURE [Part::Cylinder] Cylinder2058  label="Válec2058"
  Angle = 360
  AttacherType = Attacher::AttachEngine3D
  Height = 3
  Placement = pos=(26,73,3) rot=(0,1,0;1.5708rad)
  Radius = 3
FEATURE [Part::Cylinder] Cylinder2059  label="Válec2059"
  Angle = 360
  AttacherType = Attacher::AttachEngine3D
  Height = 100
  Placement = pos=(26,73,117) rot=(0,1,0;1.5708rad)
  Radius = 1.75
FEATURE [Part::Cylinder] Cylinder2060  label="Válec2060"
  Angle = 360
  AttacherType = Attacher::AttachEngine3D
  Height = 3
  Placement = pos=(26,73,117) rot=(0,1,0;1.5708rad)
  Radius = 3
FEATURE [Part::Cylinder] Cylinder2061  label="Válec2061"
  Angle = 360
  AttacherType = Attacher::AttachEngine3D
  Height = 3
  Placement = pos=(26,7,117) rot=(0,1,0;1.5708rad)
  Radius = 3
FEATURE [Part::Cylinder] Cylinder2062  label="Válec2062"
  Angle = 360
  AttacherType = Attacher::AttachEngine3D
  Height = 10
  Placement = pos=(3,21,0) rot=(0,0,1;0rad)
  Radius = 1.5
FEATURE [Part::Box] Box929  label="Krychle929"
  AttacherType = Attacher::AttachEngine3D
  Height = 120
  Length = 32
  Placement = pos=(0,0,-3) rot=(0,0,1;0rad)
  Width = 80
FEATURE [Part::Cylinder] Cylinder2063  label="Válec2063"
  Angle = 360
  AttacherType = Attacher::AttachEngine3D
  Height = 3
  Placement = pos=(26,7,3) rot=(0,1,0;1.5708rad)
  Radius = 3
FEATURE [Part::Cylinder] Cylinder2064  label="Válec2064"
  Angle = 360
  AttacherType = Attacher::AttachEngine3D
  Height = 60
  Placement = pos=(26,67,3) rot=(0,1,0;1.5708rad)
  Radius = 1.75
FEATURE [Part::Cylinder] Cylinder2065  label="Válec2065"
  Angle = 360
  AttacherType = Attacher::AttachEngine3D
  Height = 10
  Placement = pos=(29,43,0) rot=(0,0,1;0rad)
  Radius = 1.5
FEATURE [Part::Box] Box930  label="Krychle930"
  AttacherType = Attacher::AttachEngine3D
  Height = 2
  Length = 6
  Placement = pos=(0,18,3) rot=(0,0,1;0rad)
  Width = 6
FEATURE [Part::Cylinder] Cylinder2066  label="Válec2066"
  Angle = 360
  AttacherType = Attacher::AttachEngine3D
  Height = 60
  Placement = pos=(26,13,3) rot=(0,1,0;1.5708rad)
  Radius = 1.75
FEATURE [Part::Box] Box931  label="Krychle931"
  AttacherType = Attacher::AttachEngine3D
  Height = 2
  Length = 6
  Placement = pos=(26,40,3) rot=(0,0,1;0rad)
  Width = 6
FEATURE [Part::Box] Box932  label="Krychle932"
  AttacherType = Attacher::AttachEngine3D
  Height = 6
  Length = 2
  Placement = pos=(26,68,46) rot=(0,0,1;0rad)
  Width = 6
FEATURE [Part::Cylinder] Cylinder2067  label="Válec2067"
  Angle = 360
  AttacherType = Attacher::AttachEngine3D
  Height = 20
  Placement = pos=(20,71,49) rot=(0,1,0;1.5708rad)
  Radius = 1.5
FEATURE [Part::Box] Box933  label="Krychle933"
  AttacherType = Attacher::AttachEngine3D
  Height = 6
  Length = 2
  Placement = pos=(26,68,25) rot=(0,0,1;0rad)
  Width = 6
FEATURE [Part::Box] Box934  label="Krychle934"
  AttacherType = Attacher::AttachEngine3D
  Height = 4
  Length = 32
  Placement = pos=(0,4,32) rot=(0,0,1;0rad)
  Width = 60
FEATURE [Part::Cylinder] Cylinder2068  label="Válec2068"
  Angle = 360
  AttacherType = Attacher::AttachEngine3D
  Height = 20
  Placement = pos=(24.5,77,20) rot=(0,0,1;0rad)
  Radius = 2
FEATURE [Part::Cylinder] Cylinder2069  label="Válec2069"
  Angle = 360
  AttacherType = Attacher::AttachEngine3D
  Height = 20
  Placement = pos=(24.5,77,38) rot=(0,0,1;0rad)
  Radius = 2
FEATURE [Part::Cylinder] Cylinder2070  label="Válec2070"
  Angle = 360
  AttacherType = Attacher::AttachEngine3D
  Height = 3
  Placement = pos=(26,73,117) rot=(0,1,0;1.5708rad)
  Radius = 3
FEATURE [Part::Box] Box935  label="Krychle935"
  AttacherType = Attacher::AttachEngine3D
  Height = 15
  Length = 15
  Placement = pos=(17,68,31) rot=(0,0,1;0rad)
  Width = 80
FEATURE [Part::Cylinder] Cylinder2071  label="Válec2071"
  Angle = 360
  AttacherType = Attacher::AttachEngine3D
  Height = 3
  Placement = pos=(24.5,77,49) rot=(0,0,1;0rad)
  Radius = 4
FEATURE [Part::Box] Box936  label="Krychle936"
  AttacherType = Attacher::AttachEngine3D
  Height = 27
  Length = 19
  Placement = pos=(13,64,25) rot=(0,0,1;0rad)
  Width = 24
FEATURE [Part::Box] Box937  label="Krychle937"
  AttacherType = Attacher::AttachEngine3D
  Height = 6
  Length = 2
  Placement = pos=(26,80,46) rot=(0,0,1;0rad)
  Width = 6
FEATURE [Part::Cylinder] Cylinder2072  label="Válec2072"
  Angle = 360
  AttacherType = Attacher::AttachEngine3D
  Height = 20
  Placement = pos=(20,83,28) rot=(0,1,0;1.5708rad)
  Radius = 1.5
FEATURE [Part::Box] Box938  label="Krychle938"
  AttacherType = Attacher::AttachEngine3D
  Height = 6
  Length = 2
  Placement = pos=(34,64,0) rot=(0,0,1;0rad)
  Width = 6
FEATURE [Part::Cylinder] Cylinder2073  label="Válec2073"
  Angle = 360
  AttacherType = Attacher::AttachEngine3D
  Height = 60
  Placement = pos=(26,67,117) rot=(0,1,0;1.5708rad)
  Radius = 1.75
FEATURE [Part::Cylinder] Cylinder2074  label="Válec2074"
  Angle = 360
  AttacherType = Attacher::AttachEngine3D
  Height = 3
  Placement = pos=(24.5,77,25) rot=(0,0,1;0rad)
  Radius = 4
FEATURE [Part::Box] Box939  label="Krychle939"
  AttacherType = Attacher::AttachEngine3D
  Height = 6
  Length = 2
  Placement = pos=(26,80,25) rot=(0,0,1;0rad)
  Width = 6
FEATURE [Part::Compound] Compound1076
  Links = -> [Box939,Box933,Box937,Box932]
  Placement = pos=(1,0,0) rot=(0,0,1;0rad)
FEATURE [Part::Cylinder] Cylinder2075  label="Válec2075"
  Angle = 360
  AttacherType = Attacher::AttachEngine3D
  Height = 20
  Placement = pos=(20,71,28) rot=(0,1,0;1.5708rad)
  Radius = 1.5
FEATURE [Part::Compound] Compound1074
  Links = -> [Cylinder2075,Cylinder2072,Cylinder2067,Cylinder2055]
FEATURE [Part::Cylinder] Cylinder2076  label="Válec2076"
  Angle = 360
  AttacherType = Attacher::AttachEngine3D
  Height = 3
  Placement = pos=(26,7,117) rot=(0,1,0;1.5708rad)
  Radius = 3
FEATURE [Part::Box] Box940  label="Krychle940"
  AttacherType = Attacher::AttachEngine3D
  Height = 27
  Length = 13
  Placement = pos=(0,64,25) rot=(0,0,1;0rad)
  Width = 24
FEATURE [Part::Chamfer] Chamfer083
  Base = -> Box940
  Edges = 1 edges r=12.9: [Edge3]
FEATURE [Part::Box] Box941  label="Krychle941"
  AttacherType = Attacher::AttachEngine3D
  Height = 4
  Length = 32
  Placement = pos=(0,60,80) rot=(0,0,1;0rad)
  Width = 16
FEATURE [Part::Cylinder] Cylinder2077  label="Válec2077"
  Angle = 360
  AttacherType = Attacher::AttachEngine3D
  Height = 10
  Placement = pos=(16,82,97) rot=(1,0,0;1.5708rad)
  Radius = 9
FEATURE [Part::Box] Box942  label="Krychle942"
  AttacherType = Attacher::AttachEngine3D
  Height = 44
  Length = 32
  Placement = pos=(0,60,36) rot=(0,0,1;0rad)
  Width = 4
FEATURE [Part::Compound] Compound1077  label="Ele-box_separator005"
  Links = -> [Box934,Box942,Box941]
FEATURE [Part::Box] Box943  label="Krychle943"
  AttacherType = Attacher::AttachEngine3D
  Height = 3
  Length = 8
  Placement = pos=(0,20,0) rot=(0,0,1;0rad)
  Width = 8
FEATURE [Part::Cylinder] Cylinder2078  label="Válec2078"
  Angle = 360
  AttacherType = Attacher::AttachEngine3D
  Height = 60
  Placement = pos=(26,13,3) rot=(0,1,0;1.5708rad)
  Radius = 1.75
FEATURE [Part::Cylinder] Cylinder2079  label="Válec2079"
  Angle = 360
  AttacherType = Attacher::AttachEngine3D
  Height = 10
  Placement = pos=(16,6,18) rot=(1,0,0;1.5708rad)
  Radius = 8
FEATURE [Part::Box] Box944  label="Krychle944"
  AttacherType = Attacher::AttachEngine3D
  Height = 108
  Length = 30
  Placement = pos=(2,4,3) rot=(0,0,1;0rad)
  Width = 72
FEATURE [Part::Cut] Cut711
  Base = -> Box929
  Tool = -> Box944
FEATURE [Part::Box] Box945  label="Krychle945"
  AttacherType = Attacher::AttachEngine3D
  Height = 6
  Length = 2
  Placement = pos=(34,64,114) rot=(0,0,1;0rad)
  Width = 6
FEATURE [Part::Cylinder] Cylinder2080  label="Válec2080"
  Angle = 360
  AttacherType = Attacher::AttachEngine3D
  Height = 60
  Placement = pos=(26,13,117) rot=(0,1,0;1.5708rad)
  Radius = 1.75
FEATURE [Part::Cylinder] Cylinder2081  label="Válec2081"
  Angle = 360
  AttacherType = Attacher::AttachEngine3D
  Height = 10
  Placement = pos=(3,43,0) rot=(0,0,1;0rad)
  Radius = 1.5
FEATURE [Part::Box] Box946  label="Krychle946"
  AttacherType = Attacher::AttachEngine3D
  Height = 6
  Length = 2
  Placement = pos=(34,10,0) rot=(0,0,1;0rad)
  Width = 6
FEATURE [Part::Cylinder] Cylinder2082  label="Válec2082"
  Angle = 360
  AttacherType = Attacher::AttachEngine3D
  Height = 10
  Placement = pos=(29,6,39) rot=(1,0,0;1.5708rad)
  Radius = 1.5
FEATURE [Part::Cylinder] Cylinder2083  label="Válec2083"
  Angle = 360
  AttacherType = Attacher::AttachEngine3D
  Height = 20
  Placement = pos=(4,24,-8) rot=(0,0,1;0rad)
  Radius = 2.5
FEATURE [Part::Box] Box947  label="Krychle947"
  AttacherType = Attacher::AttachEngine3D
  Height = 6
  Length = 2
  Placement = pos=(34,64,0) rot=(0,0,1;0rad)
  Width = 6
FEATURE [Part::Box] Box948  label="Krychle948"
  AttacherType = Attacher::AttachEngine3D
  Height = 2
  Length = 6
  Placement = pos=(26,18,3) rot=(0,0,1;0rad)
  Width = 6
FEATURE [Part::Box] Box949  label="Krychle949"
  AttacherType = Attacher::AttachEngine3D
  Height = 6
  Length = 2
  Placement = pos=(34,64,114) rot=(0,0,1;0rad)
  Width = 6
FEATURE [Part::Box] Box950  label="Krychle950"
  AttacherType = Attacher::AttachEngine3D
  Height = 3
  Length = 8
  Placement = pos=(12,-2,39) rot=(0,0,1;0rad)
  Width = 10
FEATURE [Part::Cylinder] Cylinder2084  label="Válec2084"
  Angle = 360
  AttacherType = Attacher::AttachEngine3D
  Height = 3
  Placement = pos=(26,73,3) rot=(0,1,0;1.5708rad)
  Radius = 3
FEATURE [Part::Cylinder] Cylinder2085  label="Válec2085"
  Angle = 360
  AttacherType = Attacher::AttachEngine3D
  Height = 10
  Placement = pos=(16,82,66) rot=(1,0,0;1.5708rad)
  Radius = 9
FEATURE [Part::Box] Box951  label="Krychle951"
  AttacherType = Attacher::AttachEngine3D
  Height = 6
  Length = 2
  Placement = pos=(34,10,114) rot=(0,0,1;0rad)
  Width = 6
FEATURE [Part::Box] Box952  label="Krychle952"
  AttacherType = Attacher::AttachEngine3D
  Height = 6
  Length = 2
  Placement = pos=(34,10,0) rot=(0,0,1;0rad)
  Width = 6
FEATURE [Part::Cylinder] Cylinder2086  label="Válec2086"
  Angle = 360
  AttacherType = Attacher::AttachEngine3D
  Height = 60
  Placement = pos=(26,67,3) rot=(0,1,0;1.5708rad)
  Radius = 1.75
FEATURE [Part::Cylinder] Cylinder2087  label="Válec2087"
  Angle = 360
  AttacherType = Attacher::AttachEngine3D
  Height = 10
  Placement = pos=(29,21,0) rot=(0,0,1;0rad)
  Radius = 1.5
FEATURE [Part::Compound] Compound1075
  Links = -> [Cylinder2062,Cylinder2081,Cylinder2087,Cylinder2065]
  Placement = pos=(0,0,-100) rot=(0,0,1;0rad)
FEATURE [Part::Cylinder] Cylinder2088  label="Válec2088"
  Angle = 360
  AttacherType = Attacher::AttachEngine3D
  Height = 60
  Placement = pos=(26,13,117) rot=(0,1,0;1.5708rad)
  Radius = 1.75
FEATURE [Part::Cylinder] Cylinder2089  label="Válec2089"
  Angle = 360
  AttacherType = Attacher::AttachEngine3D
  Height = 60
  Placement = pos=(26,67,117) rot=(0,1,0;1.5708rad)
  Radius = 1.75
FEATURE [Part::Box] Box953  label="Krychle953"
  AttacherType = Attacher::AttachEngine3D
  Height = 21
  Length = 17.5
  Placement = pos=(10.75,-2,42) rot=(0,0,1;0rad)
  Width = 10
FEATURE [Part::Chamfer] Chamfer085
  Base = -> Box953
  Edges = 1 edges r=3: [Edge2]
  Placement = pos=(-4,0,0) rot=(0,0,1;0rad)
FEATURE [Part::Box] Box954  label="Krychle954"
  AttacherType = Attacher::AttachEngine3D
  Height = 6
  Length = 2
  Placement = pos=(34,10,114) rot=(0,0,1;0rad)
  Width = 6
FEATURE [Part::Cylinder] Cylinder2090  label="Válec2090"
  Angle = 360
  AttacherType = Attacher::AttachEngine3D
  Height = 3
  Placement = pos=(26,7,3) rot=(0,1,0;1.5708rad)
  Radius = 3
FEATURE [Part::Box] Box955  label="Krychle955"
  AttacherType = Attacher::AttachEngine3D
  Height = 2
  Length = 6
  Placement = pos=(0,40,3) rot=(0,0,1;0rad)
  Width = 6
FEATURE [Part::Compound] Compound1080
  Links = -> [Box952,Box947,Box951,Box945]
  Placement = pos=(-8,0,-3) rot=(0,0,1;0rad)
FEATURE [Part::Compound] Compound1081
  Links = -> [Cylinder2057,Cylinder2082]
  Placement = pos=(-4,0,0) rot=(0,0,1;0rad)
FEATURE [Part::Compound] Compound1082
  Links = -> [Box930,Box955,Box931,Box948]
  Placement = pos=(0,0,-100) rot=(0,0,1;0rad)
FEATURE [Part::Compound] Compound1083
  Links = -> [Box946,Box938,Box954,Box949]
  Placement = pos=(-30,0,-3) rot=(0,0,1;0rad)
FEATURE [Part::Compound] Compound1084
  Links = -> [Cylinder2078,Cylinder2086,Cylinder2080,Cylinder2089]
  Placement = pos=(-8,0,-3) rot=(0,0,1;0rad)
FEATURE [Part::Compound] Compound1085
  Links = -> [Cylinder2054,Cylinder2056,Cylinder2053,Cylinder2059]
  Placement = pos=(-72,0,-3) rot=(0,0,1;0rad)
FEATURE [Part::Compound] Compound1086
  Links = -> [Cylinder2090,Cylinder2084,Cylinder2076,Cylinder2060]
  Placement = pos=(-26,0,-3) rot=(0,0,1;0rad)
FEATURE [Part::Compound] Compound1087
  Links = -> [Cylinder2063,Cylinder2058,Cylinder2061,Cylinder2070]
  Placement = pos=(3,0,-3) rot=(0,0,1;0rad)
FEATURE [Part::Compound] Compound1088
  Links = -> [Cylinder2066,Cylinder2064,Cylinder2088,Cylinder2073]
  Placement = pos=(-72,0,-3) rot=(0,0,1;0rad)
FEATURE [Part::Chamfer] Chamfer086
  Base = -> Compound1077
  Edges = 2 edges r=3: [Edge11,Edge34]
FEATURE [Part::Cut] Cut716
  Base = -> Cut711
  Tool = -> Compound1080
FEATURE [Part::Cut] Cut706
  Base = -> Cut716
  Tool = -> Compound1084
FEATURE [Part::Cut] Cut702
  Base = -> Cut706
  Tool = -> Cylinder2085
FEATURE [Part::Cut] Cut720
  Base = -> Cut702
  Tool = -> Chamfer085
FEATURE [Part::Cut] Cut718
  Base = -> Cut720
  Tool = -> Compound1081
FEATURE [Part::Cut] Cut707
  Base = -> Cut718
  Tool = -> Box950
FEATURE [Part::Cut] Cut717
  Base = -> Cut707
  Tool = -> Cylinder2079
FEATURE [Part::Cut] Cut710
  Base = -> Cut717
  Tool = -> Compound1082
FEATURE [Part::Cut] Cut715
  Base = -> Cut710
  Tool = -> Compound1075
FEATURE [Part::Cut] Cut703
  Base = -> Cut715
  Tool = -> Compound1083
FEATURE [Part::Cut] Cut719
  Base = -> Cut703
  Tool = -> Compound1088
FEATURE [Part::Cut] Cut722
  Base = -> Box936
  Tool = -> Box935
FEATURE [Part::Cut] Cut713
  Base = -> Cut722
  Tool = -> Compound1076
FEATURE [Part::Cut] Cut704
  Base = -> Cut713
  Tool = -> Compound1074
FEATURE [Part::Cut] Cut709
  Base = -> Cut704
  Tool = -> Cylinder2068
FEATURE [Part::Cut] Cut701
  Base = -> Cut709
  Tool = -> Cylinder2074
FEATURE [Part::Cut] Cut714
  Base = -> Cut701
  Tool = -> Cylinder2071
FEATURE [Part::Cut] Cut721
  Base = -> Cut714
  Tool = -> Cylinder2069
FEATURE [Part::Compound] Compound1079  label="Ele-box_small-extrusion003"
  Links = -> [Chamfer083,Cut721]
  Placement = pos=(32,16,77) rot=(0,1,0;3.14159rad)
FEATURE [Part::Cut] Cut723
  Base = -> Cut719
  Tool = -> Compound1085
FEATURE [Part::Cut] Cut705
  Base = -> Cut723
  Tool = -> Compound1087
FEATURE [Part::Cut] Cut708
  Base = -> Cut705
  Tool = -> Compound1086
FEATURE [Part::Cut] Cut700
  Base = -> Cut708
  Tool = -> Cylinder2077
FEATURE [Part::Chamfer] Chamfer084
  Base = -> Cut700
  Edges = 4 edges r=4: [Edge19,Edge22,Edge44,Edge48]
FEATURE [Part::Compound] Compound1078  label="Ele-box_standard003"
  Links = -> [Chamfer084,Chamfer086]
FEATURE [Part::Cut] Cut699
  Base = -> Compound1078
  Tool = -> Box943
FEATURE [Part::Cut] Cut712  label="Ele-box_standard004"
  Base = -> Cut699
  Tool = -> Cylinder2083
FEATURE [Part::Compound] Compound1089  label="Ele-box_small-hold-hole-opposite"
  Links = -> [Compound1079,Cut712]
FEATURE [Mesh::Feature] Mesh012  label="Ele-box_small-hold-hole (Meshed)"
FEATURE [Mesh::Feature] Mesh013  label="Ele-box_small-hold-hole-opposite (Meshed)"
note: 2 file-system paths scrubbed to <path> (originals preserved in the JSON sidecar)
